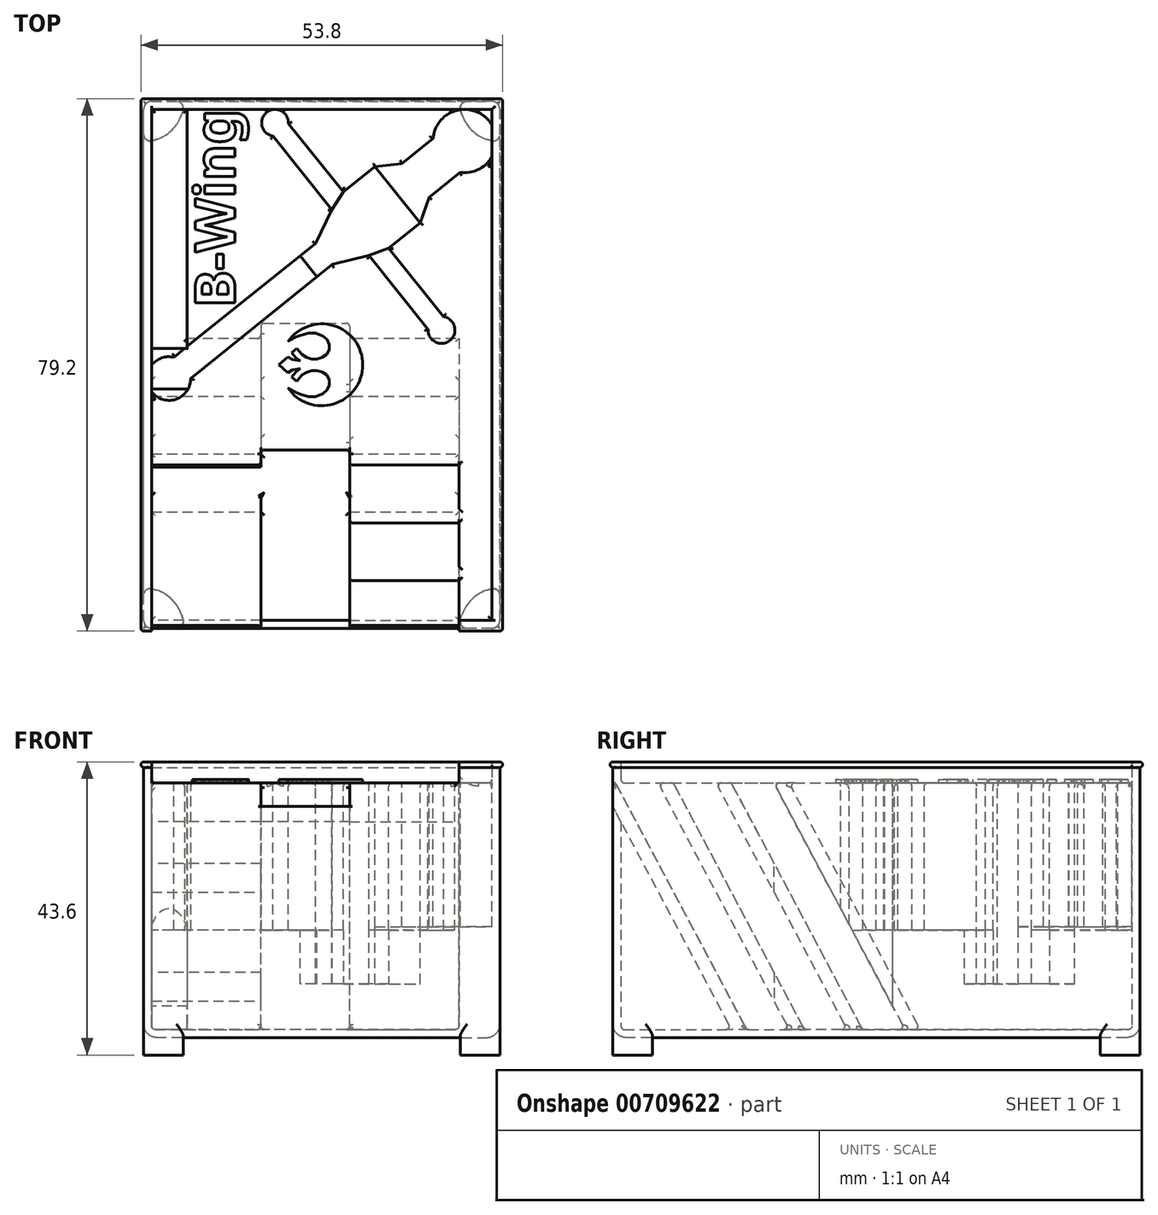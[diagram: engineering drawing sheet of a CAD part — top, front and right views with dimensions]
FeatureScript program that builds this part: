
annotation { "Feature Type Name" : "Feature", "Feature Type Description" : "" }
export const myFeature = defineFeature(function(context is Context, id is Id, definition is map)
    precondition{}
    {
        {
            var Q0;
            Q0=qCreatedBy(makeId("Front.planeOp"),FACE);
            var sketch = newSketch(context, id + "F0", { "sketchPlane" : qUnion([Q0])});
            skLineSegment(sketch, "E0.bottom", {"start": v(26.5, 20.5) * mm, "end": v(-26.5, 20.5) * mm});
            skLineSegment(sketch, "E0.top", {"start": v(26.5, -20.5) * mm, "end": v(-26.5, -20.5) * mm});
            skLineSegment(sketch, "E0.left", {"start": v(26.5, 20.5) * mm, "end": v(26.5, -20.5) * mm});
            skLineSegment(sketch, "E0.right", {"start": v(-26.5, 20.5) * mm, "end": v(-26.5, -20.5) * mm});
            skPoint(sketch, "E0.middle", {"position": v(0, 0) * mm});
            skSolve(sketch);
        }
        {
            var Q0;
            Q0=makeQuery(id+"F0.imprint","IMPRINT",FACE,{"disambiguationData":[TD([[makeQuery(id+"F0.imprint","IMPRINT",EDGE,{"derivedFrom":sQuery(id+"F0.wireOp",EDGE,"E0.bottom")}),1.0]])]});
            extrude(context, id + "F1", {"entities" : qUnion([Q0]), "depth" : 78.4 * mm, "offsetDistance" : 25 * mm, "symmetric" : true});
        }
        {
            var Q0;
            Q0=makeQuery(id+"F1.opExtrude","SWEPT_FACE",FACE,{"disambiguationData":[OSD([sQuery(id+"F0.wireOp",EDGE,"E0.bottom")])]});
            shell(context, id + "F2", {"entities" : qUnion([Q0]), "thickness" : 1.2 * mm});
        }
        {
            var Q0;
            Q0=makeQuery(id+"F1.opExtrude","SWEPT_FACE",FACE,{"disambiguationData":[OSD([sQuery(id+"F0.wireOp",EDGE,"E0.top")])]});
            var sketch = newSketch(context, id + "F3", { "sketchPlane" : qUnion([Q0])});
            skArc(sketch, "E1", {"start": v(20.62, 38) * mm, "mid": v(22.26, 34.96) * mm, "end": v(25.3, 33.32) * mm});
            skLineSegment(sketch, "E2", {"start": v(26.5, 39.2) * mm, "end": v(21.6, 39.2) * mm});
            skLineSegment(sketch, "E3", {"start": v(26.5, 39.2) * mm, "end": v(26.5, 34.3) * mm});
            skPoint(sketch, "E4.visualSharp", {"position": v(20.5, 39.2) * mm});
            skArc(sketch, "E4.filletArc", {"start": v(21.6, 39.2) * mm, "mid": v(20.83, 38.83) * mm, "end": v(20.62, 38) * mm});
            skPoint(sketch, "E5.visualSharp", {"position": v(26.5, 33.2) * mm});
            skArc(sketch, "E5.filletArc", {"start": v(25.3, 33.32) * mm, "mid": v(26.13, 33.53) * mm, "end": v(26.5, 34.3) * mm});
            skArc(sketch, "E6.MirrorCS", {"start": v(-25.3, 33.32) * mm, "mid": v(-26.13, 33.53) * mm, "end": v(-26.5, 34.3) * mm});
            skArc(sketch, "E7.MirrorCS", {"start": v(-21.6, 39.2) * mm, "mid": v(-20.83, 38.83) * mm, "end": v(-20.62, 38) * mm});
            skPoint(sketch, "E8.MirrorP", {"position": v(-20.5, 39.2) * mm});
            skArc(sketch, "E9.MirrorCS", {"start": v(-20.62, 38) * mm, "mid": v(-22.26, 34.96) * mm, "end": v(-25.3, 33.32) * mm});
            skLineSegment(sketch, "E10.MirrorCS", {"start": v(-26.5, 39.2) * mm, "end": v(-21.6, 39.2) * mm});
            skLineSegment(sketch, "E11.MirrorCS", {"start": v(-26.5, 39.2) * mm, "end": v(-26.5, 34.3) * mm});
            skPoint(sketch, "E12.MirrorP", {"position": v(-26.5, 33.2) * mm});
            skArc(sketch, "E13.MirrorCS", {"start": v(25.3, -33.32) * mm, "mid": v(26.13, -33.53) * mm, "end": v(26.5, -34.3) * mm});
            skArc(sketch, "E14.MirrorCS", {"start": v(21.6, -39.2) * mm, "mid": v(20.83, -38.83) * mm, "end": v(20.62, -38) * mm});
            skArc(sketch, "E15.MirrorCS", {"start": v(-25.3, -33.32) * mm, "mid": v(-26.13, -33.53) * mm, "end": v(-26.5, -34.3) * mm});
            skArc(sketch, "E16.MirrorCS", {"start": v(-21.6, -39.2) * mm, "mid": v(-20.83, -38.83) * mm, "end": v(-20.62, -38) * mm});
            skPoint(sketch, "E17.MirrorP", {"position": v(-26.5, -33.2) * mm});
            skPoint(sketch, "E18.MirrorP", {"position": v(20.5, -39.2) * mm});
            skPoint(sketch, "E19.MirrorP", {"position": v(26.5, -33.2) * mm});
            skLineSegment(sketch, "E20.MirrorCS", {"start": v(-26.5, -39.2) * mm, "end": v(-26.5, -34.3) * mm});
            skPoint(sketch, "E21.MirrorP", {"position": v(-20.5, -39.2) * mm});
            skLineSegment(sketch, "E22.MirrorCS", {"start": v(26.5, -39.2) * mm, "end": v(26.5, -34.3) * mm});
            skLineSegment(sketch, "E23.MirrorCS", {"start": v(-26.5, -39.2) * mm, "end": v(-21.6, -39.2) * mm});
            skLineSegment(sketch, "E24.MirrorCS", {"start": v(26.5, -39.2) * mm, "end": v(21.6, -39.2) * mm});
            skArc(sketch, "E25.MirrorCS", {"start": v(20.62, -38) * mm, "mid": v(22.26, -34.96) * mm, "end": v(25.3, -33.32) * mm});
            skArc(sketch, "E26.MirrorCS", {"start": v(-20.62, -38) * mm, "mid": v(-22.26, -34.96) * mm, "end": v(-25.3, -33.32) * mm});
            skSolve(sketch);
        }
        {
            var Q0;
            Q0=qSketchRegion(id+"F3",true);
            extrude(context, id + "F4", {"entities" : qUnion([Q0]), "operationType" : NewBodyOperationType.ADD, "depth" : 2.6 * mm, "offsetDistance" : 25 * mm});
        }
        {
            var Q0;
            Q0=makeQuery(id+"F4.boolean.opBoolean","MERGE",FACE,{"derivedFrom":[makeQuery(id+"F1.opExtrude","CAP_FACE",FACE,{"disambiguationData":[OSD([sQuery(id+"F0.wireOp",EDGE,"E0.bottom"),sQuery(id+"F0.wireOp",EDGE,"E0.top"),sQuery(id+"F0.wireOp",EDGE,"E0.left"),sQuery(id+"F0.wireOp",EDGE,"E0.right")])],"isStart":false}),makeQuery(id+"F4.opExtrude","SWEPT_FACE",FACE,{"disambiguationData":[OSD([sQuery(id+"F3.wireOp",EDGE,"E2")])]}),makeQuery(id+"F4.opExtrude","SWEPT_FACE",FACE,{"disambiguationData":[OSD([sQuery(id+"F3.wireOp",EDGE,"E10.MirrorCS")])]})]});
            var sketch = newSketch(context, id + "F5", { "sketchPlane" : qUnion([Q0])});
            skLineSegment(sketch, "E27", {"start": v(-26.5, 20.5) * mm, "end": v(-26.5, 19.7) * mm});
            skArc(sketch, "E28", {"start": v(-26.5, 20.5) * mm, "mid": v(-26.9, 20.1) * mm, "end": v(-26.5, 19.7) * mm});
            skSolve(sketch);
        }
        {
            var Q0;
            Q0=makeQuery(id+"F5.imprint","IMPRINT",FACE,{"disambiguationData":[TD([[makeQuery(id+"F5.imprint","IMPRINT",EDGE,{"derivedFrom":sQuery(id+"F5.wireOp",EDGE,"E27")}),-1.0]])]});
            var Q1;
            Q1=makeQuery(id+"F1.opExtrude","SWEPT_EDGE",EDGE,{"disambiguationData":[OSD([sQuery(id+"F0.wireOp",EDGE,"E0.bottom"),sQuery(id+"F0.wireOp",EDGE,"E0.right")])]});
            var Q2;
            Q2=makeQuery(id+"F1.opExtrude","CAP_EDGE",EDGE,{"disambiguationData":[OSD([sQuery(id+"F0.wireOp",EDGE,"E0.bottom")])],"isStart":false});
            var Q3;
            Q3=makeQuery(id+"F1.opExtrude","SWEPT_EDGE",EDGE,{"disambiguationData":[OSD([sQuery(id+"F0.wireOp",EDGE,"E0.bottom"),sQuery(id+"F0.wireOp",EDGE,"E0.left")])]});
            var Q4;
            Q4=makeQuery(id+"F1.opExtrude","CAP_EDGE",EDGE,{"disambiguationData":[OSD([sQuery(id+"F0.wireOp",EDGE,"E0.bottom")])],"isStart":true});
            sweep(context, id + "F6", {"operationType" : NewBodyOperationType.ADD, "profiles" : qUnion([Q0]), "path" : qUnion([Q1, Q2, Q3, Q4])});
        }
        {
            var Q0;
            Q0=makeQuery(id+"F1.opExtrude","CAP_EDGE",EDGE,{"disambiguationData":[OSD([sQuery(id+"F0.wireOp",EDGE,"E0.top")])],"isStart":false});
            var Q1;
            Q1=makeQuery(id+"F1.opExtrude","SWEPT_EDGE",EDGE,{"disambiguationData":[OSD([sQuery(id+"F0.wireOp",EDGE,"E0.top"),sQuery(id+"F0.wireOp",EDGE,"E0.left")])]});
            var Q2;
            Q2=makeQuery(id+"F1.opExtrude","SWEPT_EDGE",EDGE,{"disambiguationData":[OSD([sQuery(id+"F0.wireOp",EDGE,"E0.top"),sQuery(id+"F0.wireOp",EDGE,"E0.right")])]});
            var Q3;
            Q3=makeQuery(id+"F1.opExtrude","CAP_EDGE",EDGE,{"disambiguationData":[OSD([sQuery(id+"F0.wireOp",EDGE,"E0.top")])],"isStart":true});
            fillet(context, id + "F7", {"entities" : qUnion([Q0, Q1, Q2, Q3]), "radius" : 2 * mm, "tangentPropagation" : true, "allowEdgeOverflow" : false});
        }
        {
            var Q0;
            Q0=makeQuery(id+"F4.boolean.opBoolean","MERGE",EDGE,{"derivedFrom":[makeQuery(id+"F1.opExtrude","CAP_EDGE",EDGE,{"disambiguationData":[OSD([sQuery(id+"F0.wireOp",EDGE,"E0.right")])],"isStart":false}),makeQuery(id+"F4.opExtrude","SWEPT_EDGE",EDGE,{"disambiguationData":[OSD([sQuery(id+"F3.wireOp",EDGE,"E10.MirrorCS"),sQuery(id+"F3.wireOp",EDGE,"E11.MirrorCS")])]})]});
            var Q1;
            Q1=makeQuery(id+"F4.boolean.opBoolean","MERGE",EDGE,{"derivedFrom":[makeQuery(id+"F1.opExtrude","CAP_EDGE",EDGE,{"disambiguationData":[OSD([sQuery(id+"F0.wireOp",EDGE,"E0.left")])],"isStart":false}),makeQuery(id+"F4.opExtrude","SWEPT_EDGE",EDGE,{"disambiguationData":[OSD([sQuery(id+"F3.wireOp",EDGE,"E2"),sQuery(id+"F3.wireOp",EDGE,"E3")])]})]});
            var Q2;
            Q2=makeQuery(id+"F4.boolean.opBoolean","MERGE",EDGE,{"derivedFrom":[makeQuery(id+"F1.opExtrude","CAP_EDGE",EDGE,{"disambiguationData":[OSD([sQuery(id+"F0.wireOp",EDGE,"E0.left")])],"isStart":true}),makeQuery(id+"F4.opExtrude","SWEPT_EDGE",EDGE,{"disambiguationData":[OSD([sQuery(id+"F3.wireOp",EDGE,"E22.MirrorCS"),sQuery(id+"F3.wireOp",EDGE,"E24.MirrorCS")])]})]});
            var Q3;
            Q3=makeQuery(id+"F4.boolean.opBoolean","MERGE",EDGE,{"derivedFrom":[makeQuery(id+"F1.opExtrude","CAP_EDGE",EDGE,{"disambiguationData":[OSD([sQuery(id+"F0.wireOp",EDGE,"E0.right")])],"isStart":true}),makeQuery(id+"F4.opExtrude","SWEPT_EDGE",EDGE,{"disambiguationData":[OSD([sQuery(id+"F3.wireOp",EDGE,"E20.MirrorCS"),sQuery(id+"F3.wireOp",EDGE,"E23.MirrorCS")])]})]});
            fillet(context, id + "F8", {"entities" : qUnion([Q0, Q1, Q2, Q3]), "radius" : 1.2 * mm, "tangentPropagation" : true, "allowEdgeOverflow" : false});
        }
        {
            var Q0;
            Q0=makeQuery(id+"F6.opSweep","MID_CAP_EDGE",EDGE,{"disambiguationData":[OSD([sQuery(id+"F0.wireOp",EDGE,"E0.bottom"),sQuery(id+"F0.wireOp",EDGE,"E0.right"),sQuery(id+"F5.wireOp",EDGE,"E28")])],"capPos":1.0});
            var Q1;
            Q1=makeQuery(id+"F6.opSweep","CAP_EDGE",EDGE,{"disambiguationData":[OSD([sQuery(id+"F0.wireOp",EDGE,"E0.bottom"),sQuery(id+"F0.wireOp",EDGE,"E0.right"),sQuery(id+"F5.wireOp",EDGE,"E28")])],"isStart":true});
            var Q2;
            Q2=makeQuery(id+"F6.opSweep","MID_CAP_EDGE",EDGE,{"disambiguationData":[OSD([sQuery(id+"F0.wireOp",EDGE,"E0.bottom"),sQuery(id+"F0.wireOp",EDGE,"E0.left"),sQuery(id+"F5.wireOp",EDGE,"E28")])],"capPos":3.0});
            var Q3;
            Q3=makeQuery(id+"F6.opSweep","MID_CAP_EDGE",EDGE,{"disambiguationData":[OSD([sQuery(id+"F0.wireOp",EDGE,"E0.bottom"),sQuery(id+"F0.wireOp",EDGE,"E0.left"),sQuery(id+"F5.wireOp",EDGE,"E28")])],"capPos":2.0});
            fillet(context, id + "F9", {"entities" : qUnion([Q0, Q1, Q2, Q3]), "radius" : .4 * mm, "tangentPropagation" : true, "allowEdgeOverflow" : false});
        }
        {
            var Q0;
            {var subQ0=sQuery(id+"F0.wireOp",EDGE,"E0.bottom");Q0=makeQuery(id+"F2.opShell","OFFSET_EDGE",EDGE,{"disambiguationData":[OSD([subQ0]),TDD([makeQuery(id+"F1.opExtrude","CAP_EDGE",EDGE,{"disambiguationData":[OSD([subQ0])],"isStart":false})])]});}
            cPlane(context, id + "F10", {"entities" : qUnion([Q0]), "cplaneType" : CPlaneType.LINE_ANGLE, "offset" : 25 * mm, "angle" : 62 * degree, "width" : 150 * mm, "height" : 150 * mm});
        }
        {
            var Q0;
            Q0=makeQuery(id+"F1.opExtrude","SWEPT_FACE",FACE,{"disambiguationData":[OSD([sQuery(id+"F0.wireOp",EDGE,"E0.bottom")])]});
            var sketch = newSketch(context, id + "F11", { "sketchPlane" : qUnion([Q0])});
            skLineSegment(sketch, "E29", {"start": v(9.97, 17.35) * mm, "end": v(18.16, 7.15) * mm});
            skLineSegment(sketch, "E30", {"start": v(9.97, 17.35) * mm, "end": v(14.64, 21.1) * mm});
            skLineSegment(sketch, "E31", {"start": v(1.56, 14.91) * mm, "end": v(-19.49, -2) * mm});
            skLineSegment(sketch, "E32", {"start": v(15.96, 24.88) * mm, "end": v(20.63, 28.64) * mm});
            skLineSegment(sketch, "E33", {"start": v(7, 16.25) * mm, "end": v(1.56, 14.91) * mm});
            skLineSegment(sketch, "E34", {"start": v(14.64, 21.1) * mm, "end": v(15.96, 24.88) * mm});
            skArc(sketch, "E35", {"start": v(-25.27, -4.08) * mm, "mid": v(-21.64, -5.1) * mm, "end": v(-19.49, -2) * mm});
            skArc(sketch, "E36", {"start": v(20.63, 28.64) * mm, "mid": v(23.3, 29.08) * mm, "end": v(25.3, 30.92) * mm});
            skArc(sketch, "E37", {"start": v(15.82, 5.27) * mm, "mid": v(19.07, 3.62) * mm, "end": v(18.16, 7.15) * mm});
            skLineSegment(sketch, "E38.trimOffspring", {"start": v(15.82, 5.27) * mm, "end": v(7, 16.25) * mm});
            skLineSegment(sketch, "E39.MirrorCS", {"start": v(7.92, 29.47) * mm, "end": v(11.9, 29.94) * mm});
            skLineSegment(sketch, "E40.MirrorCS", {"start": v(11.9, 29.94) * mm, "end": v(16.57, 33.7) * mm});
            skArc(sketch, "E41.MirrorCS", {"start": v(16.57, 33.7) * mm, "mid": v(19.88, 37.8) * mm, "end": v(24.91, 36.24) * mm});
            skLineSegment(sketch, "E42.MirrorCS", {"start": v(3.24, 25.71) * mm, "end": v(7.92, 29.47) * mm});
            skLineSegment(sketch, "E43.MirrorCS", {"start": v(-7.29, 34.03) * mm, "end": v(1.53, 23.06) * mm});
            skArc(sketch, "E44.MirrorCS", {"start": v(-25.27, -4.08) * mm, "mid": v(-25.29, -4.06) * mm, "end": v(-25.3, -4.05) * mm});
            skLineSegment(sketch, "E45.MirrorCS", {"start": v(1.53, 23.06) * mm, "end": v(-0.95, 18.03) * mm});
            skLineSegment(sketch, "E46.MirrorCS", {"start": v(-0.95, 18.03) * mm, "end": v(-22, 1.12) * mm});
            skLineSegment(sketch, "E47.MirrorCS", {"start": v(3.24, 25.71) * mm, "end": v(-4.95, 35.9) * mm});
            skArc(sketch, "E48.MirrorCS", {"start": v(-7.29, 34.03) * mm, "mid": v(-8.2, 37.56) * mm, "end": v(-4.95, 35.9) * mm});
            skPoint(sketch, "E49.MirrorP", {"position": v(14.23, 31.82) * mm});
            skLineSegment(sketch, "E50.0", {"start": v(25.3, 38) * mm, "end": v(-25.3, 38) * mm});
            skArc(sketch, "E51.MirrorCS", {"start": v(25.27, 4.08) * mm, "mid": v(25.29, 4.06) * mm, "end": v(25.3, 4.05) * mm});
            skArc(sketch, "E52.trimOffspring", {"start": v(25.3, 35.68) * mm, "mid": v(25.12, 35.97) * mm, "end": v(24.91, 36.24) * mm});
            skArc(sketch, "E53.trimOffspring", {"start": v(-25.3, -0.05) * mm, "mid": v(-23.82, 1.02) * mm, "end": v(-22, 1.12) * mm});
            skLineSegment(sketch, "E54", {"start": v(7.92, 29.47) * mm, "end": v(14.64, 21.1) * mm});
            skLineSegment(sketch, "E55", {"start": v(-22, 1.12) * mm, "end": v(-19.49, -2) * mm});
            skLineSegment(sketch, "E56", {"start": v(-1.97, 14.64) * mm, "end": v(-0.72, 13.08) * mm});
            skLineSegment(sketch, "E57", {"start": v(-0.72, 13.08) * mm, "end": v(-3.22, 16.2) * mm});
            skLineSegment(sketch, "E58", {"start": v(3.24, 25.71) * mm, "end": v(1.53, 23.06) * mm});
            skLineSegment(sketch, "E59", {"start": v(9.97, 17.35) * mm, "end": v(7, 16.25) * mm});
            skLineSegment(sketch, "E60", {"start": v(-26.5, -39.2) * mm, "end": v(-26.5, -15.2) * mm});
            skLineSegment(sketch, "E61", {"start": v(-26.5, -15.2) * mm, "end": v(20.4, -15.2) * mm});
            skLineSegment(sketch, "E62", {"start": v(25.3, -38) * mm, "end": v(20.4, -38) * mm});
            skLineSegment(sketch, "E63", {"start": v(20.4, -38) * mm, "end": v(20.4, -15.2) * mm});
            skPoint(sketch, "E64.orphan", {"position": v(26.5, -15.2) * mm});
            skSolve(sketch);
        }
        {
            var Q0;
            Q0=makeQuery(id+"F2.opShell","OFFSET_FACE",FACE,{"disambiguationData":[OSD([sQuery(id+"F0.wireOp",EDGE,"E0.top")])]});
            var sketch = newSketch(context, id + "F12", { "sketchPlane" : qUnion([Q0])});
            skLineSegment(sketch, "E65", {"start": v(9.97, 17.35) * mm, "end": v(18.16, 7.15) * mm});
            skLineSegment(sketch, "E66", {"start": v(9.97, 17.35) * mm, "end": v(14.64, 21.1) * mm});
            skLineSegment(sketch, "E67", {"start": v(1.56, 14.91) * mm, "end": v(-19.49, -2) * mm});
            skLineSegment(sketch, "E68", {"start": v(15.96, 24.88) * mm, "end": v(20.63, 28.64) * mm});
            skLineSegment(sketch, "E69", {"start": v(7, 16.25) * mm, "end": v(1.56, 14.91) * mm});
            skLineSegment(sketch, "E70", {"start": v(14.64, 21.1) * mm, "end": v(15.96, 24.88) * mm});
            skArc(sketch, "E71", {"start": v(-25.27, -4.08) * mm, "mid": v(-21.64, -5.1) * mm, "end": v(-19.49, -2) * mm});
            skArc(sketch, "E72", {"start": v(20.63, 28.64) * mm, "mid": v(23.3, 29.08) * mm, "end": v(25.3, 30.92) * mm});
            skArc(sketch, "E73", {"start": v(15.82, 5.27) * mm, "mid": v(19.07, 3.62) * mm, "end": v(18.16, 7.15) * mm});
            skLineSegment(sketch, "E74.trimOffspring", {"start": v(15.82, 5.27) * mm, "end": v(7, 16.25) * mm});
            skLineSegment(sketch, "E75.MirrorCS", {"start": v(7.92, 29.47) * mm, "end": v(11.9, 29.94) * mm});
            skLineSegment(sketch, "E76.MirrorCS", {"start": v(11.9, 29.94) * mm, "end": v(16.57, 33.7) * mm});
            skArc(sketch, "E77.MirrorCS", {"start": v(16.57, 33.7) * mm, "mid": v(19.88, 37.8) * mm, "end": v(24.91, 36.24) * mm});
            skLineSegment(sketch, "E78.MirrorCS", {"start": v(3.24, 25.71) * mm, "end": v(7.92, 29.47) * mm});
            skLineSegment(sketch, "E79.MirrorCS", {"start": v(-7.29, 34.03) * mm, "end": v(1.53, 23.06) * mm});
            skArc(sketch, "E80.MirrorCS", {"start": v(-25.27, -4.08) * mm, "mid": v(-25.29, -4.06) * mm, "end": v(-25.3, -4.05) * mm});
            skLineSegment(sketch, "E81.MirrorCS", {"start": v(1.53, 23.06) * mm, "end": v(-0.95, 18.03) * mm});
            skLineSegment(sketch, "E82.MirrorCS", {"start": v(-0.95, 18.03) * mm, "end": v(-22, 1.12) * mm});
            skLineSegment(sketch, "E83.MirrorCS", {"start": v(3.24, 25.71) * mm, "end": v(-4.95, 35.9) * mm});
            skArc(sketch, "E84.MirrorCS", {"start": v(-7.29, 34.03) * mm, "mid": v(-8.2, 37.56) * mm, "end": v(-4.95, 35.9) * mm});
            skPoint(sketch, "E85.MirrorP", {"position": v(14.23, 31.82) * mm});
            skLineSegment(sketch, "E86.0", {"start": v(25.3, 38) * mm, "end": v(-25.3, 38) * mm});
            skArc(sketch, "E87.MirrorCS", {"start": v(25.27, 4.08) * mm, "mid": v(25.29, 4.06) * mm, "end": v(25.3, 4.05) * mm});
            skArc(sketch, "E88.trimOffspring", {"start": v(25.3, 35.68) * mm, "mid": v(25.12, 35.97) * mm, "end": v(24.91, 36.24) * mm});
            skArc(sketch, "E89.trimOffspring", {"start": v(-25.3, -0.05) * mm, "mid": v(-23.82, 1.02) * mm, "end": v(-22, 1.12) * mm});
            skLineSegment(sketch, "E90", {"start": v(7.92, 29.47) * mm, "end": v(14.64, 21.1) * mm});
            skLineSegment(sketch, "E91", {"start": v(-22, 1.12) * mm, "end": v(-19.49, -2) * mm});
            skLineSegment(sketch, "E92", {"start": v(-1.97, 14.64) * mm, "end": v(-0.72, 13.08) * mm});
            skLineSegment(sketch, "E93", {"start": v(-0.72, 13.08) * mm, "end": v(-3.22, 16.2) * mm});
            skLineSegment(sketch, "E94", {"start": v(3.24, 25.71) * mm, "end": v(1.53, 23.06) * mm});
            skLineSegment(sketch, "E95", {"start": v(9.97, 17.35) * mm, "end": v(7, 16.25) * mm});
            skLineSegment(sketch, "E96", {"start": v(-26.5, -39.2) * mm, "end": v(-26.5, -15.2) * mm});
            skLineSegment(sketch, "E97", {"start": v(-26.5, -15.2) * mm, "end": v(20.4, -15.2) * mm});
            skLineSegment(sketch, "E98", {"start": v(25.3, -39.5) * mm, "end": v(20.4, -39.5) * mm});
            skLineSegment(sketch, "E99", {"start": v(20.4, -38) * mm, "end": v(20.4, -15.2) * mm});
            skPoint(sketch, "E100.orphan", {"position": v(26.5, -15.2) * mm});
            skSolve(sketch);
        }
        {
            var Q0;
            Q0=makeQuery(id+"F2.opShell","OFFSET_FACE",FACE,{"disambiguationData":[OSD([sQuery(id+"F0.wireOp",EDGE,"E0.top")])]});
            var sketch = newSketch(context, id + "F13", { "sketchPlane" : qUnion([Q0])});
            skLineSegment(sketch, "E101.2", {"start": v(26.5, 6.4) * mm, "end": v(26.5, 39.2) * mm});
            skPoint(sketch, "E102", {"position": v(-22.55, 27.66) * mm});
            skLineSegment(sketch, "E103", {"start": v(-20, 38) * mm, "end": v(-20, 2.4) * mm});
            skLineSegment(sketch, "E104", {"start": v(-20, 2.4) * mm, "end": v(-25.3, 2.4) * mm});
            skLineSegment(sketch, "E105", {"start": v(-25.3, 2.4) * mm, "end": v(-25.3, 38) * mm});
            skLineSegment(sketch, "E106", {"start": v(-25.3, 38) * mm, "end": v(-20, 38) * mm});
            skSolve(sketch);
        }
        {
            var Q0;
            Q0=qCreatedBy(id+"F10.planeOp",FACE);
            var sketch = newSketch(context, id + "F14", { "sketchPlane" : qUnion([Q0])});
            skPoint(sketch, "E107.0", {"position": v(-25.3, -26.1) * mm});
            skPoint(sketch, "E108.0", {"position": v(13.11, 38) * mm});
            skLineSegment(sketch, "E109", {"start": v(13.11, 38) * mm, "end": v(13.11, 12.8) * mm});
            skLineSegment(sketch, "E110.0", {"start": v(-25.3, -38) * mm, "end": v(-25.3, 38) * mm});
            skLineSegment(sketch, "E111.bottom", {"start": v(20.4, -3.3) * mm, "end": v(20.4, -5.3) * mm});
            skLineSegment(sketch, "E111.top", {"start": v(4.15, -3.3) * mm, "end": v(4.15, -5.3) * mm});
            skLineSegment(sketch, "E111.left", {"start": v(20.4, -3.3) * mm, "end": v(4.15, -3.3) * mm});
            skLineSegment(sketch, "E111.right", {"start": v(20.4, -5.3) * mm, "end": v(4.15, -5.3) * mm});
            skLineSegment(sketch, "E112", {"start": v(20.4, -5.3) * mm, "end": v(20.4, -10.9) * mm});
            skLineSegment(sketch, "E113", {"start": v(20.4, -10.9) * mm, "end": v(4.15, -10.9) * mm});
            skLineSegment(sketch, "E114", {"start": v(4.15, -10.9) * mm, "end": v(4.15, -12.9) * mm});
            skLineSegment(sketch, "E115", {"start": v(4.15, -12.9) * mm, "end": v(20.4, -12.9) * mm});
            skLineSegment(sketch, "E116", {"start": v(20.4, -12.9) * mm, "end": v(20.4, -18.5) * mm});
            skLineSegment(sketch, "E117", {"start": v(20.4, -18.5) * mm, "end": v(4.15, -18.5) * mm});
            skLineSegment(sketch, "E118", {"start": v(4.15, -18.5) * mm, "end": v(4.15, -20.5) * mm});
            skLineSegment(sketch, "E119", {"start": v(4.15, -20.5) * mm, "end": v(20.4, -20.5) * mm});
            skLineSegment(sketch, "E120", {"start": v(20.4, -20.5) * mm, "end": v(20.4, -26.1) * mm});
            skLineSegment(sketch, "E121", {"start": v(20.4, -26.1) * mm, "end": v(4.15, -26.1) * mm});
            skLineSegment(sketch, "E122", {"start": v(4.15, -26.1) * mm, "end": v(4.15, -28.1) * mm});
            skLineSegment(sketch, "E123", {"start": v(4.15, -28.1) * mm, "end": v(20.4, -28.1) * mm});
            skLineSegment(sketch, "E124", {"start": v(20.4, -28.1) * mm, "end": v(20.4, -26.1) * mm});
            skLineSegment(sketch, "E125", {"start": v(20.4, -10.9) * mm, "end": v(20.4, -12.9) * mm});
            skLineSegment(sketch, "E126", {"start": v(20.4, -18.5) * mm, "end": v(20.4, -20.5) * mm});
            skLineSegment(sketch, "E127", {"start": v(4.15, -3.3) * mm, "end": v(-9.05, -3.3) * mm});
            skLineSegment(sketch, "E128", {"start": v(4.15, -28.1) * mm, "end": v(-9.05, -28.1) * mm});
            skPoint(sketch, "E129.startSnap0", {"position": v(-2.45, -3.3) * mm});
            skLineSegment(sketch, "E130.MirrorCS", {"start": v(-25.3, -10.9) * mm, "end": v(-25.3, -12.9) * mm});
            skLineSegment(sketch, "E131.MirrorCS", {"start": v(-25.3, -18.5) * mm, "end": v(-25.3, -20.5) * mm});
            skLineSegment(sketch, "E132.MirrorCS", {"start": v(-9.05, -10.9) * mm, "end": v(-9.05, -12.9) * mm});
            skLineSegment(sketch, "E133.MirrorCS", {"start": v(-9.05, -3.3) * mm, "end": v(-9.05, -5.3) * mm});
            skLineSegment(sketch, "E134.MirrorCS", {"start": v(-9.05, -18.5) * mm, "end": v(-9.05, -20.5) * mm});
            skLineSegment(sketch, "E135.MirrorCS", {"start": v(-9.05, -26.1) * mm, "end": v(-9.05, -28.1) * mm});
            skLineSegment(sketch, "E136.MirrorCS", {"start": v(-25.3, -3.3) * mm, "end": v(-25.3, -5.3) * mm});
            skLineSegment(sketch, "E137.MirrorCS", {"start": v(-9.05, -12.9) * mm, "end": v(-25.3, -12.9) * mm});
            skLineSegment(sketch, "E138.MirrorCS", {"start": v(-9.05, -20.5) * mm, "end": v(-25.3, -20.5) * mm});
            skLineSegment(sketch, "E139.MirrorCS", {"start": v(-25.3, -3.3) * mm, "end": v(-9.05, -3.3) * mm});
            skLineSegment(sketch, "E140.MirrorCS", {"start": v(-25.3, -5.3) * mm, "end": v(-25.3, -10.9) * mm});
            skLineSegment(sketch, "E141.MirrorCS", {"start": v(-9.05, -28.1) * mm, "end": v(-25.3, -28.1) * mm});
            skLineSegment(sketch, "E142.MirrorCS", {"start": v(-25.3, -10.9) * mm, "end": v(-9.05, -10.9) * mm});
            skLineSegment(sketch, "E143.MirrorCS", {"start": v(-25.3, -5.3) * mm, "end": v(-9.05, -5.3) * mm});
            skLineSegment(sketch, "E144.MirrorCS", {"start": v(-25.3, -12.9) * mm, "end": v(-25.3, -18.5) * mm});
            skLineSegment(sketch, "E145.MirrorCS", {"start": v(-25.3, -26.1) * mm, "end": v(-9.05, -26.1) * mm});
            skLineSegment(sketch, "E146.MirrorCS", {"start": v(-25.3, -20.5) * mm, "end": v(-25.3, -26.1) * mm});
            skLineSegment(sketch, "E147.MirrorCS", {"start": v(-25.3, -18.5) * mm, "end": v(-9.05, -18.5) * mm});
            skPoint(sketch, "E148.0", {"position": v(-13.11, -9.06) * mm});
            skLineSegment(sketch, "E149", {"start": v(-25.3, -26.1) * mm, "end": v(-25.3, -23.93) * mm});
            skSolve(sketch);
        }
        {
            var Q0;
            Q0 = qSketchRegion(id + "F12", true);
            var Q1;
            {var subQ7=sQuery(id+"F12.wireOp",EDGE,"E79.MirrorCS");Q1=makeQuery(id+"F12.imprint","IMPRINT",FACE,{"disambiguationData":[TD([[makeQuery(id+"F12.imprint","IMPRINT",EDGE,{"derivedFrom":subQ7}),-1.0]])]});}
            var Q2;
            Q2=makeQuery(id+"F12.imprint","IMPRINT",FACE,{"disambiguationData":[TD([[makeQuery(id+"F12.imprint","IMPRINT",EDGE,{"derivedFrom":sQuery(id+"F12.wireOp",EDGE,"E68")}),1.0]])]});
            var Q3;
            Q3=makeQuery(id+"F12.imprint","IMPRINT",FACE,{"disambiguationData":[TD([[makeQuery(id+"F12.imprint","IMPRINT",EDGE,{"derivedFrom":sQuery(id+"F12.wireOp",EDGE,"E65")}),1.0]])]});
            var Q4;
            Q4=makeQuery(id+"F12.imprint","IMPRINT",FACE,{"disambiguationData":[TD([[makeQuery(id+"F12.imprint","IMPRINT",EDGE,{"derivedFrom":sQuery(id+"F12.wireOp",EDGE,"E71")}),1.0]])]});
            var Q5;
            {var subQ0=sQuery(id+"F12.wireOp",EDGE,"E88.trimOffspring");Q5=makeQuery(id+"F12.imprint","IMPRINT",FACE,{"disambiguationData":[TD([[makeQuery(id+"F12.imprint","IMPRINT",EDGE,{"derivedFrom":subQ0}),-1.0]])]});}
            var Q6;
            Q6=makeQuery(id+"F2.opShell","OFFSET_FACE",FACE,{"disambiguationData":[OSD([sQuery(id+"F0.wireOp",EDGE,"E0.top")])]});
            extrude(context, id + "F15", {"entities" : qUnion([Q0, Q1, Q2, Q3, Q4, Q5]), "operationType" : NewBodyOperationType.ADD, "depth" : 36.7 * mm, "endBoundEntityFace" : qUnion([Q6]), "offsetDistance" : 25 * mm});
        }
        {
            var Q0;
            Q0=makeQuery(id+"F14.imprint","IMPRINT",FACE,{"disambiguationData":[TD([[makeQuery(id+"F14.imprint","IMPRINT",EDGE,{"derivedFrom":sQuery(id+"F14.wireOp",EDGE,"E111.top")}),-1.0]])]});
            var Q1;
            Q1=makeQuery(id+"F2.opShell","OFFSET_FACE",FACE,{"disambiguationData":[OSD([sQuery(id+"F0.wireOp",EDGE,"E0.top")])]});
            extrude(context, id + "F16", {"entities" : qUnion([Q0]), "operationType" : NewBodyOperationType.REMOVE, "endBound" : BoundingType.UP_TO_SURFACE, "oppositeDirection" : true, "depth" : 25 * mm, "endBoundEntityFace" : qUnion([Q1]), "offsetDistance" : 25 * mm, "hasSecondDirection" : true, "secondDirectionOppositeDirection" : false, "secondDirectionDepth" : 25 * mm});
        }
        {
            var Q0;
            Q0=makeQuery(id+"F14.imprint","IMPRINT",FACE,{"disambiguationData":[TD([[makeQuery(id+"F14.imprint","IMPRINT",EDGE,{"derivedFrom":sQuery(id+"F14.wireOp",EDGE,"E133.MirrorCS")}),-1.0]])]});
            var Q1;
            Q1=makeQuery(id+"F14.imprint","IMPRINT",FACE,{"disambiguationData":[TD([[makeQuery(id+"F14.imprint","IMPRINT",EDGE,{"derivedFrom":sQuery(id+"F14.wireOp",EDGE,"E111.bottom")}),-1.0]])]});
            var Q2;
            Q2=makeQuery(id+"F14.imprint","IMPRINT",FACE,{"disambiguationData":[TD([[makeQuery(id+"F14.imprint","IMPRINT",EDGE,{"derivedFrom":sQuery(id+"F14.wireOp",EDGE,"E113")}),1.0]])]});
            var Q3;
            Q3=makeQuery(id+"F14.imprint","IMPRINT",FACE,{"disambiguationData":[TD([[makeQuery(id+"F14.imprint","IMPRINT",EDGE,{"derivedFrom":sQuery(id+"F14.wireOp",EDGE,"E117")}),1.0]])]});
            var Q4;
            Q4=makeQuery(id+"F14.imprint","IMPRINT",FACE,{"disambiguationData":[TD([[makeQuery(id+"F14.imprint","IMPRINT",EDGE,{"derivedFrom":sQuery(id+"F14.wireOp",EDGE,"E121")}),1.0]])]});
            var Q5;
            Q5=makeQuery(id+"F14.imprint","IMPRINT",FACE,{"disambiguationData":[TD([[makeQuery(id+"F14.imprint","IMPRINT",EDGE,{"derivedFrom":sQuery(id+"F14.wireOp",EDGE,"E135.MirrorCS")}),-1.0]])]});
            var Q6;
            Q6=makeQuery(id+"F14.imprint","IMPRINT",FACE,{"disambiguationData":[TD([[makeQuery(id+"F14.imprint","IMPRINT",EDGE,{"derivedFrom":sQuery(id+"F14.wireOp",EDGE,"E131.MirrorCS")}),1.0]])]});
            var Q7;
            Q7=makeQuery(id+"F14.imprint","IMPRINT",FACE,{"disambiguationData":[TD([[makeQuery(id+"F14.imprint","IMPRINT",EDGE,{"derivedFrom":sQuery(id+"F14.wireOp",EDGE,"E130.MirrorCS")}),1.0]])]});
            var Q8;
            Q8=makeQuery(id+"F2.opShell","OFFSET_FACE",FACE,{"disambiguationData":[OSD([sQuery(id+"F0.wireOp",EDGE,"E0.top")])]});
            extrude(context, id + "F17", {"entities" : qUnion([Q0, Q1, Q2, Q3, Q4, Q5, Q6, Q7]), "operationType" : NewBodyOperationType.ADD, "endBound" : BoundingType.UP_TO_SURFACE, "oppositeDirection" : true, "depth" : 25 * mm, "endBoundEntityFace" : qUnion([Q8]), "offsetDistance" : 25 * mm});
        }
        {
            var Q0;
            Q0=makeQuery(id+"F13.imprint","IMPRINT",FACE,{"disambiguationData":[TD([[makeQuery(id+"F13.imprint","IMPRINT",EDGE,{"derivedFrom":sQuery(id+"F13.wireOp",EDGE,"E103")}),-1.0]])]});
            var Q1;
            {var subQ0=sQuery(id+"F0.wireOp",EDGE,"E0.right");var subQ1=sQuery(id+"F0.wireOp",EDGE,"E0.bottom");Q1=makeQuery(id+"F2.opShell","OFFSET_VERTEX",VERTEX,{"disambiguationData":[OSD([subQ1,subQ0]),TDD([makeQuery(id+"F1.opExtrude","CAP_VERTEX",VERTEX,{"disambiguationData":[OSD([subQ1,subQ0])],"isStart":true})])]});}
            extrude(context, id + "F18", {"entities" : qUnion([Q0]), "operationType" : NewBodyOperationType.REMOVE, "endBound" : BoundingType.UP_TO_VERTEX, "depth" : 25 * mm, "endBoundEntityVertex" : qUnion([Q1]), "offsetDistance" : 25 * mm});
        }
        {
            var Q0;
            Q0=makeQuery(id+"F15.opExtrude","CAP_FACE",FACE,{"disambiguationData":[OSD([sQuery(id+"F0.wireOp",EDGE,"E0.top"),sQuery(id+"F0.wireOp",EDGE,"E0.left"),sQuery(id+"F0.wireOp",EDGE,"E0.right"),sQuery(id+"F12.wireOp",EDGE,"E86.0"),sQuery(id+"F12.wireOp",EDGE,"E97"),sQuery(id+"F12.wireOp",EDGE,"E99")])],"isStart":false});
            var sketch = newSketch(context, id + "F19", { "sketchPlane" : qUnion([Q0])});
            skPoint(sketch, "E150", {"position": v(-25.3, 38) * mm});
            skPoint(sketch, "E151.middle", {"position": v(0, 0) * mm});
            skLineSegment(sketch, "E152.0", {"start": v(25.3, 38) * mm, "end": v(-25.3, 38) * mm});
            skLineSegment(sketch, "E152.1", {"start": v(-25.3, -14.63) * mm, "end": v(-25.3, 38) * mm});
            skLineSegment(sketch, "E152.2", {"start": v(25.3, -38) * mm, "end": v(25.3, 38) * mm});
            skLineSegment(sketch, "E152.3", {"start": v(25.3, -38) * mm, "end": v(20.4, -38) * mm});
            skLineSegment(sketch, "E152.4", {"start": v(20.4, -39.2) * mm, "end": v(20.4, -38) * mm});
            skLineSegment(sketch, "E153", {"start": v(20.4, -39.2) * mm, "end": v(20.4, -59.2) * mm});
            skLineSegment(sketch, "E154", {"start": v(20.4, -59.2) * mm, "end": v(-25.3, -59.2) * mm});
            skLineSegment(sketch, "E155", {"start": v(-25.3, -59.2) * mm, "end": v(-25.3, -14.63) * mm});
            skSolve(sketch);
        }
        {
            var Q0;
            Q0=qSketchRegion(id+"F19",true);
            extrude(context, id + "F20", {"entities" : qUnion([Q0]), "operationType" : NewBodyOperationType.REMOVE, "depth" : 100 * mm, "offsetDistance" : 25 * mm});
        }
        {
            var Q0;
            Q0=makeQuery(id+"F4.boolean.opBoolean","MERGE",FACE,{"derivedFrom":[makeQuery(id+"F1.opExtrude","SWEPT_FACE",FACE,{"disambiguationData":[OSD([sQuery(id+"F0.wireOp",EDGE,"E0.right")])]}),makeQuery(id+"F4.opExtrude","SWEPT_FACE",FACE,{"disambiguationData":[OSD([sQuery(id+"F3.wireOp",EDGE,"E11.MirrorCS")])]}),makeQuery(id+"F4.opExtrude","SWEPT_FACE",FACE,{"disambiguationData":[OSD([sQuery(id+"F3.wireOp",EDGE,"E20.MirrorCS")])]})]});
            var sketch = newSketch(context, id + "F21", { "sketchPlane" : qUnion([Q0])});
            skLineSegment(sketch, "E156.2", {"start": v(39.2, 19.7) * mm, "end": v(39.2, 18.14) * mm});
            skLineSegment(sketch, "E157", {"start": v(39.2, 20.5) * mm, "end": v(49.2, 20.5) * mm});
            skArc(sketch, "E158.0", {"start": v(39.2, 20.5) * mm, "mid": v(39.6, 20.1) * mm, "end": v(39.2, 19.7) * mm});
            skLineSegment(sketch, "E159.0", {"start": v(39.2, 18.14) * mm, "end": v(39.2, 13.88) * mm});
            skLineSegment(sketch, "E160.0", {"start": v(39.2, 13.88) * mm, "end": v(39.2, -23.1) * mm});
            skLineSegment(sketch, "E161.MirrorCS", {"start": v(49.2, 20.5) * mm, "end": v(49.2, -23.1) * mm});
            skLineSegment(sketch, "E162", {"start": v(49.2, -23.1) * mm, "end": v(39.2, -23.1) * mm});
            skSolve(sketch);
        }
        {
            var Q0;
            Q0=qSketchRegion(id+"F21",true);
            extrude(context, id + "F22", {"entities" : qUnion([Q0]), "operationType" : NewBodyOperationType.REMOVE, "oppositeDirection" : true, "depth" : 200 * mm, "offsetDistance" : 25 * mm});
        }
        {
            var Q0;
            Q0=makeQuery(id+"F11.imprint","IMPRINT",FACE,{"disambiguationData":[TD([[makeQuery(id+"F11.imprint","IMPRINT",EDGE,{"derivedFrom":sQuery(id+"F11.wireOp",EDGE,"E30")}),1.0]])]});
            extrude(context, id + "F23", {"entities" : qUnion([Q0]), "operationType" : NewBodyOperationType.REMOVE, "oppositeDirection" : true, "depth" : 33 * mm, "offsetDistance" : 25 * mm});
        }
        {
            var Q0;
            Q0=makeQuery(id+"F11.imprint","IMPRINT",FACE,{"disambiguationData":[TD([[makeQuery(id+"F11.imprint","IMPRINT",EDGE,{"derivedFrom":sQuery(id+"F11.wireOp",EDGE,"E32")}),1.0]])]});
            extrude(context, id + "F24", {"entities" : qUnion([Q0]), "operationType" : NewBodyOperationType.REMOVE, "oppositeDirection" : true, "depth" : 24.5 * mm, "offsetDistance" : 25 * mm});
        }
        {
            var Q0;
            Q0=makeQuery(id+"F11.imprint","IMPRINT",FACE,{"disambiguationData":[TD([[makeQuery(id+"F11.imprint","IMPRINT",EDGE,{"derivedFrom":sQuery(id+"F11.wireOp",EDGE,"E35")}),1.0]])]});
            extrude(context, id + "F25", {"entities" : qUnion([Q0]), "operationType" : NewBodyOperationType.REMOVE, "oppositeDirection" : true, "depth" : 25 * mm, "offsetDistance" : 25 * mm});
        }
        {
            var Q0;
            {var subQ4=sQuery(id+"F11.wireOp",EDGE,"E55");Q0=makeQuery(id+"F11.imprint","IMPRINT",FACE,{"disambiguationData":[TD([[makeQuery(id+"F11.imprint","IMPRINT",EDGE,{"derivedFrom":subQ4}),1.0]])]});}
            var Q1;
            {var subQ3=sQuery(id+"F11.wireOp",EDGE,"E43.MirrorCS");Q1=makeQuery(id+"F11.imprint","IMPRINT",FACE,{"disambiguationData":[TD([[makeQuery(id+"F11.imprint","IMPRINT",EDGE,{"derivedFrom":subQ3}),1.0]])]});}
            var Q2;
            Q2=makeQuery(id+"F11.imprint","IMPRINT",FACE,{"disambiguationData":[TD([[makeQuery(id+"F11.imprint","IMPRINT",EDGE,{"derivedFrom":sQuery(id+"F11.wireOp",EDGE,"E29")}),-1.0]])]});
            extrude(context, id + "F26", {"entities" : qUnion([Q0, Q1, Q2]), "operationType" : NewBodyOperationType.REMOVE, "oppositeDirection" : true, "depth" : 25 * mm, "offsetDistance" : 25 * mm});
        }
        {
            var Q0;
            {var subQ0=sQuery(id+"F14.wireOp",EDGE,"E143.MirrorCS");var subQ1=makeQuery(id+"F16.boolean.opBoolean","COPY",FACE,{"derivedFrom":makeQuery(id+"F16.opExtrude","SWEPT_FACE",FACE,{"disambiguationData":[OSD([subQ0])]})});var subQ2=sQuery(id+"F14.wireOp",EDGE,"E119");var subQ3=makeQuery(id+"F16.boolean.opBoolean","COPY",FACE,{"derivedFrom":makeQuery(id+"F16.opExtrude","SWEPT_FACE",FACE,{"disambiguationData":[OSD([subQ2])]})});var subQ4=sQuery(id+"F14.wireOp",EDGE,"E118");var subQ5=makeQuery(id+"F16.boolean.opBoolean","COPY",FACE,{"derivedFrom":makeQuery(id+"F16.opExtrude","SWEPT_FACE",FACE,{"disambiguationData":[OSD([subQ4])]})});var subQ6=makeQuery(id+"F18.opExtrude","SWEPT_FACE",FACE,{"disambiguationData":[OSD([sQuery(id+"F13.wireOp",EDGE,"E105")])]});var subQ7=sQuery(id+"F14.wireOp",EDGE,"E117");var subQ8=makeQuery(id+"F16.boolean.opBoolean","COPY",FACE,{"derivedFrom":makeQuery(id+"F16.opExtrude","SWEPT_FACE",FACE,{"disambiguationData":[OSD([subQ7])]})});var subQ9=sQuery(id+"F14.wireOp",EDGE,"E115");var subQ10=makeQuery(id+"F16.boolean.opBoolean","COPY",FACE,{"derivedFrom":makeQuery(id+"F16.opExtrude","SWEPT_FACE",FACE,{"disambiguationData":[OSD([subQ9])]})});var subQ11=sQuery(id+"F14.wireOp",EDGE,"E114");var subQ12=makeQuery(id+"F16.boolean.opBoolean","COPY",FACE,{"derivedFrom":makeQuery(id+"F16.opExtrude","SWEPT_FACE",FACE,{"disambiguationData":[OSD([subQ11])]})});var subQ13=sQuery(id+"F14.wireOp",EDGE,"E113");var subQ14=makeQuery(id+"F16.boolean.opBoolean","COPY",FACE,{"derivedFrom":makeQuery(id+"F16.opExtrude","SWEPT_FACE",FACE,{"disambiguationData":[OSD([subQ13])]})});var subQ15=sQuery(id+"F14.wireOp",EDGE,"E133.MirrorCS");var subQ16=makeQuery(id+"F17.opExtrude","SWEPT_FACE",FACE,{"disambiguationData":[OSD([subQ15])]});var subQ17=sQuery(id+"F14.wireOp",EDGE,"E111.right");var subQ18=makeQuery(id+"F16.boolean.opBoolean","COPY",FACE,{"derivedFrom":makeQuery(id+"F16.opExtrude","SWEPT_FACE",FACE,{"disambiguationData":[OSD([subQ17])]})});var subQ19=sQuery(id+"F14.wireOp",EDGE,"E111.top");var subQ20=makeQuery(id+"F16.boolean.opBoolean","COPY",FACE,{"derivedFrom":makeQuery(id+"F16.opExtrude","SWEPT_FACE",FACE,{"disambiguationData":[OSD([subQ19])]})});var subQ21=sQuery(id+"F12.wireOp",EDGE,"E99");var subQ22=makeQuery(id+"F15.opExtrude","SWEPT_FACE",FACE,{"disambiguationData":[OSD([subQ21])]});var subQ23=makeQuery(id+"F16.opExtrude","SWEPT_FACE",FACE,{"disambiguationData":[OSD([sQuery(id+"F14.wireOp",EDGE,"E116")])]});var subQ24=makeQuery(id+"F17.opExtrude","SWEPT_FACE",FACE,{"disambiguationData":[OSD([subQ19])]});var subQ25=makeQuery(id+"F16.opExtrude","SWEPT_FACE",FACE,{"disambiguationData":[OSD([sQuery(id+"F14.wireOp",EDGE,"E120")])]});var subQ26=makeQuery(id+"F16.boolean.opBoolean","COPY",FACE,{"derivedFrom":makeQuery(id+"F16.opExtrude","SWEPT_FACE",FACE,{"disambiguationData":[OSD([sQuery(id+"F14.wireOp",EDGE,"E127")])]})});var subQ27=makeQuery(id+"F16.opExtrude","SWEPT_FACE",FACE,{"disambiguationData":[OSD([sQuery(id+"F14.wireOp",EDGE,"E140.MirrorCS")])]});var subQ28=sQuery(id+"F0.wireOp",EDGE,"E0.right");var subQ29=sQuery(id+"F0.wireOp",EDGE,"E0.left");var subQ30=sQuery(id+"F0.wireOp",EDGE,"E0.top");var subQ31=sQuery(id+"F0.wireOp",EDGE,"E0.bottom");var subQ32=makeQuery(id+"F2.opShell","OFFSET_FACE",FACE,{"disambiguationData":[OSD([subQ31,subQ30,subQ29,subQ28]),TDD([makeQuery(id+"F1.opExtrude","CAP_FACE",FACE,{"disambiguationData":[OSD([subQ31,subQ30,subQ29,subQ28])],"isStart":false})])]});var subQ33=makeQuery(id+"F2.opShell","OFFSET_FACE",FACE,{"disambiguationData":[OSD([subQ29])]});var subQ34=makeQuery(id+"F16.opExtrude","SWEPT_FACE",FACE,{"disambiguationData":[OSD([sQuery(id+"F14.wireOp",EDGE,"E112")])]});var subQ35=makeQuery(id+"F16.boolean.opBoolean","COPY",FACE,{"derivedFrom":makeQuery(id+"F16.opExtrude","SWEPT_FACE",FACE,{"disambiguationData":[OSD([subQ15])]})});var subQ36=makeQuery(id+"F16.opExtrude","SWEPT_FACE",FACE,{"disambiguationData":[OSD([sQuery(id+"F14.wireOp",EDGE,"E144.MirrorCS")])]});var subQ37=makeQuery(id+"F2.opShell","OFFSET_FACE",FACE,{"disambiguationData":[OSD([subQ28])]});var subQ38=makeQuery(id+"F17.opExtrude","SWEPT_FACE",FACE,{"disambiguationData":[OSD([subQ0])]});var subQ39=makeQuery(id+"F16.opExtrude","SWEPT_FACE",FACE,{"disambiguationData":[OSD([sQuery(id+"F14.wireOp",EDGE,"E146.MirrorCS"),sQuery(id+"F14.wireOp",EDGE,"E149")])]});var subQ40=makeQuery(id+"F17.opExtrude","SWEPT_FACE",FACE,{"disambiguationData":[OSD([subQ17])]});var subQ41=makeQuery(id+"F24.opExtrude","SWEPT_FACE",FACE,{"disambiguationData":[OSD([sQuery(id+"F11.wireOp",EDGE,"E36")])]});var subQ42=makeQuery(id+"F17.opExtrude","SWEPT_FACE",FACE,{"disambiguationData":[OSD([subQ13])]});var subQ43=makeQuery(id+"F17.opExtrude","SWEPT_FACE",FACE,{"disambiguationData":[OSD([subQ11])]});var subQ44=makeQuery(id+"F17.opExtrude","SWEPT_FACE",FACE,{"disambiguationData":[OSD([subQ9])]});var subQ45=makeQuery(id+"F17.opExtrude","SWEPT_FACE",FACE,{"disambiguationData":[OSD([subQ7])]});var subQ46=makeQuery(id+"F17.opExtrude","SWEPT_FACE",FACE,{"disambiguationData":[OSD([subQ4])]});var subQ47=makeQuery(id+"F17.opExtrude","SWEPT_FACE",FACE,{"disambiguationData":[OSD([subQ2])]});var subQ48=makeQuery(id+"F23.boolean.opBoolean","COPY",FACE,{"derivedFrom":makeQuery(id+"F23.opExtrude","SWEPT_FACE",FACE,{"disambiguationData":[OSD([sQuery(id+"F11.wireOp",EDGE,"E30")])]})});var subQ49=sQuery(id+"F11.wireOp",EDGE,"E31");var subQ50=makeQuery(id+"F23.boolean.opBoolean","COPY",FACE,{"derivedFrom":makeQuery(id+"F23.opExtrude","SWEPT_FACE",FACE,{"disambiguationData":[OSD([subQ49])]})});var subQ51=makeQuery(id+"F23.boolean.opBoolean","COPY",FACE,{"derivedFrom":makeQuery(id+"F23.opExtrude","SWEPT_FACE",FACE,{"disambiguationData":[OSD([sQuery(id+"F11.wireOp",EDGE,"E33")])]})});var subQ52=makeQuery(id+"F24.opExtrude","SWEPT_FACE",FACE,{"disambiguationData":[OSD([sQuery(id+"F11.wireOp",EDGE,"E32")])]});var subQ53=makeQuery(id+"F24.opExtrude","SWEPT_FACE",FACE,{"disambiguationData":[OSD([sQuery(id+"F11.wireOp",EDGE,"E34")])]});var subQ54=makeQuery(id+"F15.opExtrude","CAP_FACE",FACE,{"disambiguationData":[OSD([subQ30,subQ29,subQ28,sQuery(id+"F12.wireOp",EDGE,"E86.0"),sQuery(id+"F12.wireOp",EDGE,"E97"),subQ21])],"isStart":false});Q0=makeQuery(id+"F26.boolean.opBoolean","SPLIT",FACE,{"disambiguationData":[TD([subQ33])],"derivedFrom":makeQuery(id+"F24.boolean.opBoolean","SPLIT",FACE,{"disambiguationData":[TD([makeQuery(id+"F2.opShell","OFFSET_FACE",FACE,{"disambiguationData":[OSD([subQ31,subQ30,subQ29,subQ28]),TDD([makeQuery(id+"F1.opExtrude","CAP_FACE",FACE,{"disambiguationData":[OSD([subQ31,subQ30,subQ29,subQ28])],"isStart":true})])]}),subQ32,subQ33,subQ37,subQ54,subQ22,subQ34,subQ23,subQ25,subQ27,subQ36,subQ39,subQ20,subQ18,subQ14,subQ12,subQ10,subQ8,subQ5,subQ3,subQ26,subQ35,subQ1,subQ24,subQ40,subQ42,subQ43,subQ44,subQ45,subQ46,subQ47,subQ16,subQ38,subQ6,makeQuery(id+"F18.opExtrude","SWEPT_FACE",FACE,{"disambiguationData":[OSD([sQuery(id+"F13.wireOp",EDGE,"E106")])]}),makeQuery(id+"F18.boolean.opBoolean","COPY",FACE,{"derivedFrom":makeQuery(id+"F18.opExtrude","SWEPT_FACE",FACE,{"disambiguationData":[OSD([sQuery(id+"F13.wireOp",EDGE,"E103")])]})}),makeQuery(id+"F18.boolean.opBoolean","COPY",FACE,{"derivedFrom":makeQuery(id+"F18.opExtrude","SWEPT_FACE",FACE,{"disambiguationData":[OSD([sQuery(id+"F13.wireOp",EDGE,"E104")])]})}),subQ48,subQ50,subQ51,makeQuery(id+"F23.boolean.opBoolean","COPY",FACE,{"derivedFrom":makeQuery(id+"F23.opExtrude","SWEPT_FACE",FACE,{"disambiguationData":[OSD([sQuery(id+"F11.wireOp",EDGE,"E42.MirrorCS")])]})}),makeQuery(id+"F23.boolean.opBoolean","COPY",FACE,{"derivedFrom":makeQuery(id+"F23.opExtrude","SWEPT_FACE",FACE,{"disambiguationData":[OSD([sQuery(id+"F11.wireOp",EDGE,"E45.MirrorCS")])]})}),makeQuery(id+"F23.boolean.opBoolean","COPY",FACE,{"derivedFrom":makeQuery(id+"F23.opExtrude","SWEPT_FACE",FACE,{"disambiguationData":[OSD([sQuery(id+"F11.wireOp",EDGE,"E46.MirrorCS")])]})}),makeQuery(id+"F23.boolean.opBoolean","COPY",FACE,{"derivedFrom":makeQuery(id+"F23.opExtrude","SWEPT_FACE",FACE,{"disambiguationData":[OSD([sQuery(id+"F11.wireOp",EDGE,"E57")])]})}),makeQuery(id+"F23.boolean.opBoolean","COPY",FACE,{"derivedFrom":makeQuery(id+"F23.opExtrude","SWEPT_FACE",FACE,{"disambiguationData":[OSD([sQuery(id+"F11.wireOp",EDGE,"E58")])]})}),makeQuery(id+"F23.boolean.opBoolean","COPY",FACE,{"derivedFrom":makeQuery(id+"F23.opExtrude","SWEPT_FACE",FACE,{"disambiguationData":[OSD([sQuery(id+"F11.wireOp",EDGE,"E59")])]})}),subQ52,subQ53,subQ41,makeQuery(id+"F24.opExtrude","SWEPT_FACE",FACE,{"disambiguationData":[OSD([sQuery(id+"F11.wireOp",EDGE,"E39.MirrorCS")])]}),makeQuery(id+"F24.opExtrude","SWEPT_FACE",FACE,{"disambiguationData":[OSD([sQuery(id+"F11.wireOp",EDGE,"E40.MirrorCS")])]}),makeQuery(id+"F24.opExtrude","SWEPT_FACE",FACE,{"disambiguationData":[OSD([sQuery(id+"F11.wireOp",EDGE,"E41.MirrorCS"),sQuery(id+"F11.wireOp",EDGE,"E52.trimOffspring")])]}),makeQuery(id+"F24.opExtrude","SWEPT_FACE",FACE,{"disambiguationData":[OSD([subQ31,subQ29])]})])],"derivedFrom":makeQuery(id+"F20.boolean.opBoolean","MERGE",FACE,{"derivedFrom":[subQ54],"fromTools":[makeQuery(id+"F20.opExtrude","CAP_FACE",FACE,{"disambiguationData":[OSD([sQuery(id+"F19.wireOp",EDGE,"E152.0"),sQuery(id+"F19.wireOp",EDGE,"E152.1"),sQuery(id+"F19.wireOp",EDGE,"E152.2"),sQuery(id+"F19.wireOp",EDGE,"E152.3"),sQuery(id+"F19.wireOp",EDGE,"E152.4"),sQuery(id+"F19.wireOp",EDGE,"E153"),sQuery(id+"F19.wireOp",EDGE,"E154"),sQuery(id+"F19.wireOp",EDGE,"E155")])],"isStart":true})]})})});}
            var Q1;
            {var subQ1=sQuery(id+"F14.wireOp",EDGE,"E132.MirrorCS");var subQ2=sQuery(id+"F19.wireOp",EDGE,"E155");var subQ3=sQuery(id+"F19.wireOp",EDGE,"E152.1");Q1=makeQuery(id+"F20.boolean.opBoolean","COPY",FACE,{"disambiguationData":[TD([makeQuery(id+"F16.boolean.opBoolean","COPY",FACE,{"derivedFrom":makeQuery(id+"F16.opExtrude","SWEPT_FACE",FACE,{"disambiguationData":[OSD([subQ1])]})})])],"derivedFrom":makeQuery(id+"F20.opExtrude","CAP_FACE",FACE,{"disambiguationData":[OSD([sQuery(id+"F19.wireOp",EDGE,"E152.0"),subQ3,sQuery(id+"F19.wireOp",EDGE,"E152.2"),sQuery(id+"F19.wireOp",EDGE,"E152.3"),sQuery(id+"F19.wireOp",EDGE,"E152.4"),sQuery(id+"F19.wireOp",EDGE,"E153"),sQuery(id+"F19.wireOp",EDGE,"E154"),subQ2])],"isStart":true})});}
            var Q2;
            {var subQ1=sQuery(id+"F14.wireOp",EDGE,"E134.MirrorCS");var subQ2=sQuery(id+"F19.wireOp",EDGE,"E155");var subQ3=sQuery(id+"F19.wireOp",EDGE,"E152.1");Q2=makeQuery(id+"F20.boolean.opBoolean","COPY",FACE,{"disambiguationData":[TD([makeQuery(id+"F16.boolean.opBoolean","COPY",FACE,{"derivedFrom":makeQuery(id+"F16.opExtrude","SWEPT_FACE",FACE,{"disambiguationData":[OSD([subQ1])]})})])],"derivedFrom":makeQuery(id+"F20.opExtrude","CAP_FACE",FACE,{"disambiguationData":[OSD([sQuery(id+"F19.wireOp",EDGE,"E152.0"),subQ3,sQuery(id+"F19.wireOp",EDGE,"E152.2"),sQuery(id+"F19.wireOp",EDGE,"E152.3"),sQuery(id+"F19.wireOp",EDGE,"E152.4"),sQuery(id+"F19.wireOp",EDGE,"E153"),sQuery(id+"F19.wireOp",EDGE,"E154"),subQ2])],"isStart":true})});}
            var Q3;
            {var subQ0=sQuery(id+"F0.wireOp",EDGE,"E0.bottom");Q3=makeQuery(id+"F2.opShell","OFFSET_EDGE",EDGE,{"disambiguationData":[OSD([subQ0]),TDD([makeQuery(id+"F1.opExtrude","CAP_EDGE",EDGE,{"disambiguationData":[OSD([subQ0])],"isStart":true})])]});}
            var Q4;
            Q4=makeQuery(id+"F2.opShell","OFFSET_EDGE",EDGE,{"disambiguationData":[OSD([sQuery(id+"F0.wireOp",EDGE,"E0.bottom"),sQuery(id+"F0.wireOp",EDGE,"E0.left")])]});
            var Q5;
            {var subQ0=sQuery(id+"F12.wireOp",EDGE,"E99");var subQ1=sQuery(id+"F0.wireOp",EDGE,"E0.right");var subQ2=sQuery(id+"F0.wireOp",EDGE,"E0.left");var subQ3=sQuery(id+"F0.wireOp",EDGE,"E0.top");var subQ4=makeQuery(id+"F15.opExtrude","CAP_FACE",FACE,{"disambiguationData":[OSD([subQ3,subQ2,subQ1,sQuery(id+"F12.wireOp",EDGE,"E86.0"),sQuery(id+"F12.wireOp",EDGE,"E97"),subQ0])],"isStart":false});var subQ5=sQuery(id+"F11.wireOp",EDGE,"E46.MirrorCS");var subQ6=makeQuery(id+"F23.boolean.opBoolean","COPY",FACE,{"derivedFrom":makeQuery(id+"F23.opExtrude","SWEPT_FACE",FACE,{"disambiguationData":[OSD([subQ5])]})});var subQ7=makeQuery(id+"F26.opExtrude","SWEPT_FACE",FACE,{"disambiguationData":[OSD([subQ5])]});var subQ8=sQuery(id+"F14.wireOp",EDGE,"E113");var subQ9=sQuery(id+"F14.wireOp",EDGE,"E111.top");var subQ10=sQuery(id+"F14.wireOp",EDGE,"E119");var subQ11=sQuery(id+"F14.wireOp",EDGE,"E118");var subQ12=sQuery(id+"F14.wireOp",EDGE,"E117");var subQ13=sQuery(id+"F14.wireOp",EDGE,"E115");var subQ14=sQuery(id+"F14.wireOp",EDGE,"E133.MirrorCS");var subQ15=sQuery(id+"F14.wireOp",EDGE,"E114");var subQ16=sQuery(id+"F14.wireOp",EDGE,"E111.right");var subQ17=sQuery(id+"F14.wireOp",EDGE,"E143.MirrorCS");var subQ18=sQuery(id+"F0.wireOp",EDGE,"E0.bottom");Q5=makeQuery(id+"F26.boolean.opBoolean","INTERSECT",EDGE,{"disambiguationData":[topologyDisambiguationEdgeConnected([subQ4,subQ6,subQ7])],"derivedFrom":[makeQuery(id+"F24.boolean.opBoolean","SPLIT",FACE,{"disambiguationData":[TD([makeQuery(id+"F2.opShell","OFFSET_FACE",FACE,{"disambiguationData":[OSD([subQ18,subQ3,subQ2,subQ1]),TDD([makeQuery(id+"F1.opExtrude","CAP_FACE",FACE,{"disambiguationData":[OSD([subQ18,subQ3,subQ2,subQ1])],"isStart":true})])]}),makeQuery(id+"F2.opShell","OFFSET_FACE",FACE,{"disambiguationData":[OSD([subQ18,subQ3,subQ2,subQ1]),TDD([makeQuery(id+"F1.opExtrude","CAP_FACE",FACE,{"disambiguationData":[OSD([subQ18,subQ3,subQ2,subQ1])],"isStart":false})])]}),makeQuery(id+"F2.opShell","OFFSET_FACE",FACE,{"disambiguationData":[OSD([subQ2])]}),makeQuery(id+"F2.opShell","OFFSET_FACE",FACE,{"disambiguationData":[OSD([subQ1])]}),subQ4,makeQuery(id+"F15.opExtrude","SWEPT_FACE",FACE,{"disambiguationData":[OSD([subQ0])]}),makeQuery(id+"F16.opExtrude","SWEPT_FACE",FACE,{"disambiguationData":[OSD([sQuery(id+"F14.wireOp",EDGE,"E112")])]}),makeQuery(id+"F16.opExtrude","SWEPT_FACE",FACE,{"disambiguationData":[OSD([sQuery(id+"F14.wireOp",EDGE,"E116")])]}),makeQuery(id+"F16.opExtrude","SWEPT_FACE",FACE,{"disambiguationData":[OSD([sQuery(id+"F14.wireOp",EDGE,"E120")])]}),makeQuery(id+"F16.opExtrude","SWEPT_FACE",FACE,{"disambiguationData":[OSD([sQuery(id+"F14.wireOp",EDGE,"E140.MirrorCS")])]}),makeQuery(id+"F16.opExtrude","SWEPT_FACE",FACE,{"disambiguationData":[OSD([sQuery(id+"F14.wireOp",EDGE,"E144.MirrorCS")])]}),makeQuery(id+"F16.opExtrude","SWEPT_FACE",FACE,{"disambiguationData":[OSD([sQuery(id+"F14.wireOp",EDGE,"E146.MirrorCS"),sQuery(id+"F14.wireOp",EDGE,"E149")])]}),makeQuery(id+"F16.boolean.opBoolean","COPY",FACE,{"derivedFrom":makeQuery(id+"F16.opExtrude","SWEPT_FACE",FACE,{"disambiguationData":[OSD([subQ9])]})}),makeQuery(id+"F16.boolean.opBoolean","COPY",FACE,{"derivedFrom":makeQuery(id+"F16.opExtrude","SWEPT_FACE",FACE,{"disambiguationData":[OSD([subQ16])]})}),makeQuery(id+"F16.boolean.opBoolean","COPY",FACE,{"derivedFrom":makeQuery(id+"F16.opExtrude","SWEPT_FACE",FACE,{"disambiguationData":[OSD([subQ8])]})}),makeQuery(id+"F16.boolean.opBoolean","COPY",FACE,{"derivedFrom":makeQuery(id+"F16.opExtrude","SWEPT_FACE",FACE,{"disambiguationData":[OSD([subQ15])]})}),makeQuery(id+"F16.boolean.opBoolean","COPY",FACE,{"derivedFrom":makeQuery(id+"F16.opExtrude","SWEPT_FACE",FACE,{"disambiguationData":[OSD([subQ13])]})}),makeQuery(id+"F16.boolean.opBoolean","COPY",FACE,{"derivedFrom":makeQuery(id+"F16.opExtrude","SWEPT_FACE",FACE,{"disambiguationData":[OSD([subQ12])]})}),makeQuery(id+"F16.boolean.opBoolean","COPY",FACE,{"derivedFrom":makeQuery(id+"F16.opExtrude","SWEPT_FACE",FACE,{"disambiguationData":[OSD([subQ11])]})}),makeQuery(id+"F16.boolean.opBoolean","COPY",FACE,{"derivedFrom":makeQuery(id+"F16.opExtrude","SWEPT_FACE",FACE,{"disambiguationData":[OSD([subQ10])]})}),makeQuery(id+"F16.boolean.opBoolean","COPY",FACE,{"derivedFrom":makeQuery(id+"F16.opExtrude","SWEPT_FACE",FACE,{"disambiguationData":[OSD([sQuery(id+"F14.wireOp",EDGE,"E127")])]})}),makeQuery(id+"F16.boolean.opBoolean","COPY",FACE,{"derivedFrom":makeQuery(id+"F16.opExtrude","SWEPT_FACE",FACE,{"disambiguationData":[OSD([subQ14])]})}),makeQuery(id+"F16.boolean.opBoolean","COPY",FACE,{"derivedFrom":makeQuery(id+"F16.opExtrude","SWEPT_FACE",FACE,{"disambiguationData":[OSD([subQ17])]})}),makeQuery(id+"F17.opExtrude","SWEPT_FACE",FACE,{"disambiguationData":[OSD([subQ9])]}),makeQuery(id+"F17.opExtrude","SWEPT_FACE",FACE,{"disambiguationData":[OSD([subQ16])]}),makeQuery(id+"F17.opExtrude","SWEPT_FACE",FACE,{"disambiguationData":[OSD([subQ8])]}),makeQuery(id+"F17.opExtrude","SWEPT_FACE",FACE,{"disambiguationData":[OSD([subQ15])]}),makeQuery(id+"F17.opExtrude","SWEPT_FACE",FACE,{"disambiguationData":[OSD([subQ13])]}),makeQuery(id+"F17.opExtrude","SWEPT_FACE",FACE,{"disambiguationData":[OSD([subQ12])]}),makeQuery(id+"F17.opExtrude","SWEPT_FACE",FACE,{"disambiguationData":[OSD([subQ11])]}),makeQuery(id+"F17.opExtrude","SWEPT_FACE",FACE,{"disambiguationData":[OSD([subQ10])]}),makeQuery(id+"F17.opExtrude","SWEPT_FACE",FACE,{"disambiguationData":[OSD([subQ14])]}),makeQuery(id+"F17.opExtrude","SWEPT_FACE",FACE,{"disambiguationData":[OSD([subQ17])]}),makeQuery(id+"F18.opExtrude","SWEPT_FACE",FACE,{"disambiguationData":[OSD([sQuery(id+"F13.wireOp",EDGE,"E105")])]}),makeQuery(id+"F18.opExtrude","SWEPT_FACE",FACE,{"disambiguationData":[OSD([sQuery(id+"F13.wireOp",EDGE,"E106")])]}),makeQuery(id+"F18.boolean.opBoolean","COPY",FACE,{"derivedFrom":makeQuery(id+"F18.opExtrude","SWEPT_FACE",FACE,{"disambiguationData":[OSD([sQuery(id+"F13.wireOp",EDGE,"E103")])]})}),makeQuery(id+"F18.boolean.opBoolean","COPY",FACE,{"derivedFrom":makeQuery(id+"F18.opExtrude","SWEPT_FACE",FACE,{"disambiguationData":[OSD([sQuery(id+"F13.wireOp",EDGE,"E104")])]})}),makeQuery(id+"F23.boolean.opBoolean","COPY",FACE,{"derivedFrom":makeQuery(id+"F23.opExtrude","SWEPT_FACE",FACE,{"disambiguationData":[OSD([sQuery(id+"F11.wireOp",EDGE,"E30")])]})}),makeQuery(id+"F23.boolean.opBoolean","COPY",FACE,{"derivedFrom":makeQuery(id+"F23.opExtrude","SWEPT_FACE",FACE,{"disambiguationData":[OSD([sQuery(id+"F11.wireOp",EDGE,"E31")])]})}),makeQuery(id+"F23.boolean.opBoolean","COPY",FACE,{"derivedFrom":makeQuery(id+"F23.opExtrude","SWEPT_FACE",FACE,{"disambiguationData":[OSD([sQuery(id+"F11.wireOp",EDGE,"E33")])]})}),makeQuery(id+"F23.boolean.opBoolean","COPY",FACE,{"derivedFrom":makeQuery(id+"F23.opExtrude","SWEPT_FACE",FACE,{"disambiguationData":[OSD([sQuery(id+"F11.wireOp",EDGE,"E42.MirrorCS")])]})}),makeQuery(id+"F23.boolean.opBoolean","COPY",FACE,{"derivedFrom":makeQuery(id+"F23.opExtrude","SWEPT_FACE",FACE,{"disambiguationData":[OSD([sQuery(id+"F11.wireOp",EDGE,"E45.MirrorCS")])]})}),subQ6,makeQuery(id+"F23.boolean.opBoolean","COPY",FACE,{"derivedFrom":makeQuery(id+"F23.opExtrude","SWEPT_FACE",FACE,{"disambiguationData":[OSD([sQuery(id+"F11.wireOp",EDGE,"E57")])]})}),makeQuery(id+"F23.boolean.opBoolean","COPY",FACE,{"derivedFrom":makeQuery(id+"F23.opExtrude","SWEPT_FACE",FACE,{"disambiguationData":[OSD([sQuery(id+"F11.wireOp",EDGE,"E58")])]})}),makeQuery(id+"F23.boolean.opBoolean","COPY",FACE,{"derivedFrom":makeQuery(id+"F23.opExtrude","SWEPT_FACE",FACE,{"disambiguationData":[OSD([sQuery(id+"F11.wireOp",EDGE,"E59")])]})}),makeQuery(id+"F24.opExtrude","SWEPT_FACE",FACE,{"disambiguationData":[OSD([sQuery(id+"F11.wireOp",EDGE,"E32")])]}),makeQuery(id+"F24.opExtrude","SWEPT_FACE",FACE,{"disambiguationData":[OSD([sQuery(id+"F11.wireOp",EDGE,"E34")])]}),makeQuery(id+"F24.opExtrude","SWEPT_FACE",FACE,{"disambiguationData":[OSD([sQuery(id+"F11.wireOp",EDGE,"E36")])]}),makeQuery(id+"F24.opExtrude","SWEPT_FACE",FACE,{"disambiguationData":[OSD([sQuery(id+"F11.wireOp",EDGE,"E39.MirrorCS")])]}),makeQuery(id+"F24.opExtrude","SWEPT_FACE",FACE,{"disambiguationData":[OSD([sQuery(id+"F11.wireOp",EDGE,"E40.MirrorCS")])]}),makeQuery(id+"F24.opExtrude","SWEPT_FACE",FACE,{"disambiguationData":[OSD([sQuery(id+"F11.wireOp",EDGE,"E41.MirrorCS"),sQuery(id+"F11.wireOp",EDGE,"E52.trimOffspring")])]}),makeQuery(id+"F24.opExtrude","SWEPT_FACE",FACE,{"disambiguationData":[OSD([subQ18,subQ2])]})])],"derivedFrom":makeQuery(id+"F20.boolean.opBoolean","MERGE",FACE,{"derivedFrom":[subQ4],"fromTools":[makeQuery(id+"F20.opExtrude","CAP_FACE",FACE,{"disambiguationData":[OSD([sQuery(id+"F19.wireOp",EDGE,"E152.0"),sQuery(id+"F19.wireOp",EDGE,"E152.1"),sQuery(id+"F19.wireOp",EDGE,"E152.2"),sQuery(id+"F19.wireOp",EDGE,"E152.3"),sQuery(id+"F19.wireOp",EDGE,"E152.4"),sQuery(id+"F19.wireOp",EDGE,"E153"),sQuery(id+"F19.wireOp",EDGE,"E154"),sQuery(id+"F19.wireOp",EDGE,"E155")])],"isStart":true})]})}),subQ7]});}
            var Q6;
            Q6=makeQuery(id+"F23.boolean.opBoolean","INTERSECT",EDGE,{"derivedFrom":[makeQuery(id+"F20.boolean.opBoolean","MERGE",FACE,{"derivedFrom":[makeQuery(id+"F15.opExtrude","CAP_FACE",FACE,{"disambiguationData":[OSD([sQuery(id+"F0.wireOp",EDGE,"E0.top"),sQuery(id+"F0.wireOp",EDGE,"E0.left"),sQuery(id+"F0.wireOp",EDGE,"E0.right"),sQuery(id+"F12.wireOp",EDGE,"E86.0"),sQuery(id+"F12.wireOp",EDGE,"E97"),sQuery(id+"F12.wireOp",EDGE,"E99")])],"isStart":false})],"fromTools":[makeQuery(id+"F20.opExtrude","CAP_FACE",FACE,{"disambiguationData":[OSD([sQuery(id+"F19.wireOp",EDGE,"E152.0"),sQuery(id+"F19.wireOp",EDGE,"E152.1"),sQuery(id+"F19.wireOp",EDGE,"E152.2"),sQuery(id+"F19.wireOp",EDGE,"E152.3"),sQuery(id+"F19.wireOp",EDGE,"E152.4"),sQuery(id+"F19.wireOp",EDGE,"E153"),sQuery(id+"F19.wireOp",EDGE,"E154"),sQuery(id+"F19.wireOp",EDGE,"E155")])],"isStart":true})]}),makeQuery(id+"F23.opExtrude","SWEPT_FACE",FACE,{"disambiguationData":[OSD([sQuery(id+"F11.wireOp",EDGE,"E45.MirrorCS")])]})]});
            var Q7;
            {var subQ0=sQuery(id+"F14.wireOp",EDGE,"E113");var subQ1=sQuery(id+"F14.wireOp",EDGE,"E111.top");var subQ2=sQuery(id+"F14.wireOp",EDGE,"E119");var subQ3=sQuery(id+"F14.wireOp",EDGE,"E118");var subQ4=sQuery(id+"F14.wireOp",EDGE,"E117");var subQ5=sQuery(id+"F14.wireOp",EDGE,"E115");var subQ6=sQuery(id+"F14.wireOp",EDGE,"E133.MirrorCS");var subQ7=sQuery(id+"F14.wireOp",EDGE,"E114");var subQ8=sQuery(id+"F14.wireOp",EDGE,"E111.right");var subQ9=sQuery(id+"F14.wireOp",EDGE,"E143.MirrorCS");var subQ10=sQuery(id+"F0.wireOp",EDGE,"E0.left");var subQ11=sQuery(id+"F12.wireOp",EDGE,"E99");var subQ12=sQuery(id+"F0.wireOp",EDGE,"E0.right");var subQ13=sQuery(id+"F0.wireOp",EDGE,"E0.top");var subQ14=makeQuery(id+"F15.opExtrude","CAP_FACE",FACE,{"disambiguationData":[OSD([subQ13,subQ10,subQ12,sQuery(id+"F12.wireOp",EDGE,"E86.0"),sQuery(id+"F12.wireOp",EDGE,"E97"),subQ11])],"isStart":false});var subQ15=sQuery(id+"F0.wireOp",EDGE,"E0.bottom");Q7=makeQuery(id+"F26.boolean.opBoolean","INTERSECT",EDGE,{"derivedFrom":[makeQuery(id+"F24.boolean.opBoolean","SPLIT",FACE,{"disambiguationData":[TD([makeQuery(id+"F2.opShell","OFFSET_FACE",FACE,{"disambiguationData":[OSD([subQ15,subQ13,subQ10,subQ12]),TDD([makeQuery(id+"F1.opExtrude","CAP_FACE",FACE,{"disambiguationData":[OSD([subQ15,subQ13,subQ10,subQ12])],"isStart":true})])]}),makeQuery(id+"F2.opShell","OFFSET_FACE",FACE,{"disambiguationData":[OSD([subQ15,subQ13,subQ10,subQ12]),TDD([makeQuery(id+"F1.opExtrude","CAP_FACE",FACE,{"disambiguationData":[OSD([subQ15,subQ13,subQ10,subQ12])],"isStart":false})])]}),makeQuery(id+"F2.opShell","OFFSET_FACE",FACE,{"disambiguationData":[OSD([subQ10])]}),makeQuery(id+"F2.opShell","OFFSET_FACE",FACE,{"disambiguationData":[OSD([subQ12])]}),subQ14,makeQuery(id+"F15.opExtrude","SWEPT_FACE",FACE,{"disambiguationData":[OSD([subQ11])]}),makeQuery(id+"F16.opExtrude","SWEPT_FACE",FACE,{"disambiguationData":[OSD([sQuery(id+"F14.wireOp",EDGE,"E112")])]}),makeQuery(id+"F16.opExtrude","SWEPT_FACE",FACE,{"disambiguationData":[OSD([sQuery(id+"F14.wireOp",EDGE,"E116")])]}),makeQuery(id+"F16.opExtrude","SWEPT_FACE",FACE,{"disambiguationData":[OSD([sQuery(id+"F14.wireOp",EDGE,"E120")])]}),makeQuery(id+"F16.opExtrude","SWEPT_FACE",FACE,{"disambiguationData":[OSD([sQuery(id+"F14.wireOp",EDGE,"E140.MirrorCS")])]}),makeQuery(id+"F16.opExtrude","SWEPT_FACE",FACE,{"disambiguationData":[OSD([sQuery(id+"F14.wireOp",EDGE,"E144.MirrorCS")])]}),makeQuery(id+"F16.opExtrude","SWEPT_FACE",FACE,{"disambiguationData":[OSD([sQuery(id+"F14.wireOp",EDGE,"E146.MirrorCS"),sQuery(id+"F14.wireOp",EDGE,"E149")])]}),makeQuery(id+"F16.boolean.opBoolean","COPY",FACE,{"derivedFrom":makeQuery(id+"F16.opExtrude","SWEPT_FACE",FACE,{"disambiguationData":[OSD([subQ1])]})}),makeQuery(id+"F16.boolean.opBoolean","COPY",FACE,{"derivedFrom":makeQuery(id+"F16.opExtrude","SWEPT_FACE",FACE,{"disambiguationData":[OSD([subQ8])]})}),makeQuery(id+"F16.boolean.opBoolean","COPY",FACE,{"derivedFrom":makeQuery(id+"F16.opExtrude","SWEPT_FACE",FACE,{"disambiguationData":[OSD([subQ0])]})}),makeQuery(id+"F16.boolean.opBoolean","COPY",FACE,{"derivedFrom":makeQuery(id+"F16.opExtrude","SWEPT_FACE",FACE,{"disambiguationData":[OSD([subQ7])]})}),makeQuery(id+"F16.boolean.opBoolean","COPY",FACE,{"derivedFrom":makeQuery(id+"F16.opExtrude","SWEPT_FACE",FACE,{"disambiguationData":[OSD([subQ5])]})}),makeQuery(id+"F16.boolean.opBoolean","COPY",FACE,{"derivedFrom":makeQuery(id+"F16.opExtrude","SWEPT_FACE",FACE,{"disambiguationData":[OSD([subQ4])]})}),makeQuery(id+"F16.boolean.opBoolean","COPY",FACE,{"derivedFrom":makeQuery(id+"F16.opExtrude","SWEPT_FACE",FACE,{"disambiguationData":[OSD([subQ3])]})}),makeQuery(id+"F16.boolean.opBoolean","COPY",FACE,{"derivedFrom":makeQuery(id+"F16.opExtrude","SWEPT_FACE",FACE,{"disambiguationData":[OSD([subQ2])]})}),makeQuery(id+"F16.boolean.opBoolean","COPY",FACE,{"derivedFrom":makeQuery(id+"F16.opExtrude","SWEPT_FACE",FACE,{"disambiguationData":[OSD([sQuery(id+"F14.wireOp",EDGE,"E127")])]})}),makeQuery(id+"F16.boolean.opBoolean","COPY",FACE,{"derivedFrom":makeQuery(id+"F16.opExtrude","SWEPT_FACE",FACE,{"disambiguationData":[OSD([subQ6])]})}),makeQuery(id+"F16.boolean.opBoolean","COPY",FACE,{"derivedFrom":makeQuery(id+"F16.opExtrude","SWEPT_FACE",FACE,{"disambiguationData":[OSD([subQ9])]})}),makeQuery(id+"F17.opExtrude","SWEPT_FACE",FACE,{"disambiguationData":[OSD([subQ1])]}),makeQuery(id+"F17.opExtrude","SWEPT_FACE",FACE,{"disambiguationData":[OSD([subQ8])]}),makeQuery(id+"F17.opExtrude","SWEPT_FACE",FACE,{"disambiguationData":[OSD([subQ0])]}),makeQuery(id+"F17.opExtrude","SWEPT_FACE",FACE,{"disambiguationData":[OSD([subQ7])]}),makeQuery(id+"F17.opExtrude","SWEPT_FACE",FACE,{"disambiguationData":[OSD([subQ5])]}),makeQuery(id+"F17.opExtrude","SWEPT_FACE",FACE,{"disambiguationData":[OSD([subQ4])]}),makeQuery(id+"F17.opExtrude","SWEPT_FACE",FACE,{"disambiguationData":[OSD([subQ3])]}),makeQuery(id+"F17.opExtrude","SWEPT_FACE",FACE,{"disambiguationData":[OSD([subQ2])]}),makeQuery(id+"F17.opExtrude","SWEPT_FACE",FACE,{"disambiguationData":[OSD([subQ6])]}),makeQuery(id+"F17.opExtrude","SWEPT_FACE",FACE,{"disambiguationData":[OSD([subQ9])]}),makeQuery(id+"F18.opExtrude","SWEPT_FACE",FACE,{"disambiguationData":[OSD([sQuery(id+"F13.wireOp",EDGE,"E105")])]}),makeQuery(id+"F18.opExtrude","SWEPT_FACE",FACE,{"disambiguationData":[OSD([sQuery(id+"F13.wireOp",EDGE,"E106")])]}),makeQuery(id+"F18.boolean.opBoolean","COPY",FACE,{"derivedFrom":makeQuery(id+"F18.opExtrude","SWEPT_FACE",FACE,{"disambiguationData":[OSD([sQuery(id+"F13.wireOp",EDGE,"E103")])]})}),makeQuery(id+"F18.boolean.opBoolean","COPY",FACE,{"derivedFrom":makeQuery(id+"F18.opExtrude","SWEPT_FACE",FACE,{"disambiguationData":[OSD([sQuery(id+"F13.wireOp",EDGE,"E104")])]})}),makeQuery(id+"F23.boolean.opBoolean","COPY",FACE,{"derivedFrom":makeQuery(id+"F23.opExtrude","SWEPT_FACE",FACE,{"disambiguationData":[OSD([sQuery(id+"F11.wireOp",EDGE,"E30")])]})}),makeQuery(id+"F23.boolean.opBoolean","COPY",FACE,{"derivedFrom":makeQuery(id+"F23.opExtrude","SWEPT_FACE",FACE,{"disambiguationData":[OSD([sQuery(id+"F11.wireOp",EDGE,"E31")])]})}),makeQuery(id+"F23.boolean.opBoolean","COPY",FACE,{"derivedFrom":makeQuery(id+"F23.opExtrude","SWEPT_FACE",FACE,{"disambiguationData":[OSD([sQuery(id+"F11.wireOp",EDGE,"E33")])]})}),makeQuery(id+"F23.boolean.opBoolean","COPY",FACE,{"derivedFrom":makeQuery(id+"F23.opExtrude","SWEPT_FACE",FACE,{"disambiguationData":[OSD([sQuery(id+"F11.wireOp",EDGE,"E42.MirrorCS")])]})}),makeQuery(id+"F23.boolean.opBoolean","COPY",FACE,{"derivedFrom":makeQuery(id+"F23.opExtrude","SWEPT_FACE",FACE,{"disambiguationData":[OSD([sQuery(id+"F11.wireOp",EDGE,"E45.MirrorCS")])]})}),makeQuery(id+"F23.boolean.opBoolean","COPY",FACE,{"derivedFrom":makeQuery(id+"F23.opExtrude","SWEPT_FACE",FACE,{"disambiguationData":[OSD([sQuery(id+"F11.wireOp",EDGE,"E46.MirrorCS")])]})}),makeQuery(id+"F23.boolean.opBoolean","COPY",FACE,{"derivedFrom":makeQuery(id+"F23.opExtrude","SWEPT_FACE",FACE,{"disambiguationData":[OSD([sQuery(id+"F11.wireOp",EDGE,"E57")])]})}),makeQuery(id+"F23.boolean.opBoolean","COPY",FACE,{"derivedFrom":makeQuery(id+"F23.opExtrude","SWEPT_FACE",FACE,{"disambiguationData":[OSD([sQuery(id+"F11.wireOp",EDGE,"E58")])]})}),makeQuery(id+"F23.boolean.opBoolean","COPY",FACE,{"derivedFrom":makeQuery(id+"F23.opExtrude","SWEPT_FACE",FACE,{"disambiguationData":[OSD([sQuery(id+"F11.wireOp",EDGE,"E59")])]})}),makeQuery(id+"F24.opExtrude","SWEPT_FACE",FACE,{"disambiguationData":[OSD([sQuery(id+"F11.wireOp",EDGE,"E32")])]}),makeQuery(id+"F24.opExtrude","SWEPT_FACE",FACE,{"disambiguationData":[OSD([sQuery(id+"F11.wireOp",EDGE,"E34")])]}),makeQuery(id+"F24.opExtrude","SWEPT_FACE",FACE,{"disambiguationData":[OSD([sQuery(id+"F11.wireOp",EDGE,"E36")])]}),makeQuery(id+"F24.opExtrude","SWEPT_FACE",FACE,{"disambiguationData":[OSD([sQuery(id+"F11.wireOp",EDGE,"E39.MirrorCS")])]}),makeQuery(id+"F24.opExtrude","SWEPT_FACE",FACE,{"disambiguationData":[OSD([sQuery(id+"F11.wireOp",EDGE,"E40.MirrorCS")])]}),makeQuery(id+"F24.opExtrude","SWEPT_FACE",FACE,{"disambiguationData":[OSD([sQuery(id+"F11.wireOp",EDGE,"E41.MirrorCS"),sQuery(id+"F11.wireOp",EDGE,"E52.trimOffspring")])]}),makeQuery(id+"F24.opExtrude","SWEPT_FACE",FACE,{"disambiguationData":[OSD([subQ15,subQ10])]})])],"derivedFrom":makeQuery(id+"F20.boolean.opBoolean","MERGE",FACE,{"derivedFrom":[subQ14],"fromTools":[makeQuery(id+"F20.opExtrude","CAP_FACE",FACE,{"disambiguationData":[OSD([sQuery(id+"F19.wireOp",EDGE,"E152.0"),sQuery(id+"F19.wireOp",EDGE,"E152.1"),sQuery(id+"F19.wireOp",EDGE,"E152.2"),sQuery(id+"F19.wireOp",EDGE,"E152.3"),sQuery(id+"F19.wireOp",EDGE,"E152.4"),sQuery(id+"F19.wireOp",EDGE,"E153"),sQuery(id+"F19.wireOp",EDGE,"E154"),sQuery(id+"F19.wireOp",EDGE,"E155")])],"isStart":true})]})}),makeQuery(id+"F26.opExtrude","SWEPT_FACE",FACE,{"disambiguationData":[OSD([sQuery(id+"F11.wireOp",EDGE,"E43.MirrorCS")])]})]});}
            var Q8;
            {var subQ0=sQuery(id+"F14.wireOp",EDGE,"E113");var subQ1=sQuery(id+"F14.wireOp",EDGE,"E111.top");var subQ2=sQuery(id+"F14.wireOp",EDGE,"E119");var subQ3=sQuery(id+"F14.wireOp",EDGE,"E118");var subQ4=sQuery(id+"F14.wireOp",EDGE,"E117");var subQ5=sQuery(id+"F14.wireOp",EDGE,"E115");var subQ6=sQuery(id+"F14.wireOp",EDGE,"E133.MirrorCS");var subQ7=sQuery(id+"F14.wireOp",EDGE,"E114");var subQ8=sQuery(id+"F14.wireOp",EDGE,"E111.right");var subQ9=sQuery(id+"F14.wireOp",EDGE,"E143.MirrorCS");var subQ10=sQuery(id+"F0.wireOp",EDGE,"E0.left");var subQ11=sQuery(id+"F12.wireOp",EDGE,"E99");var subQ12=sQuery(id+"F0.wireOp",EDGE,"E0.right");var subQ13=sQuery(id+"F0.wireOp",EDGE,"E0.top");var subQ14=makeQuery(id+"F15.opExtrude","CAP_FACE",FACE,{"disambiguationData":[OSD([subQ13,subQ10,subQ12,sQuery(id+"F12.wireOp",EDGE,"E86.0"),sQuery(id+"F12.wireOp",EDGE,"E97"),subQ11])],"isStart":false});var subQ15=sQuery(id+"F0.wireOp",EDGE,"E0.bottom");Q8=makeQuery(id+"F26.boolean.opBoolean","INTERSECT",EDGE,{"derivedFrom":[makeQuery(id+"F24.boolean.opBoolean","SPLIT",FACE,{"disambiguationData":[TD([makeQuery(id+"F2.opShell","OFFSET_FACE",FACE,{"disambiguationData":[OSD([subQ15,subQ13,subQ10,subQ12]),TDD([makeQuery(id+"F1.opExtrude","CAP_FACE",FACE,{"disambiguationData":[OSD([subQ15,subQ13,subQ10,subQ12])],"isStart":true})])]}),makeQuery(id+"F2.opShell","OFFSET_FACE",FACE,{"disambiguationData":[OSD([subQ15,subQ13,subQ10,subQ12]),TDD([makeQuery(id+"F1.opExtrude","CAP_FACE",FACE,{"disambiguationData":[OSD([subQ15,subQ13,subQ10,subQ12])],"isStart":false})])]}),makeQuery(id+"F2.opShell","OFFSET_FACE",FACE,{"disambiguationData":[OSD([subQ10])]}),makeQuery(id+"F2.opShell","OFFSET_FACE",FACE,{"disambiguationData":[OSD([subQ12])]}),subQ14,makeQuery(id+"F15.opExtrude","SWEPT_FACE",FACE,{"disambiguationData":[OSD([subQ11])]}),makeQuery(id+"F16.opExtrude","SWEPT_FACE",FACE,{"disambiguationData":[OSD([sQuery(id+"F14.wireOp",EDGE,"E112")])]}),makeQuery(id+"F16.opExtrude","SWEPT_FACE",FACE,{"disambiguationData":[OSD([sQuery(id+"F14.wireOp",EDGE,"E116")])]}),makeQuery(id+"F16.opExtrude","SWEPT_FACE",FACE,{"disambiguationData":[OSD([sQuery(id+"F14.wireOp",EDGE,"E120")])]}),makeQuery(id+"F16.opExtrude","SWEPT_FACE",FACE,{"disambiguationData":[OSD([sQuery(id+"F14.wireOp",EDGE,"E140.MirrorCS")])]}),makeQuery(id+"F16.opExtrude","SWEPT_FACE",FACE,{"disambiguationData":[OSD([sQuery(id+"F14.wireOp",EDGE,"E144.MirrorCS")])]}),makeQuery(id+"F16.opExtrude","SWEPT_FACE",FACE,{"disambiguationData":[OSD([sQuery(id+"F14.wireOp",EDGE,"E146.MirrorCS"),sQuery(id+"F14.wireOp",EDGE,"E149")])]}),makeQuery(id+"F16.boolean.opBoolean","COPY",FACE,{"derivedFrom":makeQuery(id+"F16.opExtrude","SWEPT_FACE",FACE,{"disambiguationData":[OSD([subQ1])]})}),makeQuery(id+"F16.boolean.opBoolean","COPY",FACE,{"derivedFrom":makeQuery(id+"F16.opExtrude","SWEPT_FACE",FACE,{"disambiguationData":[OSD([subQ8])]})}),makeQuery(id+"F16.boolean.opBoolean","COPY",FACE,{"derivedFrom":makeQuery(id+"F16.opExtrude","SWEPT_FACE",FACE,{"disambiguationData":[OSD([subQ0])]})}),makeQuery(id+"F16.boolean.opBoolean","COPY",FACE,{"derivedFrom":makeQuery(id+"F16.opExtrude","SWEPT_FACE",FACE,{"disambiguationData":[OSD([subQ7])]})}),makeQuery(id+"F16.boolean.opBoolean","COPY",FACE,{"derivedFrom":makeQuery(id+"F16.opExtrude","SWEPT_FACE",FACE,{"disambiguationData":[OSD([subQ5])]})}),makeQuery(id+"F16.boolean.opBoolean","COPY",FACE,{"derivedFrom":makeQuery(id+"F16.opExtrude","SWEPT_FACE",FACE,{"disambiguationData":[OSD([subQ4])]})}),makeQuery(id+"F16.boolean.opBoolean","COPY",FACE,{"derivedFrom":makeQuery(id+"F16.opExtrude","SWEPT_FACE",FACE,{"disambiguationData":[OSD([subQ3])]})}),makeQuery(id+"F16.boolean.opBoolean","COPY",FACE,{"derivedFrom":makeQuery(id+"F16.opExtrude","SWEPT_FACE",FACE,{"disambiguationData":[OSD([subQ2])]})}),makeQuery(id+"F16.boolean.opBoolean","COPY",FACE,{"derivedFrom":makeQuery(id+"F16.opExtrude","SWEPT_FACE",FACE,{"disambiguationData":[OSD([sQuery(id+"F14.wireOp",EDGE,"E127")])]})}),makeQuery(id+"F16.boolean.opBoolean","COPY",FACE,{"derivedFrom":makeQuery(id+"F16.opExtrude","SWEPT_FACE",FACE,{"disambiguationData":[OSD([subQ6])]})}),makeQuery(id+"F16.boolean.opBoolean","COPY",FACE,{"derivedFrom":makeQuery(id+"F16.opExtrude","SWEPT_FACE",FACE,{"disambiguationData":[OSD([subQ9])]})}),makeQuery(id+"F17.opExtrude","SWEPT_FACE",FACE,{"disambiguationData":[OSD([subQ1])]}),makeQuery(id+"F17.opExtrude","SWEPT_FACE",FACE,{"disambiguationData":[OSD([subQ8])]}),makeQuery(id+"F17.opExtrude","SWEPT_FACE",FACE,{"disambiguationData":[OSD([subQ0])]}),makeQuery(id+"F17.opExtrude","SWEPT_FACE",FACE,{"disambiguationData":[OSD([subQ7])]}),makeQuery(id+"F17.opExtrude","SWEPT_FACE",FACE,{"disambiguationData":[OSD([subQ5])]}),makeQuery(id+"F17.opExtrude","SWEPT_FACE",FACE,{"disambiguationData":[OSD([subQ4])]}),makeQuery(id+"F17.opExtrude","SWEPT_FACE",FACE,{"disambiguationData":[OSD([subQ3])]}),makeQuery(id+"F17.opExtrude","SWEPT_FACE",FACE,{"disambiguationData":[OSD([subQ2])]}),makeQuery(id+"F17.opExtrude","SWEPT_FACE",FACE,{"disambiguationData":[OSD([subQ6])]}),makeQuery(id+"F17.opExtrude","SWEPT_FACE",FACE,{"disambiguationData":[OSD([subQ9])]}),makeQuery(id+"F18.opExtrude","SWEPT_FACE",FACE,{"disambiguationData":[OSD([sQuery(id+"F13.wireOp",EDGE,"E105")])]}),makeQuery(id+"F18.opExtrude","SWEPT_FACE",FACE,{"disambiguationData":[OSD([sQuery(id+"F13.wireOp",EDGE,"E106")])]}),makeQuery(id+"F18.boolean.opBoolean","COPY",FACE,{"derivedFrom":makeQuery(id+"F18.opExtrude","SWEPT_FACE",FACE,{"disambiguationData":[OSD([sQuery(id+"F13.wireOp",EDGE,"E103")])]})}),makeQuery(id+"F18.boolean.opBoolean","COPY",FACE,{"derivedFrom":makeQuery(id+"F18.opExtrude","SWEPT_FACE",FACE,{"disambiguationData":[OSD([sQuery(id+"F13.wireOp",EDGE,"E104")])]})}),makeQuery(id+"F23.boolean.opBoolean","COPY",FACE,{"derivedFrom":makeQuery(id+"F23.opExtrude","SWEPT_FACE",FACE,{"disambiguationData":[OSD([sQuery(id+"F11.wireOp",EDGE,"E30")])]})}),makeQuery(id+"F23.boolean.opBoolean","COPY",FACE,{"derivedFrom":makeQuery(id+"F23.opExtrude","SWEPT_FACE",FACE,{"disambiguationData":[OSD([sQuery(id+"F11.wireOp",EDGE,"E31")])]})}),makeQuery(id+"F23.boolean.opBoolean","COPY",FACE,{"derivedFrom":makeQuery(id+"F23.opExtrude","SWEPT_FACE",FACE,{"disambiguationData":[OSD([sQuery(id+"F11.wireOp",EDGE,"E33")])]})}),makeQuery(id+"F23.boolean.opBoolean","COPY",FACE,{"derivedFrom":makeQuery(id+"F23.opExtrude","SWEPT_FACE",FACE,{"disambiguationData":[OSD([sQuery(id+"F11.wireOp",EDGE,"E42.MirrorCS")])]})}),makeQuery(id+"F23.boolean.opBoolean","COPY",FACE,{"derivedFrom":makeQuery(id+"F23.opExtrude","SWEPT_FACE",FACE,{"disambiguationData":[OSD([sQuery(id+"F11.wireOp",EDGE,"E45.MirrorCS")])]})}),makeQuery(id+"F23.boolean.opBoolean","COPY",FACE,{"derivedFrom":makeQuery(id+"F23.opExtrude","SWEPT_FACE",FACE,{"disambiguationData":[OSD([sQuery(id+"F11.wireOp",EDGE,"E46.MirrorCS")])]})}),makeQuery(id+"F23.boolean.opBoolean","COPY",FACE,{"derivedFrom":makeQuery(id+"F23.opExtrude","SWEPT_FACE",FACE,{"disambiguationData":[OSD([sQuery(id+"F11.wireOp",EDGE,"E57")])]})}),makeQuery(id+"F23.boolean.opBoolean","COPY",FACE,{"derivedFrom":makeQuery(id+"F23.opExtrude","SWEPT_FACE",FACE,{"disambiguationData":[OSD([sQuery(id+"F11.wireOp",EDGE,"E58")])]})}),makeQuery(id+"F23.boolean.opBoolean","COPY",FACE,{"derivedFrom":makeQuery(id+"F23.opExtrude","SWEPT_FACE",FACE,{"disambiguationData":[OSD([sQuery(id+"F11.wireOp",EDGE,"E59")])]})}),makeQuery(id+"F24.opExtrude","SWEPT_FACE",FACE,{"disambiguationData":[OSD([sQuery(id+"F11.wireOp",EDGE,"E32")])]}),makeQuery(id+"F24.opExtrude","SWEPT_FACE",FACE,{"disambiguationData":[OSD([sQuery(id+"F11.wireOp",EDGE,"E34")])]}),makeQuery(id+"F24.opExtrude","SWEPT_FACE",FACE,{"disambiguationData":[OSD([sQuery(id+"F11.wireOp",EDGE,"E36")])]}),makeQuery(id+"F24.opExtrude","SWEPT_FACE",FACE,{"disambiguationData":[OSD([sQuery(id+"F11.wireOp",EDGE,"E39.MirrorCS")])]}),makeQuery(id+"F24.opExtrude","SWEPT_FACE",FACE,{"disambiguationData":[OSD([sQuery(id+"F11.wireOp",EDGE,"E40.MirrorCS")])]}),makeQuery(id+"F24.opExtrude","SWEPT_FACE",FACE,{"disambiguationData":[OSD([sQuery(id+"F11.wireOp",EDGE,"E41.MirrorCS"),sQuery(id+"F11.wireOp",EDGE,"E52.trimOffspring")])]}),makeQuery(id+"F24.opExtrude","SWEPT_FACE",FACE,{"disambiguationData":[OSD([subQ15,subQ10])]})])],"derivedFrom":makeQuery(id+"F20.boolean.opBoolean","MERGE",FACE,{"derivedFrom":[subQ14],"fromTools":[makeQuery(id+"F20.opExtrude","CAP_FACE",FACE,{"disambiguationData":[OSD([sQuery(id+"F19.wireOp",EDGE,"E152.0"),sQuery(id+"F19.wireOp",EDGE,"E152.1"),sQuery(id+"F19.wireOp",EDGE,"E152.2"),sQuery(id+"F19.wireOp",EDGE,"E152.3"),sQuery(id+"F19.wireOp",EDGE,"E152.4"),sQuery(id+"F19.wireOp",EDGE,"E153"),sQuery(id+"F19.wireOp",EDGE,"E154"),sQuery(id+"F19.wireOp",EDGE,"E155")])],"isStart":true})]})}),makeQuery(id+"F26.opExtrude","SWEPT_FACE",FACE,{"disambiguationData":[OSD([sQuery(id+"F11.wireOp",EDGE,"E47.MirrorCS")])]})]});}
            var Q9;
            Q9=makeQuery(id+"F23.boolean.opBoolean","INTERSECT",EDGE,{"derivedFrom":[makeQuery(id+"F20.boolean.opBoolean","MERGE",FACE,{"derivedFrom":[makeQuery(id+"F15.opExtrude","CAP_FACE",FACE,{"disambiguationData":[OSD([sQuery(id+"F0.wireOp",EDGE,"E0.top"),sQuery(id+"F0.wireOp",EDGE,"E0.left"),sQuery(id+"F0.wireOp",EDGE,"E0.right"),sQuery(id+"F12.wireOp",EDGE,"E86.0"),sQuery(id+"F12.wireOp",EDGE,"E97"),sQuery(id+"F12.wireOp",EDGE,"E99")])],"isStart":false})],"fromTools":[makeQuery(id+"F20.opExtrude","CAP_FACE",FACE,{"disambiguationData":[OSD([sQuery(id+"F19.wireOp",EDGE,"E152.0"),sQuery(id+"F19.wireOp",EDGE,"E152.1"),sQuery(id+"F19.wireOp",EDGE,"E152.2"),sQuery(id+"F19.wireOp",EDGE,"E152.3"),sQuery(id+"F19.wireOp",EDGE,"E152.4"),sQuery(id+"F19.wireOp",EDGE,"E153"),sQuery(id+"F19.wireOp",EDGE,"E154"),sQuery(id+"F19.wireOp",EDGE,"E155")])],"isStart":true})]}),makeQuery(id+"F23.opExtrude","SWEPT_FACE",FACE,{"disambiguationData":[OSD([sQuery(id+"F11.wireOp",EDGE,"E42.MirrorCS")])]})]});
            var Q10;
            Q10=makeQuery(id+"F24.boolean.opBoolean","INTERSECT",EDGE,{"derivedFrom":[makeQuery(id+"F20.boolean.opBoolean","MERGE",FACE,{"derivedFrom":[makeQuery(id+"F15.opExtrude","CAP_FACE",FACE,{"disambiguationData":[OSD([sQuery(id+"F0.wireOp",EDGE,"E0.top"),sQuery(id+"F0.wireOp",EDGE,"E0.left"),sQuery(id+"F0.wireOp",EDGE,"E0.right"),sQuery(id+"F12.wireOp",EDGE,"E86.0"),sQuery(id+"F12.wireOp",EDGE,"E97"),sQuery(id+"F12.wireOp",EDGE,"E99")])],"isStart":false})],"fromTools":[makeQuery(id+"F20.opExtrude","CAP_FACE",FACE,{"disambiguationData":[OSD([sQuery(id+"F19.wireOp",EDGE,"E152.0"),sQuery(id+"F19.wireOp",EDGE,"E152.1"),sQuery(id+"F19.wireOp",EDGE,"E152.2"),sQuery(id+"F19.wireOp",EDGE,"E152.3"),sQuery(id+"F19.wireOp",EDGE,"E152.4"),sQuery(id+"F19.wireOp",EDGE,"E153"),sQuery(id+"F19.wireOp",EDGE,"E154"),sQuery(id+"F19.wireOp",EDGE,"E155")])],"isStart":true})]}),makeQuery(id+"F24.opExtrude","SWEPT_FACE",FACE,{"disambiguationData":[OSD([sQuery(id+"F11.wireOp",EDGE,"E39.MirrorCS")])]})]});
            var Q11;
            Q11=makeQuery(id+"F24.boolean.opBoolean","INTERSECT",EDGE,{"derivedFrom":[makeQuery(id+"F20.boolean.opBoolean","MERGE",FACE,{"derivedFrom":[makeQuery(id+"F15.opExtrude","CAP_FACE",FACE,{"disambiguationData":[OSD([sQuery(id+"F0.wireOp",EDGE,"E0.top"),sQuery(id+"F0.wireOp",EDGE,"E0.left"),sQuery(id+"F0.wireOp",EDGE,"E0.right"),sQuery(id+"F12.wireOp",EDGE,"E86.0"),sQuery(id+"F12.wireOp",EDGE,"E97"),sQuery(id+"F12.wireOp",EDGE,"E99")])],"isStart":false})],"fromTools":[makeQuery(id+"F20.opExtrude","CAP_FACE",FACE,{"disambiguationData":[OSD([sQuery(id+"F19.wireOp",EDGE,"E152.0"),sQuery(id+"F19.wireOp",EDGE,"E152.1"),sQuery(id+"F19.wireOp",EDGE,"E152.2"),sQuery(id+"F19.wireOp",EDGE,"E152.3"),sQuery(id+"F19.wireOp",EDGE,"E152.4"),sQuery(id+"F19.wireOp",EDGE,"E153"),sQuery(id+"F19.wireOp",EDGE,"E154"),sQuery(id+"F19.wireOp",EDGE,"E155")])],"isStart":true})]}),makeQuery(id+"F24.opExtrude","SWEPT_FACE",FACE,{"disambiguationData":[OSD([sQuery(id+"F11.wireOp",EDGE,"E40.MirrorCS")])]})]});
            var Q12;
            Q12=makeQuery(id+"F24.boolean.opBoolean","INTERSECT",EDGE,{"disambiguationData":[OD(0.0)],"derivedFrom":[makeQuery(id+"F20.boolean.opBoolean","MERGE",FACE,{"derivedFrom":[makeQuery(id+"F15.opExtrude","CAP_FACE",FACE,{"disambiguationData":[OSD([sQuery(id+"F0.wireOp",EDGE,"E0.top"),sQuery(id+"F0.wireOp",EDGE,"E0.left"),sQuery(id+"F0.wireOp",EDGE,"E0.right"),sQuery(id+"F12.wireOp",EDGE,"E86.0"),sQuery(id+"F12.wireOp",EDGE,"E97"),sQuery(id+"F12.wireOp",EDGE,"E99")])],"isStart":false})],"fromTools":[makeQuery(id+"F20.opExtrude","CAP_FACE",FACE,{"disambiguationData":[OSD([sQuery(id+"F19.wireOp",EDGE,"E152.0"),sQuery(id+"F19.wireOp",EDGE,"E152.1"),sQuery(id+"F19.wireOp",EDGE,"E152.2"),sQuery(id+"F19.wireOp",EDGE,"E152.3"),sQuery(id+"F19.wireOp",EDGE,"E152.4"),sQuery(id+"F19.wireOp",EDGE,"E153"),sQuery(id+"F19.wireOp",EDGE,"E154"),sQuery(id+"F19.wireOp",EDGE,"E155")])],"isStart":true})]}),makeQuery(id+"F24.opExtrude","SWEPT_FACE",FACE,{"disambiguationData":[OSD([sQuery(id+"F11.wireOp",EDGE,"E41.MirrorCS"),sQuery(id+"F11.wireOp",EDGE,"E52.trimOffspring")])]})]});
            var Q13;
            {var subQ0=sQuery(id+"F14.wireOp",EDGE,"E113");var subQ1=sQuery(id+"F14.wireOp",EDGE,"E111.top");var subQ2=sQuery(id+"F14.wireOp",EDGE,"E119");var subQ3=sQuery(id+"F14.wireOp",EDGE,"E118");var subQ4=sQuery(id+"F14.wireOp",EDGE,"E117");var subQ5=sQuery(id+"F14.wireOp",EDGE,"E115");var subQ6=sQuery(id+"F14.wireOp",EDGE,"E133.MirrorCS");var subQ7=sQuery(id+"F14.wireOp",EDGE,"E114");var subQ8=sQuery(id+"F14.wireOp",EDGE,"E111.right");var subQ9=sQuery(id+"F14.wireOp",EDGE,"E143.MirrorCS");var subQ10=sQuery(id+"F0.wireOp",EDGE,"E0.left");var subQ11=sQuery(id+"F12.wireOp",EDGE,"E99");var subQ12=sQuery(id+"F0.wireOp",EDGE,"E0.right");var subQ13=sQuery(id+"F0.wireOp",EDGE,"E0.top");var subQ14=makeQuery(id+"F15.opExtrude","CAP_FACE",FACE,{"disambiguationData":[OSD([subQ13,subQ10,subQ12,sQuery(id+"F12.wireOp",EDGE,"E86.0"),sQuery(id+"F12.wireOp",EDGE,"E97"),subQ11])],"isStart":false});var subQ15=sQuery(id+"F0.wireOp",EDGE,"E0.bottom");Q13=makeQuery(id+"F26.boolean.opBoolean","INTERSECT",EDGE,{"disambiguationData":[OD(0.0)],"derivedFrom":[makeQuery(id+"F24.boolean.opBoolean","SPLIT",FACE,{"disambiguationData":[TD([makeQuery(id+"F2.opShell","OFFSET_FACE",FACE,{"disambiguationData":[OSD([subQ15,subQ13,subQ10,subQ12]),TDD([makeQuery(id+"F1.opExtrude","CAP_FACE",FACE,{"disambiguationData":[OSD([subQ15,subQ13,subQ10,subQ12])],"isStart":true})])]}),makeQuery(id+"F2.opShell","OFFSET_FACE",FACE,{"disambiguationData":[OSD([subQ15,subQ13,subQ10,subQ12]),TDD([makeQuery(id+"F1.opExtrude","CAP_FACE",FACE,{"disambiguationData":[OSD([subQ15,subQ13,subQ10,subQ12])],"isStart":false})])]}),makeQuery(id+"F2.opShell","OFFSET_FACE",FACE,{"disambiguationData":[OSD([subQ10])]}),makeQuery(id+"F2.opShell","OFFSET_FACE",FACE,{"disambiguationData":[OSD([subQ12])]}),subQ14,makeQuery(id+"F15.opExtrude","SWEPT_FACE",FACE,{"disambiguationData":[OSD([subQ11])]}),makeQuery(id+"F16.opExtrude","SWEPT_FACE",FACE,{"disambiguationData":[OSD([sQuery(id+"F14.wireOp",EDGE,"E112")])]}),makeQuery(id+"F16.opExtrude","SWEPT_FACE",FACE,{"disambiguationData":[OSD([sQuery(id+"F14.wireOp",EDGE,"E116")])]}),makeQuery(id+"F16.opExtrude","SWEPT_FACE",FACE,{"disambiguationData":[OSD([sQuery(id+"F14.wireOp",EDGE,"E120")])]}),makeQuery(id+"F16.opExtrude","SWEPT_FACE",FACE,{"disambiguationData":[OSD([sQuery(id+"F14.wireOp",EDGE,"E140.MirrorCS")])]}),makeQuery(id+"F16.opExtrude","SWEPT_FACE",FACE,{"disambiguationData":[OSD([sQuery(id+"F14.wireOp",EDGE,"E144.MirrorCS")])]}),makeQuery(id+"F16.opExtrude","SWEPT_FACE",FACE,{"disambiguationData":[OSD([sQuery(id+"F14.wireOp",EDGE,"E146.MirrorCS"),sQuery(id+"F14.wireOp",EDGE,"E149")])]}),makeQuery(id+"F16.boolean.opBoolean","COPY",FACE,{"derivedFrom":makeQuery(id+"F16.opExtrude","SWEPT_FACE",FACE,{"disambiguationData":[OSD([subQ1])]})}),makeQuery(id+"F16.boolean.opBoolean","COPY",FACE,{"derivedFrom":makeQuery(id+"F16.opExtrude","SWEPT_FACE",FACE,{"disambiguationData":[OSD([subQ8])]})}),makeQuery(id+"F16.boolean.opBoolean","COPY",FACE,{"derivedFrom":makeQuery(id+"F16.opExtrude","SWEPT_FACE",FACE,{"disambiguationData":[OSD([subQ0])]})}),makeQuery(id+"F16.boolean.opBoolean","COPY",FACE,{"derivedFrom":makeQuery(id+"F16.opExtrude","SWEPT_FACE",FACE,{"disambiguationData":[OSD([subQ7])]})}),makeQuery(id+"F16.boolean.opBoolean","COPY",FACE,{"derivedFrom":makeQuery(id+"F16.opExtrude","SWEPT_FACE",FACE,{"disambiguationData":[OSD([subQ5])]})}),makeQuery(id+"F16.boolean.opBoolean","COPY",FACE,{"derivedFrom":makeQuery(id+"F16.opExtrude","SWEPT_FACE",FACE,{"disambiguationData":[OSD([subQ4])]})}),makeQuery(id+"F16.boolean.opBoolean","COPY",FACE,{"derivedFrom":makeQuery(id+"F16.opExtrude","SWEPT_FACE",FACE,{"disambiguationData":[OSD([subQ3])]})}),makeQuery(id+"F16.boolean.opBoolean","COPY",FACE,{"derivedFrom":makeQuery(id+"F16.opExtrude","SWEPT_FACE",FACE,{"disambiguationData":[OSD([subQ2])]})}),makeQuery(id+"F16.boolean.opBoolean","COPY",FACE,{"derivedFrom":makeQuery(id+"F16.opExtrude","SWEPT_FACE",FACE,{"disambiguationData":[OSD([sQuery(id+"F14.wireOp",EDGE,"E127")])]})}),makeQuery(id+"F16.boolean.opBoolean","COPY",FACE,{"derivedFrom":makeQuery(id+"F16.opExtrude","SWEPT_FACE",FACE,{"disambiguationData":[OSD([subQ6])]})}),makeQuery(id+"F16.boolean.opBoolean","COPY",FACE,{"derivedFrom":makeQuery(id+"F16.opExtrude","SWEPT_FACE",FACE,{"disambiguationData":[OSD([subQ9])]})}),makeQuery(id+"F17.opExtrude","SWEPT_FACE",FACE,{"disambiguationData":[OSD([subQ1])]}),makeQuery(id+"F17.opExtrude","SWEPT_FACE",FACE,{"disambiguationData":[OSD([subQ8])]}),makeQuery(id+"F17.opExtrude","SWEPT_FACE",FACE,{"disambiguationData":[OSD([subQ0])]}),makeQuery(id+"F17.opExtrude","SWEPT_FACE",FACE,{"disambiguationData":[OSD([subQ7])]}),makeQuery(id+"F17.opExtrude","SWEPT_FACE",FACE,{"disambiguationData":[OSD([subQ5])]}),makeQuery(id+"F17.opExtrude","SWEPT_FACE",FACE,{"disambiguationData":[OSD([subQ4])]}),makeQuery(id+"F17.opExtrude","SWEPT_FACE",FACE,{"disambiguationData":[OSD([subQ3])]}),makeQuery(id+"F17.opExtrude","SWEPT_FACE",FACE,{"disambiguationData":[OSD([subQ2])]}),makeQuery(id+"F17.opExtrude","SWEPT_FACE",FACE,{"disambiguationData":[OSD([subQ6])]}),makeQuery(id+"F17.opExtrude","SWEPT_FACE",FACE,{"disambiguationData":[OSD([subQ9])]}),makeQuery(id+"F18.opExtrude","SWEPT_FACE",FACE,{"disambiguationData":[OSD([sQuery(id+"F13.wireOp",EDGE,"E105")])]}),makeQuery(id+"F18.opExtrude","SWEPT_FACE",FACE,{"disambiguationData":[OSD([sQuery(id+"F13.wireOp",EDGE,"E106")])]}),makeQuery(id+"F18.boolean.opBoolean","COPY",FACE,{"derivedFrom":makeQuery(id+"F18.opExtrude","SWEPT_FACE",FACE,{"disambiguationData":[OSD([sQuery(id+"F13.wireOp",EDGE,"E103")])]})}),makeQuery(id+"F18.boolean.opBoolean","COPY",FACE,{"derivedFrom":makeQuery(id+"F18.opExtrude","SWEPT_FACE",FACE,{"disambiguationData":[OSD([sQuery(id+"F13.wireOp",EDGE,"E104")])]})}),makeQuery(id+"F23.boolean.opBoolean","COPY",FACE,{"derivedFrom":makeQuery(id+"F23.opExtrude","SWEPT_FACE",FACE,{"disambiguationData":[OSD([sQuery(id+"F11.wireOp",EDGE,"E30")])]})}),makeQuery(id+"F23.boolean.opBoolean","COPY",FACE,{"derivedFrom":makeQuery(id+"F23.opExtrude","SWEPT_FACE",FACE,{"disambiguationData":[OSD([sQuery(id+"F11.wireOp",EDGE,"E31")])]})}),makeQuery(id+"F23.boolean.opBoolean","COPY",FACE,{"derivedFrom":makeQuery(id+"F23.opExtrude","SWEPT_FACE",FACE,{"disambiguationData":[OSD([sQuery(id+"F11.wireOp",EDGE,"E33")])]})}),makeQuery(id+"F23.boolean.opBoolean","COPY",FACE,{"derivedFrom":makeQuery(id+"F23.opExtrude","SWEPT_FACE",FACE,{"disambiguationData":[OSD([sQuery(id+"F11.wireOp",EDGE,"E42.MirrorCS")])]})}),makeQuery(id+"F23.boolean.opBoolean","COPY",FACE,{"derivedFrom":makeQuery(id+"F23.opExtrude","SWEPT_FACE",FACE,{"disambiguationData":[OSD([sQuery(id+"F11.wireOp",EDGE,"E45.MirrorCS")])]})}),makeQuery(id+"F23.boolean.opBoolean","COPY",FACE,{"derivedFrom":makeQuery(id+"F23.opExtrude","SWEPT_FACE",FACE,{"disambiguationData":[OSD([sQuery(id+"F11.wireOp",EDGE,"E46.MirrorCS")])]})}),makeQuery(id+"F23.boolean.opBoolean","COPY",FACE,{"derivedFrom":makeQuery(id+"F23.opExtrude","SWEPT_FACE",FACE,{"disambiguationData":[OSD([sQuery(id+"F11.wireOp",EDGE,"E57")])]})}),makeQuery(id+"F23.boolean.opBoolean","COPY",FACE,{"derivedFrom":makeQuery(id+"F23.opExtrude","SWEPT_FACE",FACE,{"disambiguationData":[OSD([sQuery(id+"F11.wireOp",EDGE,"E58")])]})}),makeQuery(id+"F23.boolean.opBoolean","COPY",FACE,{"derivedFrom":makeQuery(id+"F23.opExtrude","SWEPT_FACE",FACE,{"disambiguationData":[OSD([sQuery(id+"F11.wireOp",EDGE,"E59")])]})}),makeQuery(id+"F24.opExtrude","SWEPT_FACE",FACE,{"disambiguationData":[OSD([sQuery(id+"F11.wireOp",EDGE,"E32")])]}),makeQuery(id+"F24.opExtrude","SWEPT_FACE",FACE,{"disambiguationData":[OSD([sQuery(id+"F11.wireOp",EDGE,"E34")])]}),makeQuery(id+"F24.opExtrude","SWEPT_FACE",FACE,{"disambiguationData":[OSD([sQuery(id+"F11.wireOp",EDGE,"E36")])]}),makeQuery(id+"F24.opExtrude","SWEPT_FACE",FACE,{"disambiguationData":[OSD([sQuery(id+"F11.wireOp",EDGE,"E39.MirrorCS")])]}),makeQuery(id+"F24.opExtrude","SWEPT_FACE",FACE,{"disambiguationData":[OSD([sQuery(id+"F11.wireOp",EDGE,"E40.MirrorCS")])]}),makeQuery(id+"F24.opExtrude","SWEPT_FACE",FACE,{"disambiguationData":[OSD([sQuery(id+"F11.wireOp",EDGE,"E41.MirrorCS"),sQuery(id+"F11.wireOp",EDGE,"E52.trimOffspring")])]}),makeQuery(id+"F24.opExtrude","SWEPT_FACE",FACE,{"disambiguationData":[OSD([subQ15,subQ10])]})])],"derivedFrom":makeQuery(id+"F20.boolean.opBoolean","MERGE",FACE,{"derivedFrom":[subQ14],"fromTools":[makeQuery(id+"F20.opExtrude","CAP_FACE",FACE,{"disambiguationData":[OSD([sQuery(id+"F19.wireOp",EDGE,"E152.0"),sQuery(id+"F19.wireOp",EDGE,"E152.1"),sQuery(id+"F19.wireOp",EDGE,"E152.2"),sQuery(id+"F19.wireOp",EDGE,"E152.3"),sQuery(id+"F19.wireOp",EDGE,"E152.4"),sQuery(id+"F19.wireOp",EDGE,"E153"),sQuery(id+"F19.wireOp",EDGE,"E154"),sQuery(id+"F19.wireOp",EDGE,"E155")])],"isStart":true})]})}),makeQuery(id+"F26.opExtrude","SWEPT_FACE",FACE,{"disambiguationData":[OSD([sQuery(id+"F11.wireOp",EDGE,"E48.MirrorCS")])]})]});}
            var Q14;
            Q14=makeQuery(id+"F18.boolean.opBoolean","INTERSECT",EDGE,{"derivedFrom":[makeQuery(id+"F15.opExtrude","CAP_FACE",FACE,{"disambiguationData":[OSD([sQuery(id+"F0.wireOp",EDGE,"E0.top"),sQuery(id+"F0.wireOp",EDGE,"E0.left"),sQuery(id+"F0.wireOp",EDGE,"E0.right"),sQuery(id+"F12.wireOp",EDGE,"E86.0"),sQuery(id+"F12.wireOp",EDGE,"E97"),sQuery(id+"F12.wireOp",EDGE,"E99")])],"isStart":false}),makeQuery(id+"F18.opExtrude","SWEPT_FACE",FACE,{"disambiguationData":[OSD([sQuery(id+"F13.wireOp",EDGE,"E103")])]})]});
            var Q15;
            {var subQ0=sQuery(id+"F14.wireOp",EDGE,"E113");var subQ1=sQuery(id+"F14.wireOp",EDGE,"E111.top");var subQ2=sQuery(id+"F14.wireOp",EDGE,"E119");var subQ3=sQuery(id+"F14.wireOp",EDGE,"E118");var subQ4=sQuery(id+"F14.wireOp",EDGE,"E117");var subQ5=sQuery(id+"F14.wireOp",EDGE,"E115");var subQ6=sQuery(id+"F14.wireOp",EDGE,"E133.MirrorCS");var subQ7=sQuery(id+"F14.wireOp",EDGE,"E114");var subQ8=sQuery(id+"F14.wireOp",EDGE,"E111.right");var subQ9=sQuery(id+"F14.wireOp",EDGE,"E143.MirrorCS");var subQ10=sQuery(id+"F0.wireOp",EDGE,"E0.left");var subQ11=sQuery(id+"F12.wireOp",EDGE,"E99");var subQ12=sQuery(id+"F0.wireOp",EDGE,"E0.right");var subQ13=sQuery(id+"F0.wireOp",EDGE,"E0.top");var subQ14=makeQuery(id+"F15.opExtrude","CAP_FACE",FACE,{"disambiguationData":[OSD([subQ13,subQ10,subQ12,sQuery(id+"F12.wireOp",EDGE,"E86.0"),sQuery(id+"F12.wireOp",EDGE,"E97"),subQ11])],"isStart":false});var subQ15=sQuery(id+"F0.wireOp",EDGE,"E0.bottom");Q15=makeQuery(id+"F25.boolean.opBoolean","INTERSECT",EDGE,{"derivedFrom":[makeQuery(id+"F24.boolean.opBoolean","SPLIT",FACE,{"disambiguationData":[TD([makeQuery(id+"F2.opShell","OFFSET_FACE",FACE,{"disambiguationData":[OSD([subQ15,subQ13,subQ10,subQ12]),TDD([makeQuery(id+"F1.opExtrude","CAP_FACE",FACE,{"disambiguationData":[OSD([subQ15,subQ13,subQ10,subQ12])],"isStart":true})])]}),makeQuery(id+"F2.opShell","OFFSET_FACE",FACE,{"disambiguationData":[OSD([subQ15,subQ13,subQ10,subQ12]),TDD([makeQuery(id+"F1.opExtrude","CAP_FACE",FACE,{"disambiguationData":[OSD([subQ15,subQ13,subQ10,subQ12])],"isStart":false})])]}),makeQuery(id+"F2.opShell","OFFSET_FACE",FACE,{"disambiguationData":[OSD([subQ10])]}),makeQuery(id+"F2.opShell","OFFSET_FACE",FACE,{"disambiguationData":[OSD([subQ12])]}),subQ14,makeQuery(id+"F15.opExtrude","SWEPT_FACE",FACE,{"disambiguationData":[OSD([subQ11])]}),makeQuery(id+"F16.opExtrude","SWEPT_FACE",FACE,{"disambiguationData":[OSD([sQuery(id+"F14.wireOp",EDGE,"E112")])]}),makeQuery(id+"F16.opExtrude","SWEPT_FACE",FACE,{"disambiguationData":[OSD([sQuery(id+"F14.wireOp",EDGE,"E116")])]}),makeQuery(id+"F16.opExtrude","SWEPT_FACE",FACE,{"disambiguationData":[OSD([sQuery(id+"F14.wireOp",EDGE,"E120")])]}),makeQuery(id+"F16.opExtrude","SWEPT_FACE",FACE,{"disambiguationData":[OSD([sQuery(id+"F14.wireOp",EDGE,"E140.MirrorCS")])]}),makeQuery(id+"F16.opExtrude","SWEPT_FACE",FACE,{"disambiguationData":[OSD([sQuery(id+"F14.wireOp",EDGE,"E144.MirrorCS")])]}),makeQuery(id+"F16.opExtrude","SWEPT_FACE",FACE,{"disambiguationData":[OSD([sQuery(id+"F14.wireOp",EDGE,"E146.MirrorCS"),sQuery(id+"F14.wireOp",EDGE,"E149")])]}),makeQuery(id+"F16.boolean.opBoolean","COPY",FACE,{"derivedFrom":makeQuery(id+"F16.opExtrude","SWEPT_FACE",FACE,{"disambiguationData":[OSD([subQ1])]})}),makeQuery(id+"F16.boolean.opBoolean","COPY",FACE,{"derivedFrom":makeQuery(id+"F16.opExtrude","SWEPT_FACE",FACE,{"disambiguationData":[OSD([subQ8])]})}),makeQuery(id+"F16.boolean.opBoolean","COPY",FACE,{"derivedFrom":makeQuery(id+"F16.opExtrude","SWEPT_FACE",FACE,{"disambiguationData":[OSD([subQ0])]})}),makeQuery(id+"F16.boolean.opBoolean","COPY",FACE,{"derivedFrom":makeQuery(id+"F16.opExtrude","SWEPT_FACE",FACE,{"disambiguationData":[OSD([subQ7])]})}),makeQuery(id+"F16.boolean.opBoolean","COPY",FACE,{"derivedFrom":makeQuery(id+"F16.opExtrude","SWEPT_FACE",FACE,{"disambiguationData":[OSD([subQ5])]})}),makeQuery(id+"F16.boolean.opBoolean","COPY",FACE,{"derivedFrom":makeQuery(id+"F16.opExtrude","SWEPT_FACE",FACE,{"disambiguationData":[OSD([subQ4])]})}),makeQuery(id+"F16.boolean.opBoolean","COPY",FACE,{"derivedFrom":makeQuery(id+"F16.opExtrude","SWEPT_FACE",FACE,{"disambiguationData":[OSD([subQ3])]})}),makeQuery(id+"F16.boolean.opBoolean","COPY",FACE,{"derivedFrom":makeQuery(id+"F16.opExtrude","SWEPT_FACE",FACE,{"disambiguationData":[OSD([subQ2])]})}),makeQuery(id+"F16.boolean.opBoolean","COPY",FACE,{"derivedFrom":makeQuery(id+"F16.opExtrude","SWEPT_FACE",FACE,{"disambiguationData":[OSD([sQuery(id+"F14.wireOp",EDGE,"E127")])]})}),makeQuery(id+"F16.boolean.opBoolean","COPY",FACE,{"derivedFrom":makeQuery(id+"F16.opExtrude","SWEPT_FACE",FACE,{"disambiguationData":[OSD([subQ6])]})}),makeQuery(id+"F16.boolean.opBoolean","COPY",FACE,{"derivedFrom":makeQuery(id+"F16.opExtrude","SWEPT_FACE",FACE,{"disambiguationData":[OSD([subQ9])]})}),makeQuery(id+"F17.opExtrude","SWEPT_FACE",FACE,{"disambiguationData":[OSD([subQ1])]}),makeQuery(id+"F17.opExtrude","SWEPT_FACE",FACE,{"disambiguationData":[OSD([subQ8])]}),makeQuery(id+"F17.opExtrude","SWEPT_FACE",FACE,{"disambiguationData":[OSD([subQ0])]}),makeQuery(id+"F17.opExtrude","SWEPT_FACE",FACE,{"disambiguationData":[OSD([subQ7])]}),makeQuery(id+"F17.opExtrude","SWEPT_FACE",FACE,{"disambiguationData":[OSD([subQ5])]}),makeQuery(id+"F17.opExtrude","SWEPT_FACE",FACE,{"disambiguationData":[OSD([subQ4])]}),makeQuery(id+"F17.opExtrude","SWEPT_FACE",FACE,{"disambiguationData":[OSD([subQ3])]}),makeQuery(id+"F17.opExtrude","SWEPT_FACE",FACE,{"disambiguationData":[OSD([subQ2])]}),makeQuery(id+"F17.opExtrude","SWEPT_FACE",FACE,{"disambiguationData":[OSD([subQ6])]}),makeQuery(id+"F17.opExtrude","SWEPT_FACE",FACE,{"disambiguationData":[OSD([subQ9])]}),makeQuery(id+"F18.opExtrude","SWEPT_FACE",FACE,{"disambiguationData":[OSD([sQuery(id+"F13.wireOp",EDGE,"E105")])]}),makeQuery(id+"F18.opExtrude","SWEPT_FACE",FACE,{"disambiguationData":[OSD([sQuery(id+"F13.wireOp",EDGE,"E106")])]}),makeQuery(id+"F18.boolean.opBoolean","COPY",FACE,{"derivedFrom":makeQuery(id+"F18.opExtrude","SWEPT_FACE",FACE,{"disambiguationData":[OSD([sQuery(id+"F13.wireOp",EDGE,"E103")])]})}),makeQuery(id+"F18.boolean.opBoolean","COPY",FACE,{"derivedFrom":makeQuery(id+"F18.opExtrude","SWEPT_FACE",FACE,{"disambiguationData":[OSD([sQuery(id+"F13.wireOp",EDGE,"E104")])]})}),makeQuery(id+"F23.boolean.opBoolean","COPY",FACE,{"derivedFrom":makeQuery(id+"F23.opExtrude","SWEPT_FACE",FACE,{"disambiguationData":[OSD([sQuery(id+"F11.wireOp",EDGE,"E30")])]})}),makeQuery(id+"F23.boolean.opBoolean","COPY",FACE,{"derivedFrom":makeQuery(id+"F23.opExtrude","SWEPT_FACE",FACE,{"disambiguationData":[OSD([sQuery(id+"F11.wireOp",EDGE,"E31")])]})}),makeQuery(id+"F23.boolean.opBoolean","COPY",FACE,{"derivedFrom":makeQuery(id+"F23.opExtrude","SWEPT_FACE",FACE,{"disambiguationData":[OSD([sQuery(id+"F11.wireOp",EDGE,"E33")])]})}),makeQuery(id+"F23.boolean.opBoolean","COPY",FACE,{"derivedFrom":makeQuery(id+"F23.opExtrude","SWEPT_FACE",FACE,{"disambiguationData":[OSD([sQuery(id+"F11.wireOp",EDGE,"E42.MirrorCS")])]})}),makeQuery(id+"F23.boolean.opBoolean","COPY",FACE,{"derivedFrom":makeQuery(id+"F23.opExtrude","SWEPT_FACE",FACE,{"disambiguationData":[OSD([sQuery(id+"F11.wireOp",EDGE,"E45.MirrorCS")])]})}),makeQuery(id+"F23.boolean.opBoolean","COPY",FACE,{"derivedFrom":makeQuery(id+"F23.opExtrude","SWEPT_FACE",FACE,{"disambiguationData":[OSD([sQuery(id+"F11.wireOp",EDGE,"E46.MirrorCS")])]})}),makeQuery(id+"F23.boolean.opBoolean","COPY",FACE,{"derivedFrom":makeQuery(id+"F23.opExtrude","SWEPT_FACE",FACE,{"disambiguationData":[OSD([sQuery(id+"F11.wireOp",EDGE,"E57")])]})}),makeQuery(id+"F23.boolean.opBoolean","COPY",FACE,{"derivedFrom":makeQuery(id+"F23.opExtrude","SWEPT_FACE",FACE,{"disambiguationData":[OSD([sQuery(id+"F11.wireOp",EDGE,"E58")])]})}),makeQuery(id+"F23.boolean.opBoolean","COPY",FACE,{"derivedFrom":makeQuery(id+"F23.opExtrude","SWEPT_FACE",FACE,{"disambiguationData":[OSD([sQuery(id+"F11.wireOp",EDGE,"E59")])]})}),makeQuery(id+"F24.opExtrude","SWEPT_FACE",FACE,{"disambiguationData":[OSD([sQuery(id+"F11.wireOp",EDGE,"E32")])]}),makeQuery(id+"F24.opExtrude","SWEPT_FACE",FACE,{"disambiguationData":[OSD([sQuery(id+"F11.wireOp",EDGE,"E34")])]}),makeQuery(id+"F24.opExtrude","SWEPT_FACE",FACE,{"disambiguationData":[OSD([sQuery(id+"F11.wireOp",EDGE,"E36")])]}),makeQuery(id+"F24.opExtrude","SWEPT_FACE",FACE,{"disambiguationData":[OSD([sQuery(id+"F11.wireOp",EDGE,"E39.MirrorCS")])]}),makeQuery(id+"F24.opExtrude","SWEPT_FACE",FACE,{"disambiguationData":[OSD([sQuery(id+"F11.wireOp",EDGE,"E40.MirrorCS")])]}),makeQuery(id+"F24.opExtrude","SWEPT_FACE",FACE,{"disambiguationData":[OSD([sQuery(id+"F11.wireOp",EDGE,"E41.MirrorCS"),sQuery(id+"F11.wireOp",EDGE,"E52.trimOffspring")])]}),makeQuery(id+"F24.opExtrude","SWEPT_FACE",FACE,{"disambiguationData":[OSD([subQ15,subQ10])]})])],"derivedFrom":makeQuery(id+"F20.boolean.opBoolean","MERGE",FACE,{"derivedFrom":[subQ14],"fromTools":[makeQuery(id+"F20.opExtrude","CAP_FACE",FACE,{"disambiguationData":[OSD([sQuery(id+"F19.wireOp",EDGE,"E152.0"),sQuery(id+"F19.wireOp",EDGE,"E152.1"),sQuery(id+"F19.wireOp",EDGE,"E152.2"),sQuery(id+"F19.wireOp",EDGE,"E152.3"),sQuery(id+"F19.wireOp",EDGE,"E152.4"),sQuery(id+"F19.wireOp",EDGE,"E153"),sQuery(id+"F19.wireOp",EDGE,"E154"),sQuery(id+"F19.wireOp",EDGE,"E155")])],"isStart":true})]})}),makeQuery(id+"F25.opExtrude","SWEPT_FACE",FACE,{"disambiguationData":[OSD([sQuery(id+"F11.wireOp",EDGE,"E53.trimOffspring")])]})]});}
            var Q16;
            {var subQ0=sQuery(id+"F12.wireOp",EDGE,"E99");var subQ1=sQuery(id+"F0.wireOp",EDGE,"E0.right");var subQ2=sQuery(id+"F0.wireOp",EDGE,"E0.left");var subQ3=sQuery(id+"F0.wireOp",EDGE,"E0.top");var subQ4=makeQuery(id+"F15.opExtrude","CAP_FACE",FACE,{"disambiguationData":[OSD([subQ3,subQ2,subQ1,sQuery(id+"F12.wireOp",EDGE,"E86.0"),sQuery(id+"F12.wireOp",EDGE,"E97"),subQ0])],"isStart":false});var subQ5=sQuery(id+"F11.wireOp",EDGE,"E46.MirrorCS");var subQ6=makeQuery(id+"F26.opExtrude","SWEPT_FACE",FACE,{"disambiguationData":[OSD([subQ5])]});var subQ7=sQuery(id+"F14.wireOp",EDGE,"E113");var subQ8=sQuery(id+"F14.wireOp",EDGE,"E111.top");var subQ9=sQuery(id+"F14.wireOp",EDGE,"E119");var subQ10=sQuery(id+"F14.wireOp",EDGE,"E118");var subQ11=sQuery(id+"F14.wireOp",EDGE,"E117");var subQ12=sQuery(id+"F14.wireOp",EDGE,"E115");var subQ13=sQuery(id+"F14.wireOp",EDGE,"E133.MirrorCS");var subQ14=sQuery(id+"F14.wireOp",EDGE,"E114");var subQ15=sQuery(id+"F14.wireOp",EDGE,"E111.right");var subQ16=sQuery(id+"F14.wireOp",EDGE,"E143.MirrorCS");var subQ17=sQuery(id+"F0.wireOp",EDGE,"E0.bottom");Q16=makeQuery(id+"F26.boolean.opBoolean","INTERSECT",EDGE,{"disambiguationData":[topologyDisambiguationEdgeConnected([subQ4,subQ6])],"derivedFrom":[makeQuery(id+"F24.boolean.opBoolean","SPLIT",FACE,{"disambiguationData":[TD([makeQuery(id+"F2.opShell","OFFSET_FACE",FACE,{"disambiguationData":[OSD([subQ17,subQ3,subQ2,subQ1]),TDD([makeQuery(id+"F1.opExtrude","CAP_FACE",FACE,{"disambiguationData":[OSD([subQ17,subQ3,subQ2,subQ1])],"isStart":true})])]}),makeQuery(id+"F2.opShell","OFFSET_FACE",FACE,{"disambiguationData":[OSD([subQ17,subQ3,subQ2,subQ1]),TDD([makeQuery(id+"F1.opExtrude","CAP_FACE",FACE,{"disambiguationData":[OSD([subQ17,subQ3,subQ2,subQ1])],"isStart":false})])]}),makeQuery(id+"F2.opShell","OFFSET_FACE",FACE,{"disambiguationData":[OSD([subQ2])]}),makeQuery(id+"F2.opShell","OFFSET_FACE",FACE,{"disambiguationData":[OSD([subQ1])]}),subQ4,makeQuery(id+"F15.opExtrude","SWEPT_FACE",FACE,{"disambiguationData":[OSD([subQ0])]}),makeQuery(id+"F16.opExtrude","SWEPT_FACE",FACE,{"disambiguationData":[OSD([sQuery(id+"F14.wireOp",EDGE,"E112")])]}),makeQuery(id+"F16.opExtrude","SWEPT_FACE",FACE,{"disambiguationData":[OSD([sQuery(id+"F14.wireOp",EDGE,"E116")])]}),makeQuery(id+"F16.opExtrude","SWEPT_FACE",FACE,{"disambiguationData":[OSD([sQuery(id+"F14.wireOp",EDGE,"E120")])]}),makeQuery(id+"F16.opExtrude","SWEPT_FACE",FACE,{"disambiguationData":[OSD([sQuery(id+"F14.wireOp",EDGE,"E140.MirrorCS")])]}),makeQuery(id+"F16.opExtrude","SWEPT_FACE",FACE,{"disambiguationData":[OSD([sQuery(id+"F14.wireOp",EDGE,"E144.MirrorCS")])]}),makeQuery(id+"F16.opExtrude","SWEPT_FACE",FACE,{"disambiguationData":[OSD([sQuery(id+"F14.wireOp",EDGE,"E146.MirrorCS"),sQuery(id+"F14.wireOp",EDGE,"E149")])]}),makeQuery(id+"F16.boolean.opBoolean","COPY",FACE,{"derivedFrom":makeQuery(id+"F16.opExtrude","SWEPT_FACE",FACE,{"disambiguationData":[OSD([subQ8])]})}),makeQuery(id+"F16.boolean.opBoolean","COPY",FACE,{"derivedFrom":makeQuery(id+"F16.opExtrude","SWEPT_FACE",FACE,{"disambiguationData":[OSD([subQ15])]})}),makeQuery(id+"F16.boolean.opBoolean","COPY",FACE,{"derivedFrom":makeQuery(id+"F16.opExtrude","SWEPT_FACE",FACE,{"disambiguationData":[OSD([subQ7])]})}),makeQuery(id+"F16.boolean.opBoolean","COPY",FACE,{"derivedFrom":makeQuery(id+"F16.opExtrude","SWEPT_FACE",FACE,{"disambiguationData":[OSD([subQ14])]})}),makeQuery(id+"F16.boolean.opBoolean","COPY",FACE,{"derivedFrom":makeQuery(id+"F16.opExtrude","SWEPT_FACE",FACE,{"disambiguationData":[OSD([subQ12])]})}),makeQuery(id+"F16.boolean.opBoolean","COPY",FACE,{"derivedFrom":makeQuery(id+"F16.opExtrude","SWEPT_FACE",FACE,{"disambiguationData":[OSD([subQ11])]})}),makeQuery(id+"F16.boolean.opBoolean","COPY",FACE,{"derivedFrom":makeQuery(id+"F16.opExtrude","SWEPT_FACE",FACE,{"disambiguationData":[OSD([subQ10])]})}),makeQuery(id+"F16.boolean.opBoolean","COPY",FACE,{"derivedFrom":makeQuery(id+"F16.opExtrude","SWEPT_FACE",FACE,{"disambiguationData":[OSD([subQ9])]})}),makeQuery(id+"F16.boolean.opBoolean","COPY",FACE,{"derivedFrom":makeQuery(id+"F16.opExtrude","SWEPT_FACE",FACE,{"disambiguationData":[OSD([sQuery(id+"F14.wireOp",EDGE,"E127")])]})}),makeQuery(id+"F16.boolean.opBoolean","COPY",FACE,{"derivedFrom":makeQuery(id+"F16.opExtrude","SWEPT_FACE",FACE,{"disambiguationData":[OSD([subQ13])]})}),makeQuery(id+"F16.boolean.opBoolean","COPY",FACE,{"derivedFrom":makeQuery(id+"F16.opExtrude","SWEPT_FACE",FACE,{"disambiguationData":[OSD([subQ16])]})}),makeQuery(id+"F17.opExtrude","SWEPT_FACE",FACE,{"disambiguationData":[OSD([subQ8])]}),makeQuery(id+"F17.opExtrude","SWEPT_FACE",FACE,{"disambiguationData":[OSD([subQ15])]}),makeQuery(id+"F17.opExtrude","SWEPT_FACE",FACE,{"disambiguationData":[OSD([subQ7])]}),makeQuery(id+"F17.opExtrude","SWEPT_FACE",FACE,{"disambiguationData":[OSD([subQ14])]}),makeQuery(id+"F17.opExtrude","SWEPT_FACE",FACE,{"disambiguationData":[OSD([subQ12])]}),makeQuery(id+"F17.opExtrude","SWEPT_FACE",FACE,{"disambiguationData":[OSD([subQ11])]}),makeQuery(id+"F17.opExtrude","SWEPT_FACE",FACE,{"disambiguationData":[OSD([subQ10])]}),makeQuery(id+"F17.opExtrude","SWEPT_FACE",FACE,{"disambiguationData":[OSD([subQ9])]}),makeQuery(id+"F17.opExtrude","SWEPT_FACE",FACE,{"disambiguationData":[OSD([subQ13])]}),makeQuery(id+"F17.opExtrude","SWEPT_FACE",FACE,{"disambiguationData":[OSD([subQ16])]}),makeQuery(id+"F18.opExtrude","SWEPT_FACE",FACE,{"disambiguationData":[OSD([sQuery(id+"F13.wireOp",EDGE,"E105")])]}),makeQuery(id+"F18.opExtrude","SWEPT_FACE",FACE,{"disambiguationData":[OSD([sQuery(id+"F13.wireOp",EDGE,"E106")])]}),makeQuery(id+"F18.boolean.opBoolean","COPY",FACE,{"derivedFrom":makeQuery(id+"F18.opExtrude","SWEPT_FACE",FACE,{"disambiguationData":[OSD([sQuery(id+"F13.wireOp",EDGE,"E103")])]})}),makeQuery(id+"F18.boolean.opBoolean","COPY",FACE,{"derivedFrom":makeQuery(id+"F18.opExtrude","SWEPT_FACE",FACE,{"disambiguationData":[OSD([sQuery(id+"F13.wireOp",EDGE,"E104")])]})}),makeQuery(id+"F23.boolean.opBoolean","COPY",FACE,{"derivedFrom":makeQuery(id+"F23.opExtrude","SWEPT_FACE",FACE,{"disambiguationData":[OSD([sQuery(id+"F11.wireOp",EDGE,"E30")])]})}),makeQuery(id+"F23.boolean.opBoolean","COPY",FACE,{"derivedFrom":makeQuery(id+"F23.opExtrude","SWEPT_FACE",FACE,{"disambiguationData":[OSD([sQuery(id+"F11.wireOp",EDGE,"E31")])]})}),makeQuery(id+"F23.boolean.opBoolean","COPY",FACE,{"derivedFrom":makeQuery(id+"F23.opExtrude","SWEPT_FACE",FACE,{"disambiguationData":[OSD([sQuery(id+"F11.wireOp",EDGE,"E33")])]})}),makeQuery(id+"F23.boolean.opBoolean","COPY",FACE,{"derivedFrom":makeQuery(id+"F23.opExtrude","SWEPT_FACE",FACE,{"disambiguationData":[OSD([sQuery(id+"F11.wireOp",EDGE,"E42.MirrorCS")])]})}),makeQuery(id+"F23.boolean.opBoolean","COPY",FACE,{"derivedFrom":makeQuery(id+"F23.opExtrude","SWEPT_FACE",FACE,{"disambiguationData":[OSD([sQuery(id+"F11.wireOp",EDGE,"E45.MirrorCS")])]})}),makeQuery(id+"F23.boolean.opBoolean","COPY",FACE,{"derivedFrom":makeQuery(id+"F23.opExtrude","SWEPT_FACE",FACE,{"disambiguationData":[OSD([subQ5])]})}),makeQuery(id+"F23.boolean.opBoolean","COPY",FACE,{"derivedFrom":makeQuery(id+"F23.opExtrude","SWEPT_FACE",FACE,{"disambiguationData":[OSD([sQuery(id+"F11.wireOp",EDGE,"E57")])]})}),makeQuery(id+"F23.boolean.opBoolean","COPY",FACE,{"derivedFrom":makeQuery(id+"F23.opExtrude","SWEPT_FACE",FACE,{"disambiguationData":[OSD([sQuery(id+"F11.wireOp",EDGE,"E58")])]})}),makeQuery(id+"F23.boolean.opBoolean","COPY",FACE,{"derivedFrom":makeQuery(id+"F23.opExtrude","SWEPT_FACE",FACE,{"disambiguationData":[OSD([sQuery(id+"F11.wireOp",EDGE,"E59")])]})}),makeQuery(id+"F24.opExtrude","SWEPT_FACE",FACE,{"disambiguationData":[OSD([sQuery(id+"F11.wireOp",EDGE,"E32")])]}),makeQuery(id+"F24.opExtrude","SWEPT_FACE",FACE,{"disambiguationData":[OSD([sQuery(id+"F11.wireOp",EDGE,"E34")])]}),makeQuery(id+"F24.opExtrude","SWEPT_FACE",FACE,{"disambiguationData":[OSD([sQuery(id+"F11.wireOp",EDGE,"E36")])]}),makeQuery(id+"F24.opExtrude","SWEPT_FACE",FACE,{"disambiguationData":[OSD([sQuery(id+"F11.wireOp",EDGE,"E39.MirrorCS")])]}),makeQuery(id+"F24.opExtrude","SWEPT_FACE",FACE,{"disambiguationData":[OSD([sQuery(id+"F11.wireOp",EDGE,"E40.MirrorCS")])]}),makeQuery(id+"F24.opExtrude","SWEPT_FACE",FACE,{"disambiguationData":[OSD([sQuery(id+"F11.wireOp",EDGE,"E41.MirrorCS"),sQuery(id+"F11.wireOp",EDGE,"E52.trimOffspring")])]}),makeQuery(id+"F24.opExtrude","SWEPT_FACE",FACE,{"disambiguationData":[OSD([subQ17,subQ2])]})])],"derivedFrom":makeQuery(id+"F20.boolean.opBoolean","MERGE",FACE,{"derivedFrom":[subQ4],"fromTools":[makeQuery(id+"F20.opExtrude","CAP_FACE",FACE,{"disambiguationData":[OSD([sQuery(id+"F19.wireOp",EDGE,"E152.0"),sQuery(id+"F19.wireOp",EDGE,"E152.1"),sQuery(id+"F19.wireOp",EDGE,"E152.2"),sQuery(id+"F19.wireOp",EDGE,"E152.3"),sQuery(id+"F19.wireOp",EDGE,"E152.4"),sQuery(id+"F19.wireOp",EDGE,"E153"),sQuery(id+"F19.wireOp",EDGE,"E154"),sQuery(id+"F19.wireOp",EDGE,"E155")])],"isStart":true})]})}),subQ6]});}
            var Q17;
            {var subQ0=sQuery(id+"F0.wireOp",EDGE,"E0.top");Q17=makeQuery(id+"F18.boolean.opBoolean","MERGE",FACE,{"derivedFrom":[makeQuery(id+"F16.boolean.opBoolean","MERGE",FACE,{"derivedFrom":[makeQuery(id+"F2.opShell","OFFSET_FACE",FACE,{"disambiguationData":[OSD([subQ0])]}),makeQuery(id+"F16.opExtrude","CAP_FACE",FACE,{"disambiguationData":[OSD([subQ0])],"isStart":false})]}),makeQuery(id+"F18.opExtrude","CAP_FACE",FACE,{"disambiguationData":[OSD([sQuery(id+"F13.wireOp",EDGE,"E103"),sQuery(id+"F13.wireOp",EDGE,"E104"),sQuery(id+"F13.wireOp",EDGE,"E105"),sQuery(id+"F13.wireOp",EDGE,"E106")])],"isStart":true})]});}
            var Q18;
            {var subQ0=sQuery(id+"F14.wireOp",EDGE,"E132.MirrorCS");Q18=makeQuery(id+"F17.boolean.opBoolean","MERGE",FACE,{"derivedFrom":[makeQuery(id+"F16.boolean.opBoolean","COPY",FACE,{"derivedFrom":makeQuery(id+"F16.opExtrude","SWEPT_FACE",FACE,{"disambiguationData":[OSD([subQ0])]})}),makeQuery(id+"F17.opExtrude","SWEPT_FACE",FACE,{"disambiguationData":[OSD([subQ0])]})]});}
            var Q19;
            {var subQ0=sQuery(id+"F14.wireOp",EDGE,"E134.MirrorCS");Q19=makeQuery(id+"F17.boolean.opBoolean","MERGE",FACE,{"derivedFrom":[makeQuery(id+"F16.boolean.opBoolean","COPY",FACE,{"derivedFrom":makeQuery(id+"F16.opExtrude","SWEPT_FACE",FACE,{"disambiguationData":[OSD([subQ0])]})}),makeQuery(id+"F17.opExtrude","SWEPT_FACE",FACE,{"disambiguationData":[OSD([subQ0])]})]});}
            var Q20;
            {var subQ0=sQuery(id+"F14.wireOp",EDGE,"E118");Q20=makeQuery(id+"F17.boolean.opBoolean","MERGE",FACE,{"derivedFrom":[makeQuery(id+"F16.boolean.opBoolean","COPY",FACE,{"derivedFrom":makeQuery(id+"F16.opExtrude","SWEPT_FACE",FACE,{"disambiguationData":[OSD([subQ0])]})}),makeQuery(id+"F17.opExtrude","SWEPT_FACE",FACE,{"disambiguationData":[OSD([subQ0])]})]});}
            var Q21;
            {var subQ0=sQuery(id+"F14.wireOp",EDGE,"E114");Q21=makeQuery(id+"F17.boolean.opBoolean","MERGE",FACE,{"derivedFrom":[makeQuery(id+"F16.boolean.opBoolean","COPY",FACE,{"derivedFrom":makeQuery(id+"F16.opExtrude","SWEPT_FACE",FACE,{"disambiguationData":[OSD([subQ0])]})}),makeQuery(id+"F17.opExtrude","SWEPT_FACE",FACE,{"disambiguationData":[OSD([subQ0])]})]});}
            var Q22;
            Q22=makeQuery(id+"F16.boolean.opBoolean","COPY",FACE,{"derivedFrom":makeQuery(id+"F16.opExtrude","SWEPT_FACE",FACE,{"disambiguationData":[OSD([sQuery(id+"F14.wireOp",EDGE,"E127")])]})});
            var Q23;
            {var subQ0=sQuery(id+"F14.wireOp",EDGE,"E111.top");Q23=makeQuery(id+"F17.boolean.opBoolean","MERGE",FACE,{"derivedFrom":[makeQuery(id+"F16.boolean.opBoolean","COPY",FACE,{"derivedFrom":makeQuery(id+"F16.opExtrude","SWEPT_FACE",FACE,{"disambiguationData":[OSD([subQ0])]})}),makeQuery(id+"F17.opExtrude","SWEPT_FACE",FACE,{"disambiguationData":[OSD([subQ0])]})]});}
            var Q24;
            {var subQ0=sQuery(id+"F14.wireOp",EDGE,"E133.MirrorCS");Q24=makeQuery(id+"F17.boolean.opBoolean","MERGE",FACE,{"derivedFrom":[makeQuery(id+"F16.boolean.opBoolean","COPY",FACE,{"derivedFrom":makeQuery(id+"F16.opExtrude","SWEPT_FACE",FACE,{"disambiguationData":[OSD([subQ0])]})}),makeQuery(id+"F17.opExtrude","SWEPT_FACE",FACE,{"disambiguationData":[OSD([subQ0])]})]});}
            fillet(context, id + "F27", {"entities" : qUnion([Q0, Q1, Q2, Q3, Q4, Q5, Q6, Q7, Q8, Q9, Q10, Q11, Q12, Q13, Q14, Q15, Q16, Q17, Q18, Q19, Q20, Q21, Q22, Q23, Q24]), "radius" : .5 * mm, "tangentPropagation" : true, "allowEdgeOverflow" : false});
        }
        {
            var Q0;
            {var subQ0=sQuery(id+"F14.wireOp",EDGE,"E143.MirrorCS");var subQ1=makeQuery(id+"F16.boolean.opBoolean","COPY",FACE,{"derivedFrom":makeQuery(id+"F16.opExtrude","SWEPT_FACE",FACE,{"disambiguationData":[OSD([subQ0])]})});var subQ2=sQuery(id+"F14.wireOp",EDGE,"E119");var subQ3=makeQuery(id+"F16.boolean.opBoolean","COPY",FACE,{"derivedFrom":makeQuery(id+"F16.opExtrude","SWEPT_FACE",FACE,{"disambiguationData":[OSD([subQ2])]})});var subQ4=sQuery(id+"F14.wireOp",EDGE,"E118");var subQ5=makeQuery(id+"F16.boolean.opBoolean","COPY",FACE,{"derivedFrom":makeQuery(id+"F16.opExtrude","SWEPT_FACE",FACE,{"disambiguationData":[OSD([subQ4])]})});var subQ6=makeQuery(id+"F18.opExtrude","SWEPT_FACE",FACE,{"disambiguationData":[OSD([sQuery(id+"F13.wireOp",EDGE,"E105")])]});var subQ7=sQuery(id+"F14.wireOp",EDGE,"E117");var subQ8=makeQuery(id+"F16.boolean.opBoolean","COPY",FACE,{"derivedFrom":makeQuery(id+"F16.opExtrude","SWEPT_FACE",FACE,{"disambiguationData":[OSD([subQ7])]})});var subQ9=sQuery(id+"F14.wireOp",EDGE,"E115");var subQ10=makeQuery(id+"F16.boolean.opBoolean","COPY",FACE,{"derivedFrom":makeQuery(id+"F16.opExtrude","SWEPT_FACE",FACE,{"disambiguationData":[OSD([subQ9])]})});var subQ11=sQuery(id+"F14.wireOp",EDGE,"E114");var subQ12=makeQuery(id+"F16.boolean.opBoolean","COPY",FACE,{"derivedFrom":makeQuery(id+"F16.opExtrude","SWEPT_FACE",FACE,{"disambiguationData":[OSD([subQ11])]})});var subQ13=sQuery(id+"F14.wireOp",EDGE,"E113");var subQ14=makeQuery(id+"F16.boolean.opBoolean","COPY",FACE,{"derivedFrom":makeQuery(id+"F16.opExtrude","SWEPT_FACE",FACE,{"disambiguationData":[OSD([subQ13])]})});var subQ15=sQuery(id+"F14.wireOp",EDGE,"E133.MirrorCS");var subQ16=makeQuery(id+"F17.opExtrude","SWEPT_FACE",FACE,{"disambiguationData":[OSD([subQ15])]});var subQ17=sQuery(id+"F14.wireOp",EDGE,"E111.right");var subQ18=makeQuery(id+"F16.boolean.opBoolean","COPY",FACE,{"derivedFrom":makeQuery(id+"F16.opExtrude","SWEPT_FACE",FACE,{"disambiguationData":[OSD([subQ17])]})});var subQ19=sQuery(id+"F14.wireOp",EDGE,"E111.top");var subQ20=makeQuery(id+"F16.boolean.opBoolean","COPY",FACE,{"derivedFrom":makeQuery(id+"F16.opExtrude","SWEPT_FACE",FACE,{"disambiguationData":[OSD([subQ19])]})});var subQ21=sQuery(id+"F12.wireOp",EDGE,"E99");var subQ22=makeQuery(id+"F15.opExtrude","SWEPT_FACE",FACE,{"disambiguationData":[OSD([subQ21])]});var subQ23=makeQuery(id+"F16.opExtrude","SWEPT_FACE",FACE,{"disambiguationData":[OSD([sQuery(id+"F14.wireOp",EDGE,"E116")])]});var subQ24=makeQuery(id+"F17.opExtrude","SWEPT_FACE",FACE,{"disambiguationData":[OSD([subQ19])]});var subQ25=makeQuery(id+"F16.opExtrude","SWEPT_FACE",FACE,{"disambiguationData":[OSD([sQuery(id+"F14.wireOp",EDGE,"E120")])]});var subQ26=makeQuery(id+"F16.boolean.opBoolean","COPY",FACE,{"derivedFrom":makeQuery(id+"F16.opExtrude","SWEPT_FACE",FACE,{"disambiguationData":[OSD([sQuery(id+"F14.wireOp",EDGE,"E127")])]})});var subQ27=makeQuery(id+"F16.opExtrude","SWEPT_FACE",FACE,{"disambiguationData":[OSD([sQuery(id+"F14.wireOp",EDGE,"E140.MirrorCS")])]});var subQ28=sQuery(id+"F0.wireOp",EDGE,"E0.right");var subQ29=sQuery(id+"F0.wireOp",EDGE,"E0.left");var subQ30=sQuery(id+"F0.wireOp",EDGE,"E0.top");var subQ31=sQuery(id+"F0.wireOp",EDGE,"E0.bottom");var subQ32=makeQuery(id+"F2.opShell","OFFSET_FACE",FACE,{"disambiguationData":[OSD([subQ31,subQ30,subQ29,subQ28]),TDD([makeQuery(id+"F1.opExtrude","CAP_FACE",FACE,{"disambiguationData":[OSD([subQ31,subQ30,subQ29,subQ28])],"isStart":false})])]});var subQ33=makeQuery(id+"F2.opShell","OFFSET_FACE",FACE,{"disambiguationData":[OSD([subQ29])]});var subQ34=makeQuery(id+"F16.opExtrude","SWEPT_FACE",FACE,{"disambiguationData":[OSD([sQuery(id+"F14.wireOp",EDGE,"E112")])]});var subQ35=makeQuery(id+"F16.boolean.opBoolean","COPY",FACE,{"derivedFrom":makeQuery(id+"F16.opExtrude","SWEPT_FACE",FACE,{"disambiguationData":[OSD([subQ15])]})});var subQ36=makeQuery(id+"F16.opExtrude","SWEPT_FACE",FACE,{"disambiguationData":[OSD([sQuery(id+"F14.wireOp",EDGE,"E144.MirrorCS")])]});var subQ37=makeQuery(id+"F2.opShell","OFFSET_FACE",FACE,{"disambiguationData":[OSD([subQ28])]});var subQ38=makeQuery(id+"F17.opExtrude","SWEPT_FACE",FACE,{"disambiguationData":[OSD([subQ0])]});var subQ39=makeQuery(id+"F16.opExtrude","SWEPT_FACE",FACE,{"disambiguationData":[OSD([sQuery(id+"F14.wireOp",EDGE,"E146.MirrorCS"),sQuery(id+"F14.wireOp",EDGE,"E149")])]});var subQ40=makeQuery(id+"F17.opExtrude","SWEPT_FACE",FACE,{"disambiguationData":[OSD([subQ17])]});var subQ41=makeQuery(id+"F24.opExtrude","SWEPT_FACE",FACE,{"disambiguationData":[OSD([sQuery(id+"F11.wireOp",EDGE,"E36")])]});var subQ42=makeQuery(id+"F17.opExtrude","SWEPT_FACE",FACE,{"disambiguationData":[OSD([subQ13])]});var subQ43=makeQuery(id+"F17.opExtrude","SWEPT_FACE",FACE,{"disambiguationData":[OSD([subQ11])]});var subQ44=makeQuery(id+"F17.opExtrude","SWEPT_FACE",FACE,{"disambiguationData":[OSD([subQ9])]});var subQ45=makeQuery(id+"F17.opExtrude","SWEPT_FACE",FACE,{"disambiguationData":[OSD([subQ7])]});var subQ46=makeQuery(id+"F17.opExtrude","SWEPT_FACE",FACE,{"disambiguationData":[OSD([subQ4])]});var subQ47=makeQuery(id+"F17.opExtrude","SWEPT_FACE",FACE,{"disambiguationData":[OSD([subQ2])]});var subQ48=makeQuery(id+"F23.boolean.opBoolean","COPY",FACE,{"derivedFrom":makeQuery(id+"F23.opExtrude","SWEPT_FACE",FACE,{"disambiguationData":[OSD([sQuery(id+"F11.wireOp",EDGE,"E30")])]})});var subQ49=sQuery(id+"F11.wireOp",EDGE,"E31");var subQ50=makeQuery(id+"F23.boolean.opBoolean","COPY",FACE,{"derivedFrom":makeQuery(id+"F23.opExtrude","SWEPT_FACE",FACE,{"disambiguationData":[OSD([subQ49])]})});var subQ51=makeQuery(id+"F23.boolean.opBoolean","COPY",FACE,{"derivedFrom":makeQuery(id+"F23.opExtrude","SWEPT_FACE",FACE,{"disambiguationData":[OSD([sQuery(id+"F11.wireOp",EDGE,"E33")])]})});var subQ52=makeQuery(id+"F24.opExtrude","SWEPT_FACE",FACE,{"disambiguationData":[OSD([sQuery(id+"F11.wireOp",EDGE,"E32")])]});var subQ53=makeQuery(id+"F24.opExtrude","SWEPT_FACE",FACE,{"disambiguationData":[OSD([sQuery(id+"F11.wireOp",EDGE,"E34")])]});var subQ54=makeQuery(id+"F15.opExtrude","CAP_FACE",FACE,{"disambiguationData":[OSD([subQ30,subQ29,subQ28,sQuery(id+"F12.wireOp",EDGE,"E86.0"),sQuery(id+"F12.wireOp",EDGE,"E97"),subQ21])],"isStart":false});Q0=makeQuery(id+"F26.boolean.opBoolean","SPLIT",FACE,{"disambiguationData":[TD([subQ33])],"derivedFrom":makeQuery(id+"F24.boolean.opBoolean","SPLIT",FACE,{"disambiguationData":[TD([makeQuery(id+"F2.opShell","OFFSET_FACE",FACE,{"disambiguationData":[OSD([subQ31,subQ30,subQ29,subQ28]),TDD([makeQuery(id+"F1.opExtrude","CAP_FACE",FACE,{"disambiguationData":[OSD([subQ31,subQ30,subQ29,subQ28])],"isStart":true})])]}),subQ32,subQ33,subQ37,subQ54,subQ22,subQ34,subQ23,subQ25,subQ27,subQ36,subQ39,subQ20,subQ18,subQ14,subQ12,subQ10,subQ8,subQ5,subQ3,subQ26,subQ35,subQ1,subQ24,subQ40,subQ42,subQ43,subQ44,subQ45,subQ46,subQ47,subQ16,subQ38,subQ6,makeQuery(id+"F18.opExtrude","SWEPT_FACE",FACE,{"disambiguationData":[OSD([sQuery(id+"F13.wireOp",EDGE,"E106")])]}),makeQuery(id+"F18.boolean.opBoolean","COPY",FACE,{"derivedFrom":makeQuery(id+"F18.opExtrude","SWEPT_FACE",FACE,{"disambiguationData":[OSD([sQuery(id+"F13.wireOp",EDGE,"E103")])]})}),makeQuery(id+"F18.boolean.opBoolean","COPY",FACE,{"derivedFrom":makeQuery(id+"F18.opExtrude","SWEPT_FACE",FACE,{"disambiguationData":[OSD([sQuery(id+"F13.wireOp",EDGE,"E104")])]})}),subQ48,subQ50,subQ51,makeQuery(id+"F23.boolean.opBoolean","COPY",FACE,{"derivedFrom":makeQuery(id+"F23.opExtrude","SWEPT_FACE",FACE,{"disambiguationData":[OSD([sQuery(id+"F11.wireOp",EDGE,"E42.MirrorCS")])]})}),makeQuery(id+"F23.boolean.opBoolean","COPY",FACE,{"derivedFrom":makeQuery(id+"F23.opExtrude","SWEPT_FACE",FACE,{"disambiguationData":[OSD([sQuery(id+"F11.wireOp",EDGE,"E45.MirrorCS")])]})}),makeQuery(id+"F23.boolean.opBoolean","COPY",FACE,{"derivedFrom":makeQuery(id+"F23.opExtrude","SWEPT_FACE",FACE,{"disambiguationData":[OSD([sQuery(id+"F11.wireOp",EDGE,"E46.MirrorCS")])]})}),makeQuery(id+"F23.boolean.opBoolean","COPY",FACE,{"derivedFrom":makeQuery(id+"F23.opExtrude","SWEPT_FACE",FACE,{"disambiguationData":[OSD([sQuery(id+"F11.wireOp",EDGE,"E57")])]})}),makeQuery(id+"F23.boolean.opBoolean","COPY",FACE,{"derivedFrom":makeQuery(id+"F23.opExtrude","SWEPT_FACE",FACE,{"disambiguationData":[OSD([sQuery(id+"F11.wireOp",EDGE,"E58")])]})}),makeQuery(id+"F23.boolean.opBoolean","COPY",FACE,{"derivedFrom":makeQuery(id+"F23.opExtrude","SWEPT_FACE",FACE,{"disambiguationData":[OSD([sQuery(id+"F11.wireOp",EDGE,"E59")])]})}),subQ52,subQ53,subQ41,makeQuery(id+"F24.opExtrude","SWEPT_FACE",FACE,{"disambiguationData":[OSD([sQuery(id+"F11.wireOp",EDGE,"E39.MirrorCS")])]}),makeQuery(id+"F24.opExtrude","SWEPT_FACE",FACE,{"disambiguationData":[OSD([sQuery(id+"F11.wireOp",EDGE,"E40.MirrorCS")])]}),makeQuery(id+"F24.opExtrude","SWEPT_FACE",FACE,{"disambiguationData":[OSD([sQuery(id+"F11.wireOp",EDGE,"E41.MirrorCS"),sQuery(id+"F11.wireOp",EDGE,"E52.trimOffspring")])]}),makeQuery(id+"F24.opExtrude","SWEPT_FACE",FACE,{"disambiguationData":[OSD([subQ31,subQ29])]})])],"derivedFrom":makeQuery(id+"F20.boolean.opBoolean","MERGE",FACE,{"derivedFrom":[subQ54],"fromTools":[makeQuery(id+"F20.opExtrude","CAP_FACE",FACE,{"disambiguationData":[OSD([sQuery(id+"F19.wireOp",EDGE,"E152.0"),sQuery(id+"F19.wireOp",EDGE,"E152.1"),sQuery(id+"F19.wireOp",EDGE,"E152.2"),sQuery(id+"F19.wireOp",EDGE,"E152.3"),sQuery(id+"F19.wireOp",EDGE,"E152.4"),sQuery(id+"F19.wireOp",EDGE,"E153"),sQuery(id+"F19.wireOp",EDGE,"E154"),sQuery(id+"F19.wireOp",EDGE,"E155")])],"isStart":true})]})})});}
            var sketch = newSketch(context, id + "F28", { "sketchPlane" : qUnion([Q0])});
            skText(sketch, "E163", { "text": "B-Wing", "fontName": "NotoSans-Bold.ttf"});
            skLineSegment(sketch, "E164", {"start": v(-20.1, 8.46) * mm, "end": v(-18.9, 8.46) * mm});
            skLineSegment(sketch, "E165", {"start": v(-18.9, 39.2) * mm, "end": v(-18.9, 38) * mm});
            skLineSegment(sketch, "E166", {"start": v(-18.9, 39.2) * mm, "end": v(-26.5, 39.2) * mm});
            const initialGuessF28  = {"E163": [-0.0129, 0.00846, 0, 1, 0.006]};
            skSetInitialGuess(sketch, initialGuessF28);
            skSolve(sketch);
        }
        {
            var Q0;
            {var subQ0=sQuery(id+"F14.wireOp",EDGE,"E143.MirrorCS");var subQ1=makeQuery(id+"F16.boolean.opBoolean","COPY",FACE,{"derivedFrom":makeQuery(id+"F16.opExtrude","SWEPT_FACE",FACE,{"disambiguationData":[OSD([subQ0])]})});var subQ2=sQuery(id+"F14.wireOp",EDGE,"E119");var subQ3=makeQuery(id+"F16.boolean.opBoolean","COPY",FACE,{"derivedFrom":makeQuery(id+"F16.opExtrude","SWEPT_FACE",FACE,{"disambiguationData":[OSD([subQ2])]})});var subQ4=sQuery(id+"F14.wireOp",EDGE,"E118");var subQ5=makeQuery(id+"F16.boolean.opBoolean","COPY",FACE,{"derivedFrom":makeQuery(id+"F16.opExtrude","SWEPT_FACE",FACE,{"disambiguationData":[OSD([subQ4])]})});var subQ6=makeQuery(id+"F18.opExtrude","SWEPT_FACE",FACE,{"disambiguationData":[OSD([sQuery(id+"F13.wireOp",EDGE,"E105")])]});var subQ7=sQuery(id+"F14.wireOp",EDGE,"E117");var subQ8=makeQuery(id+"F16.boolean.opBoolean","COPY",FACE,{"derivedFrom":makeQuery(id+"F16.opExtrude","SWEPT_FACE",FACE,{"disambiguationData":[OSD([subQ7])]})});var subQ9=sQuery(id+"F14.wireOp",EDGE,"E115");var subQ10=makeQuery(id+"F16.boolean.opBoolean","COPY",FACE,{"derivedFrom":makeQuery(id+"F16.opExtrude","SWEPT_FACE",FACE,{"disambiguationData":[OSD([subQ9])]})});var subQ11=sQuery(id+"F14.wireOp",EDGE,"E114");var subQ12=makeQuery(id+"F16.boolean.opBoolean","COPY",FACE,{"derivedFrom":makeQuery(id+"F16.opExtrude","SWEPT_FACE",FACE,{"disambiguationData":[OSD([subQ11])]})});var subQ13=sQuery(id+"F14.wireOp",EDGE,"E113");var subQ14=makeQuery(id+"F16.boolean.opBoolean","COPY",FACE,{"derivedFrom":makeQuery(id+"F16.opExtrude","SWEPT_FACE",FACE,{"disambiguationData":[OSD([subQ13])]})});var subQ15=sQuery(id+"F14.wireOp",EDGE,"E133.MirrorCS");var subQ16=makeQuery(id+"F17.opExtrude","SWEPT_FACE",FACE,{"disambiguationData":[OSD([subQ15])]});var subQ17=sQuery(id+"F14.wireOp",EDGE,"E111.right");var subQ18=makeQuery(id+"F16.boolean.opBoolean","COPY",FACE,{"derivedFrom":makeQuery(id+"F16.opExtrude","SWEPT_FACE",FACE,{"disambiguationData":[OSD([subQ17])]})});var subQ19=sQuery(id+"F14.wireOp",EDGE,"E111.top");var subQ20=makeQuery(id+"F16.boolean.opBoolean","COPY",FACE,{"derivedFrom":makeQuery(id+"F16.opExtrude","SWEPT_FACE",FACE,{"disambiguationData":[OSD([subQ19])]})});var subQ21=sQuery(id+"F12.wireOp",EDGE,"E99");var subQ22=makeQuery(id+"F15.opExtrude","SWEPT_FACE",FACE,{"disambiguationData":[OSD([subQ21])]});var subQ23=makeQuery(id+"F16.opExtrude","SWEPT_FACE",FACE,{"disambiguationData":[OSD([sQuery(id+"F14.wireOp",EDGE,"E116")])]});var subQ24=makeQuery(id+"F17.opExtrude","SWEPT_FACE",FACE,{"disambiguationData":[OSD([subQ19])]});var subQ25=makeQuery(id+"F16.opExtrude","SWEPT_FACE",FACE,{"disambiguationData":[OSD([sQuery(id+"F14.wireOp",EDGE,"E120")])]});var subQ26=makeQuery(id+"F16.boolean.opBoolean","COPY",FACE,{"derivedFrom":makeQuery(id+"F16.opExtrude","SWEPT_FACE",FACE,{"disambiguationData":[OSD([sQuery(id+"F14.wireOp",EDGE,"E127")])]})});var subQ27=makeQuery(id+"F16.opExtrude","SWEPT_FACE",FACE,{"disambiguationData":[OSD([sQuery(id+"F14.wireOp",EDGE,"E140.MirrorCS")])]});var subQ28=sQuery(id+"F0.wireOp",EDGE,"E0.right");var subQ29=sQuery(id+"F0.wireOp",EDGE,"E0.left");var subQ30=sQuery(id+"F0.wireOp",EDGE,"E0.top");var subQ31=sQuery(id+"F0.wireOp",EDGE,"E0.bottom");var subQ32=makeQuery(id+"F2.opShell","OFFSET_FACE",FACE,{"disambiguationData":[OSD([subQ31,subQ30,subQ29,subQ28]),TDD([makeQuery(id+"F1.opExtrude","CAP_FACE",FACE,{"disambiguationData":[OSD([subQ31,subQ30,subQ29,subQ28])],"isStart":false})])]});var subQ33=makeQuery(id+"F2.opShell","OFFSET_FACE",FACE,{"disambiguationData":[OSD([subQ29])]});var subQ34=makeQuery(id+"F16.opExtrude","SWEPT_FACE",FACE,{"disambiguationData":[OSD([sQuery(id+"F14.wireOp",EDGE,"E112")])]});var subQ35=makeQuery(id+"F16.boolean.opBoolean","COPY",FACE,{"derivedFrom":makeQuery(id+"F16.opExtrude","SWEPT_FACE",FACE,{"disambiguationData":[OSD([subQ15])]})});var subQ36=makeQuery(id+"F16.opExtrude","SWEPT_FACE",FACE,{"disambiguationData":[OSD([sQuery(id+"F14.wireOp",EDGE,"E144.MirrorCS")])]});var subQ37=makeQuery(id+"F2.opShell","OFFSET_FACE",FACE,{"disambiguationData":[OSD([subQ28])]});var subQ38=makeQuery(id+"F17.opExtrude","SWEPT_FACE",FACE,{"disambiguationData":[OSD([subQ0])]});var subQ39=makeQuery(id+"F16.opExtrude","SWEPT_FACE",FACE,{"disambiguationData":[OSD([sQuery(id+"F14.wireOp",EDGE,"E146.MirrorCS"),sQuery(id+"F14.wireOp",EDGE,"E149")])]});var subQ40=makeQuery(id+"F17.opExtrude","SWEPT_FACE",FACE,{"disambiguationData":[OSD([subQ17])]});var subQ41=makeQuery(id+"F24.opExtrude","SWEPT_FACE",FACE,{"disambiguationData":[OSD([sQuery(id+"F11.wireOp",EDGE,"E36")])]});var subQ42=makeQuery(id+"F17.opExtrude","SWEPT_FACE",FACE,{"disambiguationData":[OSD([subQ13])]});var subQ43=makeQuery(id+"F17.opExtrude","SWEPT_FACE",FACE,{"disambiguationData":[OSD([subQ11])]});var subQ44=makeQuery(id+"F17.opExtrude","SWEPT_FACE",FACE,{"disambiguationData":[OSD([subQ9])]});var subQ45=makeQuery(id+"F17.opExtrude","SWEPT_FACE",FACE,{"disambiguationData":[OSD([subQ7])]});var subQ46=makeQuery(id+"F17.opExtrude","SWEPT_FACE",FACE,{"disambiguationData":[OSD([subQ4])]});var subQ47=makeQuery(id+"F17.opExtrude","SWEPT_FACE",FACE,{"disambiguationData":[OSD([subQ2])]});var subQ48=makeQuery(id+"F23.boolean.opBoolean","COPY",FACE,{"derivedFrom":makeQuery(id+"F23.opExtrude","SWEPT_FACE",FACE,{"disambiguationData":[OSD([sQuery(id+"F11.wireOp",EDGE,"E30")])]})});var subQ49=sQuery(id+"F11.wireOp",EDGE,"E31");var subQ50=makeQuery(id+"F23.boolean.opBoolean","COPY",FACE,{"derivedFrom":makeQuery(id+"F23.opExtrude","SWEPT_FACE",FACE,{"disambiguationData":[OSD([subQ49])]})});var subQ51=makeQuery(id+"F23.boolean.opBoolean","COPY",FACE,{"derivedFrom":makeQuery(id+"F23.opExtrude","SWEPT_FACE",FACE,{"disambiguationData":[OSD([sQuery(id+"F11.wireOp",EDGE,"E33")])]})});var subQ52=makeQuery(id+"F24.opExtrude","SWEPT_FACE",FACE,{"disambiguationData":[OSD([sQuery(id+"F11.wireOp",EDGE,"E32")])]});var subQ53=makeQuery(id+"F24.opExtrude","SWEPT_FACE",FACE,{"disambiguationData":[OSD([sQuery(id+"F11.wireOp",EDGE,"E34")])]});var subQ54=makeQuery(id+"F15.opExtrude","CAP_FACE",FACE,{"disambiguationData":[OSD([subQ30,subQ29,subQ28,sQuery(id+"F12.wireOp",EDGE,"E86.0"),sQuery(id+"F12.wireOp",EDGE,"E97"),subQ21])],"isStart":false});Q0=makeQuery(id+"F26.boolean.opBoolean","SPLIT",FACE,{"disambiguationData":[TD([subQ33])],"derivedFrom":makeQuery(id+"F24.boolean.opBoolean","SPLIT",FACE,{"disambiguationData":[TD([makeQuery(id+"F2.opShell","OFFSET_FACE",FACE,{"disambiguationData":[OSD([subQ31,subQ30,subQ29,subQ28]),TDD([makeQuery(id+"F1.opExtrude","CAP_FACE",FACE,{"disambiguationData":[OSD([subQ31,subQ30,subQ29,subQ28])],"isStart":true})])]}),subQ32,subQ33,subQ37,subQ54,subQ22,subQ34,subQ23,subQ25,subQ27,subQ36,subQ39,subQ20,subQ18,subQ14,subQ12,subQ10,subQ8,subQ5,subQ3,subQ26,subQ35,subQ1,subQ24,subQ40,subQ42,subQ43,subQ44,subQ45,subQ46,subQ47,subQ16,subQ38,subQ6,makeQuery(id+"F18.opExtrude","SWEPT_FACE",FACE,{"disambiguationData":[OSD([sQuery(id+"F13.wireOp",EDGE,"E106")])]}),makeQuery(id+"F18.boolean.opBoolean","COPY",FACE,{"derivedFrom":makeQuery(id+"F18.opExtrude","SWEPT_FACE",FACE,{"disambiguationData":[OSD([sQuery(id+"F13.wireOp",EDGE,"E103")])]})}),makeQuery(id+"F18.boolean.opBoolean","COPY",FACE,{"derivedFrom":makeQuery(id+"F18.opExtrude","SWEPT_FACE",FACE,{"disambiguationData":[OSD([sQuery(id+"F13.wireOp",EDGE,"E104")])]})}),subQ48,subQ50,subQ51,makeQuery(id+"F23.boolean.opBoolean","COPY",FACE,{"derivedFrom":makeQuery(id+"F23.opExtrude","SWEPT_FACE",FACE,{"disambiguationData":[OSD([sQuery(id+"F11.wireOp",EDGE,"E42.MirrorCS")])]})}),makeQuery(id+"F23.boolean.opBoolean","COPY",FACE,{"derivedFrom":makeQuery(id+"F23.opExtrude","SWEPT_FACE",FACE,{"disambiguationData":[OSD([sQuery(id+"F11.wireOp",EDGE,"E45.MirrorCS")])]})}),makeQuery(id+"F23.boolean.opBoolean","COPY",FACE,{"derivedFrom":makeQuery(id+"F23.opExtrude","SWEPT_FACE",FACE,{"disambiguationData":[OSD([sQuery(id+"F11.wireOp",EDGE,"E46.MirrorCS")])]})}),makeQuery(id+"F23.boolean.opBoolean","COPY",FACE,{"derivedFrom":makeQuery(id+"F23.opExtrude","SWEPT_FACE",FACE,{"disambiguationData":[OSD([sQuery(id+"F11.wireOp",EDGE,"E57")])]})}),makeQuery(id+"F23.boolean.opBoolean","COPY",FACE,{"derivedFrom":makeQuery(id+"F23.opExtrude","SWEPT_FACE",FACE,{"disambiguationData":[OSD([sQuery(id+"F11.wireOp",EDGE,"E58")])]})}),makeQuery(id+"F23.boolean.opBoolean","COPY",FACE,{"derivedFrom":makeQuery(id+"F23.opExtrude","SWEPT_FACE",FACE,{"disambiguationData":[OSD([sQuery(id+"F11.wireOp",EDGE,"E59")])]})}),subQ52,subQ53,subQ41,makeQuery(id+"F24.opExtrude","SWEPT_FACE",FACE,{"disambiguationData":[OSD([sQuery(id+"F11.wireOp",EDGE,"E39.MirrorCS")])]}),makeQuery(id+"F24.opExtrude","SWEPT_FACE",FACE,{"disambiguationData":[OSD([sQuery(id+"F11.wireOp",EDGE,"E40.MirrorCS")])]}),makeQuery(id+"F24.opExtrude","SWEPT_FACE",FACE,{"disambiguationData":[OSD([sQuery(id+"F11.wireOp",EDGE,"E41.MirrorCS"),sQuery(id+"F11.wireOp",EDGE,"E52.trimOffspring")])]}),makeQuery(id+"F24.opExtrude","SWEPT_FACE",FACE,{"disambiguationData":[OSD([subQ31,subQ29])]})])],"derivedFrom":makeQuery(id+"F20.boolean.opBoolean","MERGE",FACE,{"derivedFrom":[subQ54],"fromTools":[makeQuery(id+"F20.opExtrude","CAP_FACE",FACE,{"disambiguationData":[OSD([sQuery(id+"F19.wireOp",EDGE,"E152.0"),sQuery(id+"F19.wireOp",EDGE,"E152.1"),sQuery(id+"F19.wireOp",EDGE,"E152.2"),sQuery(id+"F19.wireOp",EDGE,"E152.3"),sQuery(id+"F19.wireOp",EDGE,"E152.4"),sQuery(id+"F19.wireOp",EDGE,"E153"),sQuery(id+"F19.wireOp",EDGE,"E154"),sQuery(id+"F19.wireOp",EDGE,"E155")])],"isStart":true})]})})});}
            var sketch = newSketch(context, id + "F29", { "sketchPlane" : qUnion([Q0])});
            skCircle(sketch, "E167", {"center": v(0, 0) * mm, "radius": 7 * mm});
            skPoint(sketch, "E167.first.point", {"position": v(-7, 0) * mm});
            skLineSegment(sketch, "E168", {"start": v(-6.4, 0) * mm, "end": v(-5.04, 1.18) * mm});
            skLineSegment(sketch, "E169", {"start": v(-5.04, 1.18) * mm, "end": v(-4.36, 0.76) * mm});
            skLineSegment(sketch, "E170", {"start": v(-4.36, 0.76) * mm, "end": v(-3.18, 0.58) * mm});
            skLineSegment(sketch, "E171", {"start": v(-3.18, 0.58) * mm, "end": v(-3.82, 1.05) * mm});
            skLineSegment(sketch, "E172", {"start": v(-3.82, 1.05) * mm, "end": v(-4.46, 1.82) * mm});
            skLineSegment(sketch, "E173", {"start": v(-4.46, 1.82) * mm, "end": v(-3.69, 2.46) * mm});
            skLineSegment(sketch, "E174", {"start": v(-3.69, 2.46) * mm, "end": v(-2.93, 1.53) * mm});
            skLineSegment(sketch, "E175", {"start": v(-2.93, 1.53) * mm, "end": v(-2.25, 1.1) * mm});
            skLineSegment(sketch, "E176", {"start": v(-2.25, 1.1) * mm, "end": v(-1.5, 0.84) * mm});
            skLineSegment(sketch, "E177", {"start": v(-1.5, 0.84) * mm, "end": v(-0.7, 0.84) * mm});
            skLineSegment(sketch, "E178", {"start": v(-0.7, 0.84) * mm, "end": v(0.06, 1.09) * mm});
            skLineSegment(sketch, "E179", {"start": v(0.06, 1.09) * mm, "end": v(0.73, 1.53) * mm});
            skLineSegment(sketch, "E180", {"start": v(0.73, 1.53) * mm, "end": v(1.14, 2.22) * mm});
            skLineSegment(sketch, "E181", {"start": v(1.14, 2.22) * mm, "end": v(1.14, 3.02) * mm});
            skLineSegment(sketch, "E182", {"start": v(1.14, 3.02) * mm, "end": v(0.79, 3.74) * mm});
            skLineSegment(sketch, "E183", {"start": v(0.79, 3.74) * mm, "end": v(0.18, 4.27) * mm});
            skLineSegment(sketch, "E184", {"start": v(0.18, 4.27) * mm, "end": v(-0.93, 4.72) * mm});
            skLineSegment(sketch, "E185", {"start": v(-0.93, 4.72) * mm, "end": v(-1.93, 4.72) * mm});
            skLineSegment(sketch, "E186", {"start": v(-1.93, 4.72) * mm, "end": v(-3.09, 4.4) * mm});
            skLineSegment(sketch, "E187", {"start": v(-3.09, 4.4) * mm, "end": v(-3.84, 4.13) * mm});
            skLineSegment(sketch, "E188", {"start": v(-3.84, 4.13) * mm, "end": v(-4.9, 3.56) * mm});
            skLineSegment(sketch, "E189", {"start": v(-4.9, 3.56) * mm, "end": v(-5.04, 3.42) * mm});
            skPoint(sketch, "E190", {"position": v(7, 0) * mm});
            skLineSegment(sketch, "E191.MirrorCS", {"start": v(-4.9, -3.56) * mm, "end": v(-5.04, -3.42) * mm});
            skLineSegment(sketch, "E192.MirrorCS", {"start": v(-4.46, -1.82) * mm, "end": v(-3.69, -2.46) * mm});
            skLineSegment(sketch, "E193.MirrorCS", {"start": v(-5.04, -1.18) * mm, "end": v(-4.36, -0.76) * mm});
            skLineSegment(sketch, "E194.MirrorCS", {"start": v(-0.93, -4.72) * mm, "end": v(-1.93, -4.72) * mm});
            skLineSegment(sketch, "E195.MirrorCS", {"start": v(-3.82, -1.05) * mm, "end": v(-4.46, -1.82) * mm});
            skLineSegment(sketch, "E196.MirrorCS", {"start": v(-2.25, -1.1) * mm, "end": v(-1.5, -0.84) * mm});
            skLineSegment(sketch, "E197.MirrorCS", {"start": v(0.06, -1.09) * mm, "end": v(0.73, -1.53) * mm});
            skLineSegment(sketch, "E198.MirrorCS", {"start": v(-3.69, -2.46) * mm, "end": v(-2.93, -1.53) * mm});
            skLineSegment(sketch, "E199.MirrorCS", {"start": v(1.14, -2.22) * mm, "end": v(1.14, -3.02) * mm});
            skLineSegment(sketch, "E200.MirrorCS", {"start": v(-0.7, -0.84) * mm, "end": v(0.06, -1.09) * mm});
            skLineSegment(sketch, "E201.MirrorCS", {"start": v(0.79, -3.74) * mm, "end": v(0.18, -4.27) * mm});
            skLineSegment(sketch, "E202.MirrorCS", {"start": v(-3.18, -0.58) * mm, "end": v(-3.82, -1.05) * mm});
            skLineSegment(sketch, "E203.MirrorCS", {"start": v(1.14, -3.02) * mm, "end": v(0.79, -3.74) * mm});
            skLineSegment(sketch, "E204.MirrorCS", {"start": v(0.73, -1.53) * mm, "end": v(1.14, -2.22) * mm});
            skLineSegment(sketch, "E205.MirrorCS", {"start": v(-2.93, -1.53) * mm, "end": v(-2.25, -1.1) * mm});
            skLineSegment(sketch, "E206.MirrorCS", {"start": v(-3.84, -4.13) * mm, "end": v(-4.9, -3.56) * mm});
            skLineSegment(sketch, "E207.MirrorCS", {"start": v(0.18, -4.27) * mm, "end": v(-0.93, -4.72) * mm});
            skLineSegment(sketch, "E208.MirrorCS", {"start": v(-1.5, -0.84) * mm, "end": v(-0.7, -0.84) * mm});
            skLineSegment(sketch, "E209.MirrorCS", {"start": v(-3.09, -4.4) * mm, "end": v(-3.84, -4.13) * mm});
            skLineSegment(sketch, "E210.MirrorCS", {"start": v(-1.93, -4.72) * mm, "end": v(-3.09, -4.4) * mm});
            skLineSegment(sketch, "E211.MirrorCS", {"start": v(-4.36, -0.76) * mm, "end": v(-3.18, -0.58) * mm});
            skLineSegment(sketch, "E212.MirrorCS", {"start": v(-6.4, 0) * mm, "end": v(-5.04, -1.18) * mm});
            skArc(sketch, "E213", {"start": v(-5.04, -3.42) * mm, "mid": v(6.1, 0) * mm, "end": v(-5.04, 3.42) * mm});
            skLineSegment(sketch, "E214.0", {"start": v(-26.5, -39.2) * mm, "end": v(-26.5, 39.2) * mm});
            skLineSegment(sketch, "E215", {"start": v(-7, 0) * mm, "end": v(-26.5, 0) * mm});
            skSolve(sketch);
        }
        {
            var Q0;
            Q0 = qSketchRegion(id + "F28", true);
            var Q1;
            Q1=makeQuery(id+"F29.imprint","IMPRINT",FACE,{"disambiguationData":[TD([[makeQuery(id+"F29.imprint","IMPRINT",EDGE,{"derivedFrom":sQuery(id+"F29.wireOp",EDGE,"E168")}),-1.0]])]});
            extrude(context, id + "F30", {"entities" : qUnion([Q0, Q1]), "operationType" : NewBodyOperationType.ADD, "depth" : .5 * mm, "offsetDistance" : 25 * mm});
        }
        {
            var Q0;
            Q0=makeQuery(id+"F17.opExtrude","SWEPT_FACE",FACE,{"disambiguationData":[OSD([sQuery(id+"F14.wireOp",EDGE,"E118")])]});
            var Q1;
            Q1=makeQuery(id+"F17.opExtrude","SWEPT_FACE",FACE,{"disambiguationData":[OSD([sQuery(id+"F14.wireOp",EDGE,"E114")])]});
            var Q2;
            Q2=makeQuery(id+"F17.opExtrude","SWEPT_FACE",FACE,{"disambiguationData":[OSD([sQuery(id+"F14.wireOp",EDGE,"E134.MirrorCS")])]});
            var Q3;
            Q3=makeQuery(id+"F17.opExtrude","SWEPT_FACE",FACE,{"disambiguationData":[OSD([sQuery(id+"F14.wireOp",EDGE,"E132.MirrorCS")])]});
            var Q4;
            Q4=makeQuery(id+"F17.opExtrude","SWEPT_EDGE",EDGE,{"disambiguationData":[OSD([sQuery(id+"F14.wireOp",EDGE,"E133.MirrorCS"),sQuery(id+"F14.wireOp",EDGE,"E143.MirrorCS")])]});
            var Q5;
            Q5=makeQuery(id+"F17.opExtrude","SWEPT_EDGE",EDGE,{"disambiguationData":[OSD([sQuery(id+"F14.wireOp",EDGE,"E111.top"),sQuery(id+"F14.wireOp",EDGE,"E111.right")])]});
            var Q6;
            Q6=makeQuery(id+"F17.opExtrude","SWEPT_EDGE",EDGE,{"disambiguationData":[OSD([sQuery(id+"F14.wireOp",EDGE,"E135.MirrorCS"),sQuery(id+"F14.wireOp",EDGE,"E145.MirrorCS")])]});
            var Q7;
            Q7=makeQuery(id+"F17.opExtrude","SWEPT_EDGE",EDGE,{"disambiguationData":[OSD([sQuery(id+"F14.wireOp",EDGE,"E121"),sQuery(id+"F14.wireOp",EDGE,"E122")])]});
            var Q8;
            Q8=makeQuery(id+"F22.boolean.opBoolean","INTERSECT",EDGE,{"derivedFrom":[makeQuery(id+"F17.opExtrude","SWEPT_FACE",FACE,{"disambiguationData":[OSD([sQuery(id+"F14.wireOp",EDGE,"E121")])]}),makeQuery(id+"F22.opExtrude","SWEPT_FACE",FACE,{"disambiguationData":[OSD([sQuery(id+"F21.wireOp",EDGE,"E156.0"),sQuery(id+"F21.wireOp",EDGE,"E156.1"),sQuery(id+"F21.wireOp",EDGE,"E156.2")])]})]});
            var Q9;
            Q9=makeQuery(id+"F22.boolean.opBoolean","INTERSECT",EDGE,{"derivedFrom":[makeQuery(id+"F17.opExtrude","SWEPT_FACE",FACE,{"disambiguationData":[OSD([sQuery(id+"F14.wireOp",EDGE,"E145.MirrorCS")])]}),makeQuery(id+"F22.opExtrude","SWEPT_FACE",FACE,{"disambiguationData":[OSD([sQuery(id+"F21.wireOp",EDGE,"E156.0"),sQuery(id+"F21.wireOp",EDGE,"E156.1"),sQuery(id+"F21.wireOp",EDGE,"E156.2")])]})]});
            var Q10;
            {var subQ0=makeQuery(id+"F1.opExtrude","SWEPT_FACE",FACE,{"disambiguationData":[OSD([sQuery(id+"F0.wireOp",EDGE,"E0.left")])]});var subQ1=makeQuery(id+"F4.opExtrude","SWEPT_FACE",FACE,{"disambiguationData":[OSD([sQuery(id+"F3.wireOp",EDGE,"E3")])]});var subQ2=makeQuery(id+"F16.opExtrude","SWEPT_FACE",FACE,{"disambiguationData":[OSD([sQuery(id+"F14.wireOp",EDGE,"E123"),sQuery(id+"F14.wireOp",EDGE,"E128"),sQuery(id+"F14.wireOp",EDGE,"E141.MirrorCS")])]});var subQ3=makeQuery(id+"F4.opExtrude","SWEPT_FACE",FACE,{"disambiguationData":[OSD([sQuery(id+"F3.wireOp",EDGE,"E22.MirrorCS")])]});Q10=makeQuery(id+"F17.boolean.opBoolean","SPLIT",EDGE,{"disambiguationData":[topologyDisambiguationEdgeConnected([makeQuery(id+"F16.boolean.opBoolean","COPY",FACE,{"derivedFrom":subQ2})])],"derivedFrom":makeQuery(id+"F16.boolean.opBoolean","INTERSECT",EDGE,{"derivedFrom":[makeQuery(id+"F4.boolean.opBoolean","MERGE",FACE,{"derivedFrom":[subQ0,subQ1,subQ3]}),subQ2]})});}
            var Q11;
            Q11=makeQuery(id+"F22.boolean.opBoolean","INTERSECT",EDGE,{"derivedFrom":[makeQuery(id+"F17.opExtrude","SWEPT_FACE",FACE,{"disambiguationData":[OSD([sQuery(id+"F14.wireOp",EDGE,"E122")])]}),makeQuery(id+"F22.opExtrude","SWEPT_FACE",FACE,{"disambiguationData":[OSD([sQuery(id+"F21.wireOp",EDGE,"E156.0"),sQuery(id+"F21.wireOp",EDGE,"E156.1"),sQuery(id+"F21.wireOp",EDGE,"E156.2")])]})]});
            var Q12;
            Q12=makeQuery(id+"F22.boolean.opBoolean","INTERSECT",EDGE,{"derivedFrom":[makeQuery(id+"F17.opExtrude","SWEPT_FACE",FACE,{"disambiguationData":[OSD([sQuery(id+"F14.wireOp",EDGE,"E135.MirrorCS")])]}),makeQuery(id+"F22.opExtrude","SWEPT_FACE",FACE,{"disambiguationData":[OSD([sQuery(id+"F21.wireOp",EDGE,"E156.0"),sQuery(id+"F21.wireOp",EDGE,"E156.1"),sQuery(id+"F21.wireOp",EDGE,"E156.2")])]})]});
            var Q13;
            Q13=makeQuery(id+"Fqk0GYrLWmHw1Jh_1.boolean.opBoolean","COPY",EDGE,{"derivedFrom":makeQuery(id+"Fqk0GYrLWmHw1Jh_1.opExtrude","SWEPT_EDGE",EDGE,{"disambiguationData":[OSD([sQuery(id+"F13.wireOp",EDGE,"E105"),sQuery(id+"FH58A1gKKjIODjq_1.wireOp",EDGE,"a6ba17af-4564-4ff5-a861-2eb783c5401d.MirrorCS"),sQuery(id+"FH58A1gKKjIODjq_1.wireOp",EDGE,"0dd72119-8f51-4d7e-96b1-4d8732446d24.MirrorCS")])]})});
            var Q14;
            Q14=makeQuery(id+"Fqk0GYrLWmHw1Jh_1.boolean.opBoolean","COPY",EDGE,{"derivedFrom":makeQuery(id+"Fqk0GYrLWmHw1Jh_1.opExtrude","SWEPT_EDGE",EDGE,{"disambiguationData":[OSD([sQuery(id+"F13.wireOp",EDGE,"E105"),sQuery(id+"FH58A1gKKjIODjq_1.wireOp",EDGE,"a6ba17af-4564-4ff5-a861-2eb783c5401d.MirrorCS"),sQuery(id+"FH58A1gKKjIODjq_1.wireOp",EDGE,"37d8ba7a-d749-4646-84ec-b879ac3784d4.MirrorCS")])]})});
            var Q15;
            Q15=makeQuery(id+"Fqk0GYrLWmHw1Jh_1.boolean.opBoolean","COPY",EDGE,{"derivedFrom":makeQuery(id+"Fqk0GYrLWmHw1Jh_1.opExtrude","CAP_EDGE",EDGE,{"disambiguationData":[OSD([sQuery(id+"FH58A1gKKjIODjq_1.wireOp",EDGE,"a6ba17af-4564-4ff5-a861-2eb783c5401d.MirrorCS")])],"isStart":false})});
            var Q16;
            Q16=makeQuery(id+"Fqk0GYrLWmHw1Jh_1.boolean.opBoolean","COPY",EDGE,{"derivedFrom":makeQuery(id+"Fqk0GYrLWmHw1Jh_1.opExtrude","SWEPT_EDGE",EDGE,{"disambiguationData":[OSD([sQuery(id+"F13.wireOp",EDGE,"E105"),sQuery(id+"FH58A1gKKjIODjq_1.wireOp",EDGE,"d27ddd09-024d-48fa-96d3-9767ec810702.MirrorCS"),sQuery(id+"FH58A1gKKjIODjq_1.wireOp",EDGE,"7c6cbe10-4fc4-4eb0-bddc-951cd9e7604b.MirrorCS")])]})});
            var Q17;
            Q17=makeQuery(id+"Fqk0GYrLWmHw1Jh_1.boolean.opBoolean","COPY",EDGE,{"derivedFrom":makeQuery(id+"Fqk0GYrLWmHw1Jh_1.opExtrude","SWEPT_EDGE",EDGE,{"disambiguationData":[OSD([sQuery(id+"F13.wireOp",EDGE,"E105"),sQuery(id+"FH58A1gKKjIODjq_1.wireOp",EDGE,"d27ddd09-024d-48fa-96d3-9767ec810702.MirrorCS"),sQuery(id+"FH58A1gKKjIODjq_1.wireOp",EDGE,"2b0c21f7-22b3-4024-b334-07cf4645b8e8.MirrorCS")])]})});
            var Q18;
            Q18=makeQuery(id+"Fqk0GYrLWmHw1Jh_1.boolean.opBoolean","COPY",EDGE,{"derivedFrom":makeQuery(id+"Fqk0GYrLWmHw1Jh_1.opExtrude","CAP_EDGE",EDGE,{"disambiguationData":[OSD([sQuery(id+"FH58A1gKKjIODjq_1.wireOp",EDGE,"d27ddd09-024d-48fa-96d3-9767ec810702.MirrorCS")])],"isStart":false})});
            fillet(context, id + "F31", {"entities" : qUnion([Q0, Q1, Q2, Q3, Q4, Q5, Q6, Q7, Q8, Q9, Q10, Q11, Q12, Q13, Q14, Q15, Q16, Q17, Q18]), "radius" : .4 * mm, "tangentPropagation" : true, "allowEdgeOverflow" : false});
        }
        {
            var Q0;
            {var subQ0=sQuery(id+"F3.wireOp",EDGE,"E11.MirrorCS");var subQ1=sQuery(id+"F3.wireOp",EDGE,"E10.MirrorCS");var subQ2=sQuery(id+"F0.wireOp",EDGE,"E0.right");Q0=makeQuery(id+"F16.boolean.opBoolean","SPLIT",EDGE,{"disambiguationData":[topologyDisambiguationEdgeConnected([makeQuery(id+"F2.opShell","OFFSET_FACE",FACE,{"disambiguationData":[OSD([subQ2])]})])],"derivedFrom":makeQuery(id+"F8.opFillet","BLEND_EDGE",EDGE,{"blendedFrom":[makeQuery(id+"F4.boolean.opBoolean","MERGE",EDGE,{"derivedFrom":[makeQuery(id+"F1.opExtrude","CAP_EDGE",EDGE,{"disambiguationData":[OSD([subQ2])],"isStart":false}),makeQuery(id+"F4.opExtrude","SWEPT_EDGE",EDGE,{"disambiguationData":[OSD([subQ1,subQ0])]})]}),makeQuery(id+"F4.boolean.opBoolean","MERGE",FACE,{"derivedFrom":[makeQuery(id+"F1.opExtrude","CAP_FACE",FACE,{"disambiguationData":[OSD([sQuery(id+"F0.wireOp",EDGE,"E0.bottom"),sQuery(id+"F0.wireOp",EDGE,"E0.top"),sQuery(id+"F0.wireOp",EDGE,"E0.left"),subQ2])],"isStart":false}),makeQuery(id+"F4.opExtrude","SWEPT_FACE",FACE,{"disambiguationData":[OSD([sQuery(id+"F3.wireOp",EDGE,"E2")])]}),makeQuery(id+"F4.opExtrude","SWEPT_FACE",FACE,{"disambiguationData":[OSD([subQ1])]})]})],"blendedInto":[makeQuery(id+"F4.boolean.opBoolean","MERGE",FACE,{"derivedFrom":[makeQuery(id+"F1.opExtrude","CAP_FACE",FACE,{"disambiguationData":[OSD([sQuery(id+"F0.wireOp",EDGE,"E0.bottom"),sQuery(id+"F0.wireOp",EDGE,"E0.top"),sQuery(id+"F0.wireOp",EDGE,"E0.left"),subQ2])],"isStart":false}),makeQuery(id+"F4.opExtrude","SWEPT_FACE",FACE,{"disambiguationData":[OSD([sQuery(id+"F3.wireOp",EDGE,"E2")])]}),makeQuery(id+"F4.opExtrude","SWEPT_FACE",FACE,{"disambiguationData":[OSD([subQ1])]})]})]})});}
            var Q1;
            Q1=makeQuery(id+"F16.boolean.opBoolean","INTERSECT",EDGE,{"derivedFrom":[makeQuery(id+"F4.boolean.opBoolean","MERGE",FACE,{"derivedFrom":[makeQuery(id+"F1.opExtrude","CAP_FACE",FACE,{"disambiguationData":[OSD([sQuery(id+"F0.wireOp",EDGE,"E0.bottom"),sQuery(id+"F0.wireOp",EDGE,"E0.top"),sQuery(id+"F0.wireOp",EDGE,"E0.left"),sQuery(id+"F0.wireOp",EDGE,"E0.right")])],"isStart":false}),makeQuery(id+"F4.opExtrude","SWEPT_FACE",FACE,{"disambiguationData":[OSD([sQuery(id+"F3.wireOp",EDGE,"E2")])]}),makeQuery(id+"F4.opExtrude","SWEPT_FACE",FACE,{"disambiguationData":[OSD([sQuery(id+"F3.wireOp",EDGE,"E10.MirrorCS")])]})]}),makeQuery(id+"F16.opExtrude","SWEPT_FACE",FACE,{"disambiguationData":[OSD([sQuery(id+"F14.wireOp",EDGE,"E120")])]})]});
            var Q2;
            Q2=makeQuery(id+"F26.boolean.opBoolean","INTERSECT",EDGE,{"derivedFrom":[makeQuery(id+"F18.boolean.opBoolean","COPY",FACE,{"derivedFrom":makeQuery(id+"F18.opExtrude","SWEPT_FACE",FACE,{"disambiguationData":[OSD([sQuery(id+"F13.wireOp",EDGE,"E103")])]})}),makeQuery(id+"F26.opExtrude","CAP_FACE",FACE,{"disambiguationData":[OSD([sQuery(id+"F11.wireOp",EDGE,"E31"),sQuery(id+"F11.wireOp",EDGE,"E46.MirrorCS"),sQuery(id+"F11.wireOp",EDGE,"E55"),sQuery(id+"F11.wireOp",EDGE,"E57")])],"isStart":false})]});
            var Q3;
            Q3=makeQuery(id+"F26.boolean.opBoolean","INTERSECT",EDGE,{"derivedFrom":[makeQuery(id+"F18.boolean.opBoolean","COPY",FACE,{"derivedFrom":makeQuery(id+"F18.opExtrude","SWEPT_FACE",FACE,{"disambiguationData":[OSD([sQuery(id+"F13.wireOp",EDGE,"E104")])]})}),makeQuery(id+"F26.opExtrude","CAP_FACE",FACE,{"disambiguationData":[OSD([sQuery(id+"F11.wireOp",EDGE,"E31"),sQuery(id+"F11.wireOp",EDGE,"E46.MirrorCS"),sQuery(id+"F11.wireOp",EDGE,"E55"),sQuery(id+"F11.wireOp",EDGE,"E57")])],"isStart":false})]});
            var Q4;
            {var subQ0=sQuery(id+"F0.wireOp",EDGE,"E0.bottom");Q4=makeQuery(id+"F30.boolean.opBoolean","SPLIT",FACE,{"disambiguationData":[TD([makeQuery(id+"F30.opExtrude","SWEPT_FACE",FACE,{"disambiguationData":[OSD([sQuery(id+"F28.wireOp",EDGE,"E163.sketch_text.stroke-79")])]})])],"derivedFrom":makeQuery(id+"F20.boolean.opBoolean","MERGE",FACE,{"derivedFrom":[makeQuery(id+"F15.boolean.opBoolean","MERGE",FACE,{"derivedFrom":[makeQuery(id+"F1.opExtrude","SWEPT_FACE",FACE,{"disambiguationData":[OSD([subQ0])]}),makeQuery(id+"F15.opExtrude","CAP_FACE",FACE,{"disambiguationData":[OSD([subQ0,sQuery(id+"F0.wireOp",EDGE,"E0.left"),sQuery(id+"F0.wireOp",EDGE,"E0.right"),sQuery(id+"F11.wireOp",EDGE,"E50.0"),sQuery(id+"F11.wireOp",EDGE,"E61"),sQuery(id+"F11.wireOp",EDGE,"E62"),sQuery(id+"F11.wireOp",EDGE,"E63")])],"isStart":true})]}),makeQuery(id+"F20.opExtrude","CAP_FACE",FACE,{"disambiguationData":[OSD([sQuery(id+"F19.wireOp",EDGE,"E151.bottom"),sQuery(id+"F19.wireOp",EDGE,"E151.top"),sQuery(id+"F19.wireOp",EDGE,"E151.left"),sQuery(id+"F19.wireOp",EDGE,"E151.right")])],"isStart":true})]})});}
            var Q5;
            {var subQ0=sQuery(id+"F0.wireOp",EDGE,"E0.bottom");Q5=makeQuery(id+"F30.boolean.opBoolean","SPLIT",FACE,{"disambiguationData":[TD([makeQuery(id+"F30.opExtrude","SWEPT_FACE",FACE,{"disambiguationData":[OSD([sQuery(id+"F28.wireOp",EDGE,"E163.sketch_text.stroke-19")])]})])],"derivedFrom":makeQuery(id+"F20.boolean.opBoolean","MERGE",FACE,{"derivedFrom":[makeQuery(id+"F15.boolean.opBoolean","MERGE",FACE,{"derivedFrom":[makeQuery(id+"F1.opExtrude","SWEPT_FACE",FACE,{"disambiguationData":[OSD([subQ0])]}),makeQuery(id+"F15.opExtrude","CAP_FACE",FACE,{"disambiguationData":[OSD([subQ0,sQuery(id+"F0.wireOp",EDGE,"E0.left"),sQuery(id+"F0.wireOp",EDGE,"E0.right"),sQuery(id+"F11.wireOp",EDGE,"E50.0"),sQuery(id+"F11.wireOp",EDGE,"E61"),sQuery(id+"F11.wireOp",EDGE,"E62"),sQuery(id+"F11.wireOp",EDGE,"E63")])],"isStart":true})]}),makeQuery(id+"F20.opExtrude","CAP_FACE",FACE,{"disambiguationData":[OSD([sQuery(id+"F19.wireOp",EDGE,"E151.bottom"),sQuery(id+"F19.wireOp",EDGE,"E151.top"),sQuery(id+"F19.wireOp",EDGE,"E151.left"),sQuery(id+"F19.wireOp",EDGE,"E151.right")])],"isStart":true})]})});}
            var Q6;
            {var subQ0=sQuery(id+"F0.wireOp",EDGE,"E0.bottom");Q6=makeQuery(id+"F30.boolean.opBoolean","SPLIT",FACE,{"disambiguationData":[TD([makeQuery(id+"F30.opExtrude","SWEPT_FACE",FACE,{"disambiguationData":[OSD([sQuery(id+"F28.wireOp",EDGE,"E163.sketch_text.stroke-12")])]})])],"derivedFrom":makeQuery(id+"F20.boolean.opBoolean","MERGE",FACE,{"derivedFrom":[makeQuery(id+"F15.boolean.opBoolean","MERGE",FACE,{"derivedFrom":[makeQuery(id+"F1.opExtrude","SWEPT_FACE",FACE,{"disambiguationData":[OSD([subQ0])]}),makeQuery(id+"F15.opExtrude","CAP_FACE",FACE,{"disambiguationData":[OSD([subQ0,sQuery(id+"F0.wireOp",EDGE,"E0.left"),sQuery(id+"F0.wireOp",EDGE,"E0.right"),sQuery(id+"F11.wireOp",EDGE,"E50.0"),sQuery(id+"F11.wireOp",EDGE,"E61"),sQuery(id+"F11.wireOp",EDGE,"E62"),sQuery(id+"F11.wireOp",EDGE,"E63")])],"isStart":true})]}),makeQuery(id+"F20.opExtrude","CAP_FACE",FACE,{"disambiguationData":[OSD([sQuery(id+"F19.wireOp",EDGE,"E151.bottom"),sQuery(id+"F19.wireOp",EDGE,"E151.top"),sQuery(id+"F19.wireOp",EDGE,"E151.left"),sQuery(id+"F19.wireOp",EDGE,"E151.right")])],"isStart":true})]})});}
            fillet(context, id + "F32", {"entities" : qUnion([Q0, Q1, Q2, Q3, Q4, Q5, Q6]), "radius" : .1 * mm, "tangentPropagation" : true, "allowEdgeOverflow" : false});
        }
    });
